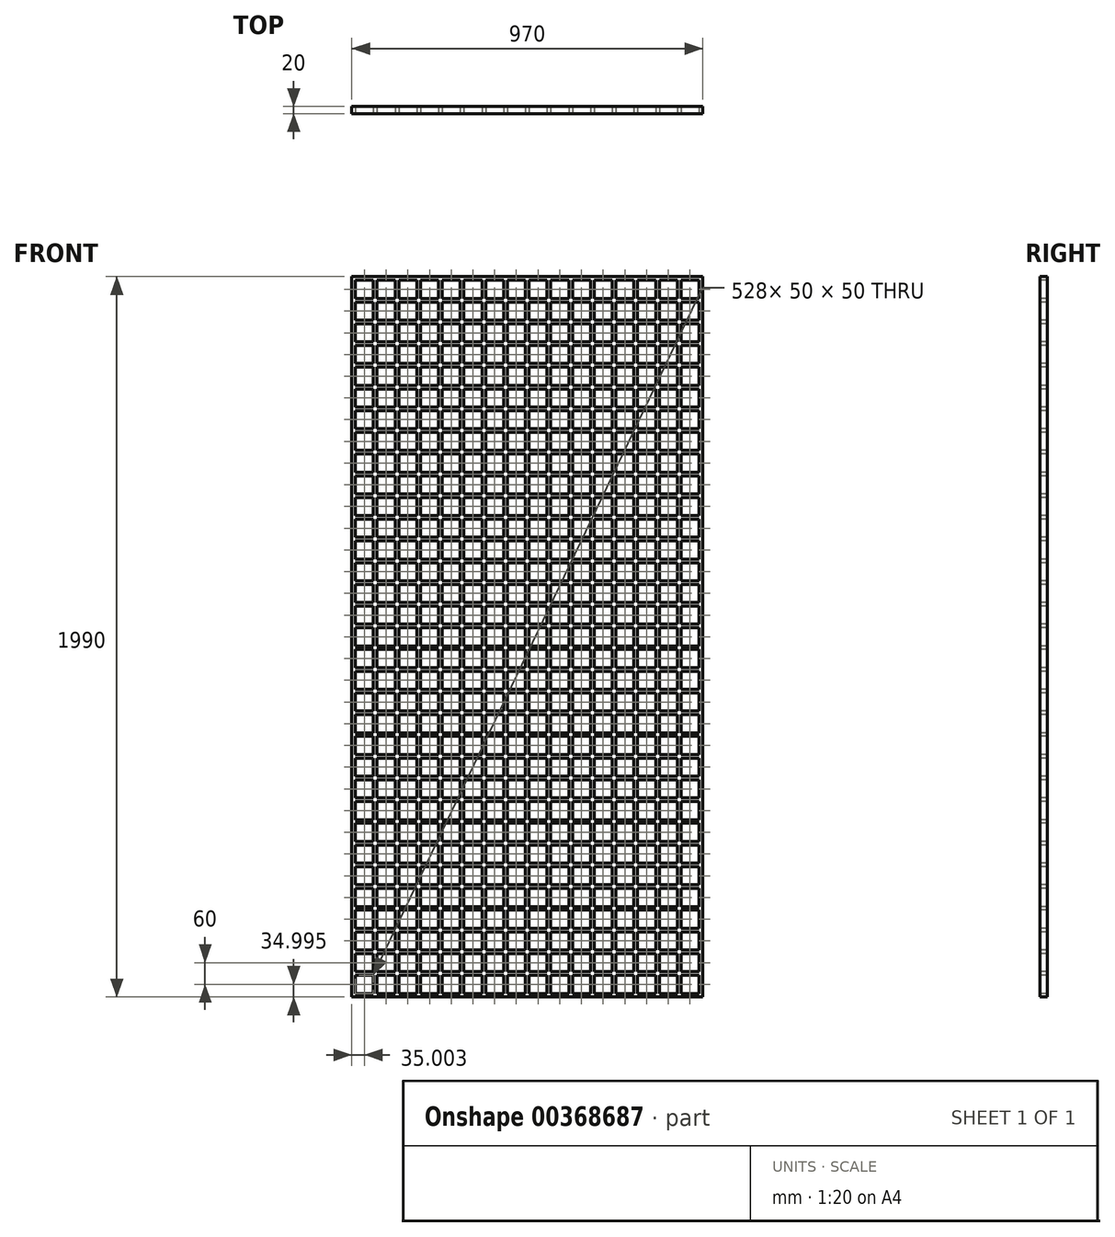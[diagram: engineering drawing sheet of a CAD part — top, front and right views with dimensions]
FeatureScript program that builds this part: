
annotation { "Feature Type Name" : "Feature", "Feature Type Description" : "" }
export const myFeature = defineFeature(function(context is Context, id is Id, definition is map)
    precondition{}
    {
        {
            var Q0;
            Q0=qCreatedBy(makeId("Front.planeOp"),FACE);
            var sketch = newSketch(context, id + "F0", { "sketchPlane" : qUnion([Q0])});
            skLineSegment(sketch, "E0.bottom", {"start": v(-491.66, 1631.1) * mm, "end": v(478.34, 1631.1) * mm});
            skLineSegment(sketch, "E0.top", {"start": v(-491.66, -358.9) * mm, "end": v(478.34, -358.9) * mm});
            skLineSegment(sketch, "E0.left", {"start": v(-491.66, 1631.1) * mm, "end": v(-491.66, -358.9) * mm});
            skLineSegment(sketch, "E0.right", {"start": v(478.34, 1631.1) * mm, "end": v(478.34, -358.9) * mm});
            skSolve(sketch);
        }
        {
            var Q0;
            Q0=makeQuery(id+"F0.imprint","IMPRINT",FACE,{"disambiguationData":[TD([[makeQuery(id+"F0.imprint","IMPRINT",EDGE,{"derivedFrom":sQuery(id+"F0.wireOp",EDGE,"E0.bottom")}),-1.0]])]});
            extrude(context, id + "F1", {"entities" : qUnion([Q0]), "depth" : 20 * mm});
        }
        {
            var Q0;
            Q0=makeQuery(id+"F1.opExtrude","CAP_FACE",FACE,{"disambiguationData":[OSD([sQuery(id+"F0.wireOp",EDGE,"E0.bottom"),sQuery(id+"F0.wireOp",EDGE,"E0.top"),sQuery(id+"F0.wireOp",EDGE,"E0.left"),sQuery(id+"F0.wireOp",EDGE,"E0.right")])],"isStart":false});
            var sketch = newSketch(context, id + "F2", { "sketchPlane" : qUnion([Q0])});
            skLineSegment(sketch, "E1.bottom", {"start": v(-481.66, 1621.1) * mm, "end": v(-431.66, 1621.1) * mm});
            skLineSegment(sketch, "E1.top", {"start": v(-481.66, 1571.1) * mm, "end": v(-431.66, 1571.1) * mm});
            skLineSegment(sketch, "E1.left", {"start": v(-481.66, 1621.1) * mm, "end": v(-481.66, 1571.1) * mm});
            skLineSegment(sketch, "E1.right", {"start": v(-431.66, 1621.1) * mm, "end": v(-431.66, 1571.1) * mm});
            skLineSegment(sketch, "E2.0.1.0", {"start": v(-431.66, 1561.1) * mm, "end": v(-431.66, 1511.1) * mm});
            skLineSegment(sketch, "E2.0.1.1", {"start": v(-481.66, 1511.1) * mm, "end": v(-431.66, 1511.1) * mm});
            skLineSegment(sketch, "E2.0.1.2", {"start": v(-481.66, 1561.1) * mm, "end": v(-481.66, 1511.1) * mm});
            skLineSegment(sketch, "E2.0.1.3", {"start": v(-481.66, 1561.1) * mm, "end": v(-431.66, 1561.1) * mm});
            skLineSegment(sketch, "E2.0.2.0", {"start": v(-431.66, 1501.1) * mm, "end": v(-431.66, 1451.1) * mm});
            skLineSegment(sketch, "E2.0.2.1", {"start": v(-481.66, 1451.1) * mm, "end": v(-431.66, 1451.1) * mm});
            skLineSegment(sketch, "E2.0.2.2", {"start": v(-481.66, 1501.1) * mm, "end": v(-481.66, 1451.1) * mm});
            skLineSegment(sketch, "E2.0.2.3", {"start": v(-481.66, 1501.1) * mm, "end": v(-431.66, 1501.1) * mm});
            skLineSegment(sketch, "E2.0.3.0", {"start": v(-431.66, 1441.1) * mm, "end": v(-431.66, 1391.1) * mm});
            skLineSegment(sketch, "E2.0.3.1", {"start": v(-481.66, 1391.1) * mm, "end": v(-431.66, 1391.1) * mm});
            skLineSegment(sketch, "E2.0.3.2", {"start": v(-481.66, 1441.1) * mm, "end": v(-481.66, 1391.1) * mm});
            skLineSegment(sketch, "E2.0.3.3", {"start": v(-481.66, 1441.1) * mm, "end": v(-431.66, 1441.1) * mm});
            skLineSegment(sketch, "E2.0.4.0", {"start": v(-431.66, 1381.1) * mm, "end": v(-431.66, 1331.1) * mm});
            skLineSegment(sketch, "E2.0.4.1", {"start": v(-481.66, 1331.1) * mm, "end": v(-431.66, 1331.1) * mm});
            skLineSegment(sketch, "E2.0.4.2", {"start": v(-481.66, 1381.1) * mm, "end": v(-481.66, 1331.1) * mm});
            skLineSegment(sketch, "E2.0.4.3", {"start": v(-481.66, 1381.1) * mm, "end": v(-431.66, 1381.1) * mm});
            skLineSegment(sketch, "E2.0.5.0", {"start": v(-431.66, 1321.1) * mm, "end": v(-431.66, 1271.1) * mm});
            skLineSegment(sketch, "E2.0.5.1", {"start": v(-481.66, 1271.1) * mm, "end": v(-431.66, 1271.1) * mm});
            skLineSegment(sketch, "E2.0.5.2", {"start": v(-481.66, 1321.1) * mm, "end": v(-481.66, 1271.1) * mm});
            skLineSegment(sketch, "E2.0.5.3", {"start": v(-481.66, 1321.1) * mm, "end": v(-431.66, 1321.1) * mm});
            skLineSegment(sketch, "E2.0.6.0", {"start": v(-431.66, 1261.1) * mm, "end": v(-431.66, 1211.1) * mm});
            skLineSegment(sketch, "E2.0.6.1", {"start": v(-481.66, 1211.1) * mm, "end": v(-431.66, 1211.1) * mm});
            skLineSegment(sketch, "E2.0.6.2", {"start": v(-481.66, 1261.1) * mm, "end": v(-481.66, 1211.1) * mm});
            skLineSegment(sketch, "E2.0.6.3", {"start": v(-481.66, 1261.1) * mm, "end": v(-431.66, 1261.1) * mm});
            skLineSegment(sketch, "E2.0.7.0", {"start": v(-431.66, 1201.1) * mm, "end": v(-431.66, 1151.1) * mm});
            skLineSegment(sketch, "E2.0.7.1", {"start": v(-481.66, 1151.1) * mm, "end": v(-431.66, 1151.1) * mm});
            skLineSegment(sketch, "E2.0.7.2", {"start": v(-481.66, 1201.1) * mm, "end": v(-481.66, 1151.1) * mm});
            skLineSegment(sketch, "E2.0.7.3", {"start": v(-481.66, 1201.1) * mm, "end": v(-431.66, 1201.1) * mm});
            skLineSegment(sketch, "E2.0.8.0", {"start": v(-431.66, 1141.1) * mm, "end": v(-431.66, 1091.1) * mm});
            skLineSegment(sketch, "E2.0.8.1", {"start": v(-481.66, 1091.1) * mm, "end": v(-431.66, 1091.1) * mm});
            skLineSegment(sketch, "E2.0.8.2", {"start": v(-481.66, 1141.1) * mm, "end": v(-481.66, 1091.1) * mm});
            skLineSegment(sketch, "E2.0.8.3", {"start": v(-481.66, 1141.1) * mm, "end": v(-431.66, 1141.1) * mm});
            skLineSegment(sketch, "E2.0.9.0", {"start": v(-431.66, 1081.1) * mm, "end": v(-431.66, 1031.1) * mm});
            skLineSegment(sketch, "E2.0.9.1", {"start": v(-481.66, 1031.1) * mm, "end": v(-431.66, 1031.1) * mm});
            skLineSegment(sketch, "E2.0.9.2", {"start": v(-481.66, 1081.1) * mm, "end": v(-481.66, 1031.1) * mm});
            skLineSegment(sketch, "E2.0.9.3", {"start": v(-481.66, 1081.1) * mm, "end": v(-431.66, 1081.1) * mm});
            skLineSegment(sketch, "E2.0.10.0", {"start": v(-431.66, 1021.1) * mm, "end": v(-431.66, 971.1) * mm});
            skLineSegment(sketch, "E2.0.10.1", {"start": v(-481.66, 971.1) * mm, "end": v(-431.66, 971.1) * mm});
            skLineSegment(sketch, "E2.0.10.2", {"start": v(-481.66, 1021.1) * mm, "end": v(-481.66, 971.1) * mm});
            skLineSegment(sketch, "E2.0.10.3", {"start": v(-481.66, 1021.1) * mm, "end": v(-431.66, 1021.1) * mm});
            skLineSegment(sketch, "E2.0.11.0", {"start": v(-431.66, 961.1) * mm, "end": v(-431.66, 911.1) * mm});
            skLineSegment(sketch, "E2.0.11.1", {"start": v(-481.66, 911.1) * mm, "end": v(-431.66, 911.1) * mm});
            skLineSegment(sketch, "E2.0.11.2", {"start": v(-481.66, 961.1) * mm, "end": v(-481.66, 911.1) * mm});
            skLineSegment(sketch, "E2.0.11.3", {"start": v(-481.66, 961.1) * mm, "end": v(-431.66, 961.1) * mm});
            skLineSegment(sketch, "E2.0.12.0", {"start": v(-431.66, 901.1) * mm, "end": v(-431.66, 851.1) * mm});
            skLineSegment(sketch, "E2.0.12.1", {"start": v(-481.66, 851.1) * mm, "end": v(-431.66, 851.1) * mm});
            skLineSegment(sketch, "E2.0.12.2", {"start": v(-481.66, 901.1) * mm, "end": v(-481.66, 851.1) * mm});
            skLineSegment(sketch, "E2.0.12.3", {"start": v(-481.66, 901.1) * mm, "end": v(-431.66, 901.1) * mm});
            skLineSegment(sketch, "E2.0.13.0", {"start": v(-431.66, 841.1) * mm, "end": v(-431.66, 791.1) * mm});
            skLineSegment(sketch, "E2.0.13.1", {"start": v(-481.66, 791.1) * mm, "end": v(-431.66, 791.1) * mm});
            skLineSegment(sketch, "E2.0.13.2", {"start": v(-481.66, 841.1) * mm, "end": v(-481.66, 791.1) * mm});
            skLineSegment(sketch, "E2.0.13.3", {"start": v(-481.66, 841.1) * mm, "end": v(-431.66, 841.1) * mm});
            skLineSegment(sketch, "E2.0.14.0", {"start": v(-431.66, 781.1) * mm, "end": v(-431.66, 731.1) * mm});
            skLineSegment(sketch, "E2.0.14.1", {"start": v(-481.66, 731.1) * mm, "end": v(-431.66, 731.1) * mm});
            skLineSegment(sketch, "E2.0.14.2", {"start": v(-481.66, 781.1) * mm, "end": v(-481.66, 731.1) * mm});
            skLineSegment(sketch, "E2.0.14.3", {"start": v(-481.66, 781.1) * mm, "end": v(-431.66, 781.1) * mm});
            skLineSegment(sketch, "E2.0.15.0", {"start": v(-431.66, 721.1) * mm, "end": v(-431.66, 671.1) * mm});
            skLineSegment(sketch, "E2.0.15.1", {"start": v(-481.66, 671.1) * mm, "end": v(-431.66, 671.1) * mm});
            skLineSegment(sketch, "E2.0.15.2", {"start": v(-481.66, 721.1) * mm, "end": v(-481.66, 671.1) * mm});
            skLineSegment(sketch, "E2.0.15.3", {"start": v(-481.66, 721.1) * mm, "end": v(-431.66, 721.1) * mm});
            skLineSegment(sketch, "E2.0.16.0", {"start": v(-431.66, 661.1) * mm, "end": v(-431.66, 611.1) * mm});
            skLineSegment(sketch, "E2.0.16.1", {"start": v(-481.66, 611.1) * mm, "end": v(-431.66, 611.1) * mm});
            skLineSegment(sketch, "E2.0.16.2", {"start": v(-481.66, 661.1) * mm, "end": v(-481.66, 611.1) * mm});
            skLineSegment(sketch, "E2.0.16.3", {"start": v(-481.66, 661.1) * mm, "end": v(-431.66, 661.1) * mm});
            skLineSegment(sketch, "E2.0.17.0", {"start": v(-431.66, 601.1) * mm, "end": v(-431.66, 551.1) * mm});
            skLineSegment(sketch, "E2.0.17.1", {"start": v(-481.66, 551.1) * mm, "end": v(-431.66, 551.1) * mm});
            skLineSegment(sketch, "E2.0.17.2", {"start": v(-481.66, 601.1) * mm, "end": v(-481.66, 551.1) * mm});
            skLineSegment(sketch, "E2.0.17.3", {"start": v(-481.66, 601.1) * mm, "end": v(-431.66, 601.1) * mm});
            skLineSegment(sketch, "E2.0.18.0", {"start": v(-431.66, 541.1) * mm, "end": v(-431.66, 491.1) * mm});
            skLineSegment(sketch, "E2.0.18.1", {"start": v(-481.66, 491.1) * mm, "end": v(-431.66, 491.1) * mm});
            skLineSegment(sketch, "E2.0.18.2", {"start": v(-481.66, 541.1) * mm, "end": v(-481.66, 491.1) * mm});
            skLineSegment(sketch, "E2.0.18.3", {"start": v(-481.66, 541.1) * mm, "end": v(-431.66, 541.1) * mm});
            skLineSegment(sketch, "E2.0.19.0", {"start": v(-431.66, 481.1) * mm, "end": v(-431.66, 431.1) * mm});
            skLineSegment(sketch, "E2.0.19.1", {"start": v(-481.66, 431.1) * mm, "end": v(-431.66, 431.1) * mm});
            skLineSegment(sketch, "E2.0.19.2", {"start": v(-481.66, 481.1) * mm, "end": v(-481.66, 431.1) * mm});
            skLineSegment(sketch, "E2.0.19.3", {"start": v(-481.66, 481.1) * mm, "end": v(-431.66, 481.1) * mm});
            skLineSegment(sketch, "E2.0.20.0", {"start": v(-431.66, 421.1) * mm, "end": v(-431.66, 371.1) * mm});
            skLineSegment(sketch, "E2.0.20.1", {"start": v(-481.66, 371.1) * mm, "end": v(-431.66, 371.1) * mm});
            skLineSegment(sketch, "E2.0.20.2", {"start": v(-481.66, 421.1) * mm, "end": v(-481.66, 371.1) * mm});
            skLineSegment(sketch, "E2.0.20.3", {"start": v(-481.66, 421.1) * mm, "end": v(-431.66, 421.1) * mm});
            skLineSegment(sketch, "E2.0.21.0", {"start": v(-431.66, 361.1) * mm, "end": v(-431.66, 311.1) * mm});
            skLineSegment(sketch, "E2.0.21.1", {"start": v(-481.66, 311.1) * mm, "end": v(-431.66, 311.1) * mm});
            skLineSegment(sketch, "E2.0.21.2", {"start": v(-481.66, 361.1) * mm, "end": v(-481.66, 311.1) * mm});
            skLineSegment(sketch, "E2.0.21.3", {"start": v(-481.66, 361.1) * mm, "end": v(-431.66, 361.1) * mm});
            skLineSegment(sketch, "E2.0.22.0", {"start": v(-431.66, 301.1) * mm, "end": v(-431.66, 251.1) * mm});
            skLineSegment(sketch, "E2.0.22.1", {"start": v(-481.66, 251.1) * mm, "end": v(-431.66, 251.1) * mm});
            skLineSegment(sketch, "E2.0.22.2", {"start": v(-481.66, 301.1) * mm, "end": v(-481.66, 251.1) * mm});
            skLineSegment(sketch, "E2.0.22.3", {"start": v(-481.66, 301.1) * mm, "end": v(-431.66, 301.1) * mm});
            skLineSegment(sketch, "E2.0.23.0", {"start": v(-431.66, 241.1) * mm, "end": v(-431.66, 191.1) * mm});
            skLineSegment(sketch, "E2.0.23.1", {"start": v(-481.66, 191.1) * mm, "end": v(-431.66, 191.1) * mm});
            skLineSegment(sketch, "E2.0.23.2", {"start": v(-481.66, 241.1) * mm, "end": v(-481.66, 191.1) * mm});
            skLineSegment(sketch, "E2.0.23.3", {"start": v(-481.66, 241.1) * mm, "end": v(-431.66, 241.1) * mm});
            skLineSegment(sketch, "E2.0.24.0", {"start": v(-431.66, 181.1) * mm, "end": v(-431.66, 131.1) * mm});
            skLineSegment(sketch, "E2.0.24.1", {"start": v(-481.66, 131.1) * mm, "end": v(-431.66, 131.1) * mm});
            skLineSegment(sketch, "E2.0.24.2", {"start": v(-481.66, 181.1) * mm, "end": v(-481.66, 131.1) * mm});
            skLineSegment(sketch, "E2.0.24.3", {"start": v(-481.66, 181.1) * mm, "end": v(-431.66, 181.1) * mm});
            skLineSegment(sketch, "E2.0.25.0", {"start": v(-431.66, 121.1) * mm, "end": v(-431.66, 71.1) * mm});
            skLineSegment(sketch, "E2.0.25.1", {"start": v(-481.66, 71.1) * mm, "end": v(-431.66, 71.1) * mm});
            skLineSegment(sketch, "E2.0.25.2", {"start": v(-481.66, 121.1) * mm, "end": v(-481.66, 71.1) * mm});
            skLineSegment(sketch, "E2.0.25.3", {"start": v(-481.66, 121.1) * mm, "end": v(-431.66, 121.1) * mm});
            skLineSegment(sketch, "E2.0.26.0", {"start": v(-431.66, 61.1) * mm, "end": v(-431.66, 11.1) * mm});
            skLineSegment(sketch, "E2.0.26.1", {"start": v(-481.66, 11.1) * mm, "end": v(-431.66, 11.1) * mm});
            skLineSegment(sketch, "E2.0.26.2", {"start": v(-481.66, 61.1) * mm, "end": v(-481.66, 11.1) * mm});
            skLineSegment(sketch, "E2.0.26.3", {"start": v(-481.66, 61.1) * mm, "end": v(-431.66, 61.1) * mm});
            skLineSegment(sketch, "E2.0.27.0", {"start": v(-431.66, 1.1) * mm, "end": v(-431.66, -48.9) * mm});
            skLineSegment(sketch, "E2.0.27.1", {"start": v(-481.66, -48.9) * mm, "end": v(-431.66, -48.9) * mm});
            skLineSegment(sketch, "E2.0.27.2", {"start": v(-481.66, 1.1) * mm, "end": v(-481.66, -48.9) * mm});
            skLineSegment(sketch, "E2.0.27.3", {"start": v(-481.66, 1.1) * mm, "end": v(-431.66, 1.1) * mm});
            skLineSegment(sketch, "E2.0.28.0", {"start": v(-431.66, -58.9) * mm, "end": v(-431.66, -108.9) * mm});
            skLineSegment(sketch, "E2.0.28.1", {"start": v(-481.66, -108.9) * mm, "end": v(-431.66, -108.9) * mm});
            skLineSegment(sketch, "E2.0.28.2", {"start": v(-481.66, -58.9) * mm, "end": v(-481.66, -108.9) * mm});
            skLineSegment(sketch, "E2.0.28.3", {"start": v(-481.66, -58.9) * mm, "end": v(-431.66, -58.9) * mm});
            skLineSegment(sketch, "E2.0.29.0", {"start": v(-431.66, -118.9) * mm, "end": v(-431.66, -168.9) * mm});
            skLineSegment(sketch, "E2.0.29.1", {"start": v(-481.66, -168.9) * mm, "end": v(-431.66, -168.9) * mm});
            skLineSegment(sketch, "E2.0.29.2", {"start": v(-481.66, -118.9) * mm, "end": v(-481.66, -168.9) * mm});
            skLineSegment(sketch, "E2.0.29.3", {"start": v(-481.66, -118.9) * mm, "end": v(-431.66, -118.9) * mm});
            skLineSegment(sketch, "E2.0.30.0", {"start": v(-431.66, -178.9) * mm, "end": v(-431.66, -228.9) * mm});
            skLineSegment(sketch, "E2.0.30.1", {"start": v(-481.66, -228.9) * mm, "end": v(-431.66, -228.9) * mm});
            skLineSegment(sketch, "E2.0.30.2", {"start": v(-481.66, -178.9) * mm, "end": v(-481.66, -228.9) * mm});
            skLineSegment(sketch, "E2.0.30.3", {"start": v(-481.66, -178.9) * mm, "end": v(-431.66, -178.9) * mm});
            skLineSegment(sketch, "E2.0.31.0", {"start": v(-431.66, -238.9) * mm, "end": v(-431.66, -288.9) * mm});
            skLineSegment(sketch, "E2.0.31.1", {"start": v(-481.66, -288.9) * mm, "end": v(-431.66, -288.9) * mm});
            skLineSegment(sketch, "E2.0.31.2", {"start": v(-481.66, -238.9) * mm, "end": v(-481.66, -288.9) * mm});
            skLineSegment(sketch, "E2.0.31.3", {"start": v(-481.66, -238.9) * mm, "end": v(-431.66, -238.9) * mm});
            skLineSegment(sketch, "E2.0.32.0", {"start": v(-431.66, -298.9) * mm, "end": v(-431.66, -348.9) * mm});
            skLineSegment(sketch, "E2.0.32.1", {"start": v(-481.66, -348.9) * mm, "end": v(-431.66, -348.9) * mm});
            skLineSegment(sketch, "E2.0.32.2", {"start": v(-481.66, -298.9) * mm, "end": v(-481.66, -348.9) * mm});
            skLineSegment(sketch, "E2.0.32.3", {"start": v(-481.66, -298.9) * mm, "end": v(-431.66, -298.9) * mm});
            skLineSegment(sketch, "E2.1.0.0", {"start": v(-371.66, 1621.1) * mm, "end": v(-371.66, 1571.1) * mm});
            skLineSegment(sketch, "E2.1.0.1", {"start": v(-421.66, 1571.1) * mm, "end": v(-371.66, 1571.1) * mm});
            skLineSegment(sketch, "E2.1.0.2", {"start": v(-421.66, 1621.1) * mm, "end": v(-421.66, 1571.1) * mm});
            skLineSegment(sketch, "E2.1.0.3", {"start": v(-421.66, 1621.1) * mm, "end": v(-371.66, 1621.1) * mm});
            skLineSegment(sketch, "E2.1.1.0", {"start": v(-371.66, 1561.1) * mm, "end": v(-371.66, 1511.1) * mm});
            skLineSegment(sketch, "E2.1.1.1", {"start": v(-421.66, 1511.1) * mm, "end": v(-371.66, 1511.1) * mm});
            skLineSegment(sketch, "E2.1.1.2", {"start": v(-421.66, 1561.1) * mm, "end": v(-421.66, 1511.1) * mm});
            skLineSegment(sketch, "E2.1.1.3", {"start": v(-421.66, 1561.1) * mm, "end": v(-371.66, 1561.1) * mm});
            skLineSegment(sketch, "E2.1.2.0", {"start": v(-371.66, 1501.1) * mm, "end": v(-371.66, 1451.1) * mm});
            skLineSegment(sketch, "E2.1.2.1", {"start": v(-421.66, 1451.1) * mm, "end": v(-371.66, 1451.1) * mm});
            skLineSegment(sketch, "E2.1.2.2", {"start": v(-421.66, 1501.1) * mm, "end": v(-421.66, 1451.1) * mm});
            skLineSegment(sketch, "E2.1.2.3", {"start": v(-421.66, 1501.1) * mm, "end": v(-371.66, 1501.1) * mm});
            skLineSegment(sketch, "E2.1.3.0", {"start": v(-371.66, 1441.1) * mm, "end": v(-371.66, 1391.1) * mm});
            skLineSegment(sketch, "E2.1.3.1", {"start": v(-421.66, 1391.1) * mm, "end": v(-371.66, 1391.1) * mm});
            skLineSegment(sketch, "E2.1.3.2", {"start": v(-421.66, 1441.1) * mm, "end": v(-421.66, 1391.1) * mm});
            skLineSegment(sketch, "E2.1.3.3", {"start": v(-421.66, 1441.1) * mm, "end": v(-371.66, 1441.1) * mm});
            skLineSegment(sketch, "E2.1.4.0", {"start": v(-371.66, 1381.1) * mm, "end": v(-371.66, 1331.1) * mm});
            skLineSegment(sketch, "E2.1.4.1", {"start": v(-421.66, 1331.1) * mm, "end": v(-371.66, 1331.1) * mm});
            skLineSegment(sketch, "E2.1.4.2", {"start": v(-421.66, 1381.1) * mm, "end": v(-421.66, 1331.1) * mm});
            skLineSegment(sketch, "E2.1.4.3", {"start": v(-421.66, 1381.1) * mm, "end": v(-371.66, 1381.1) * mm});
            skLineSegment(sketch, "E2.1.5.0", {"start": v(-371.66, 1321.1) * mm, "end": v(-371.66, 1271.1) * mm});
            skLineSegment(sketch, "E2.1.5.1", {"start": v(-421.66, 1271.1) * mm, "end": v(-371.66, 1271.1) * mm});
            skLineSegment(sketch, "E2.1.5.2", {"start": v(-421.66, 1321.1) * mm, "end": v(-421.66, 1271.1) * mm});
            skLineSegment(sketch, "E2.1.5.3", {"start": v(-421.66, 1321.1) * mm, "end": v(-371.66, 1321.1) * mm});
            skLineSegment(sketch, "E2.1.6.0", {"start": v(-371.66, 1261.1) * mm, "end": v(-371.66, 1211.1) * mm});
            skLineSegment(sketch, "E2.1.6.1", {"start": v(-421.66, 1211.1) * mm, "end": v(-371.66, 1211.1) * mm});
            skLineSegment(sketch, "E2.1.6.2", {"start": v(-421.66, 1261.1) * mm, "end": v(-421.66, 1211.1) * mm});
            skLineSegment(sketch, "E2.1.6.3", {"start": v(-421.66, 1261.1) * mm, "end": v(-371.66, 1261.1) * mm});
            skLineSegment(sketch, "E2.1.7.0", {"start": v(-371.66, 1201.1) * mm, "end": v(-371.66, 1151.1) * mm});
            skLineSegment(sketch, "E2.1.7.1", {"start": v(-421.66, 1151.1) * mm, "end": v(-371.66, 1151.1) * mm});
            skLineSegment(sketch, "E2.1.7.2", {"start": v(-421.66, 1201.1) * mm, "end": v(-421.66, 1151.1) * mm});
            skLineSegment(sketch, "E2.1.7.3", {"start": v(-421.66, 1201.1) * mm, "end": v(-371.66, 1201.1) * mm});
            skLineSegment(sketch, "E2.1.8.0", {"start": v(-371.66, 1141.1) * mm, "end": v(-371.66, 1091.1) * mm});
            skLineSegment(sketch, "E2.1.8.1", {"start": v(-421.66, 1091.1) * mm, "end": v(-371.66, 1091.1) * mm});
            skLineSegment(sketch, "E2.1.8.2", {"start": v(-421.66, 1141.1) * mm, "end": v(-421.66, 1091.1) * mm});
            skLineSegment(sketch, "E2.1.8.3", {"start": v(-421.66, 1141.1) * mm, "end": v(-371.66, 1141.1) * mm});
            skLineSegment(sketch, "E2.1.9.0", {"start": v(-371.66, 1081.1) * mm, "end": v(-371.66, 1031.1) * mm});
            skLineSegment(sketch, "E2.1.9.1", {"start": v(-421.66, 1031.1) * mm, "end": v(-371.66, 1031.1) * mm});
            skLineSegment(sketch, "E2.1.9.2", {"start": v(-421.66, 1081.1) * mm, "end": v(-421.66, 1031.1) * mm});
            skLineSegment(sketch, "E2.1.9.3", {"start": v(-421.66, 1081.1) * mm, "end": v(-371.66, 1081.1) * mm});
            skLineSegment(sketch, "E2.1.10.0", {"start": v(-371.66, 1021.1) * mm, "end": v(-371.66, 971.1) * mm});
            skLineSegment(sketch, "E2.1.10.1", {"start": v(-421.66, 971.1) * mm, "end": v(-371.66, 971.1) * mm});
            skLineSegment(sketch, "E2.1.10.2", {"start": v(-421.66, 1021.1) * mm, "end": v(-421.66, 971.1) * mm});
            skLineSegment(sketch, "E2.1.10.3", {"start": v(-421.66, 1021.1) * mm, "end": v(-371.66, 1021.1) * mm});
            skLineSegment(sketch, "E2.1.11.0", {"start": v(-371.66, 961.1) * mm, "end": v(-371.66, 911.1) * mm});
            skLineSegment(sketch, "E2.1.11.1", {"start": v(-421.66, 911.1) * mm, "end": v(-371.66, 911.1) * mm});
            skLineSegment(sketch, "E2.1.11.2", {"start": v(-421.66, 961.1) * mm, "end": v(-421.66, 911.1) * mm});
            skLineSegment(sketch, "E2.1.11.3", {"start": v(-421.66, 961.1) * mm, "end": v(-371.66, 961.1) * mm});
            skLineSegment(sketch, "E2.1.12.0", {"start": v(-371.66, 901.1) * mm, "end": v(-371.66, 851.1) * mm});
            skLineSegment(sketch, "E2.1.12.1", {"start": v(-421.66, 851.1) * mm, "end": v(-371.66, 851.1) * mm});
            skLineSegment(sketch, "E2.1.12.2", {"start": v(-421.66, 901.1) * mm, "end": v(-421.66, 851.1) * mm});
            skLineSegment(sketch, "E2.1.12.3", {"start": v(-421.66, 901.1) * mm, "end": v(-371.66, 901.1) * mm});
            skLineSegment(sketch, "E2.1.13.0", {"start": v(-371.66, 841.1) * mm, "end": v(-371.66, 791.1) * mm});
            skLineSegment(sketch, "E2.1.13.1", {"start": v(-421.66, 791.1) * mm, "end": v(-371.66, 791.1) * mm});
            skLineSegment(sketch, "E2.1.13.2", {"start": v(-421.66, 841.1) * mm, "end": v(-421.66, 791.1) * mm});
            skLineSegment(sketch, "E2.1.13.3", {"start": v(-421.66, 841.1) * mm, "end": v(-371.66, 841.1) * mm});
            skLineSegment(sketch, "E2.1.14.0", {"start": v(-371.66, 781.1) * mm, "end": v(-371.66, 731.1) * mm});
            skLineSegment(sketch, "E2.1.14.1", {"start": v(-421.66, 731.1) * mm, "end": v(-371.66, 731.1) * mm});
            skLineSegment(sketch, "E2.1.14.2", {"start": v(-421.66, 781.1) * mm, "end": v(-421.66, 731.1) * mm});
            skLineSegment(sketch, "E2.1.14.3", {"start": v(-421.66, 781.1) * mm, "end": v(-371.66, 781.1) * mm});
            skLineSegment(sketch, "E2.1.15.0", {"start": v(-371.66, 721.1) * mm, "end": v(-371.66, 671.1) * mm});
            skLineSegment(sketch, "E2.1.15.1", {"start": v(-421.66, 671.1) * mm, "end": v(-371.66, 671.1) * mm});
            skLineSegment(sketch, "E2.1.15.2", {"start": v(-421.66, 721.1) * mm, "end": v(-421.66, 671.1) * mm});
            skLineSegment(sketch, "E2.1.15.3", {"start": v(-421.66, 721.1) * mm, "end": v(-371.66, 721.1) * mm});
            skLineSegment(sketch, "E2.1.16.0", {"start": v(-371.66, 661.1) * mm, "end": v(-371.66, 611.1) * mm});
            skLineSegment(sketch, "E2.1.16.1", {"start": v(-421.66, 611.1) * mm, "end": v(-371.66, 611.1) * mm});
            skLineSegment(sketch, "E2.1.16.2", {"start": v(-421.66, 661.1) * mm, "end": v(-421.66, 611.1) * mm});
            skLineSegment(sketch, "E2.1.16.3", {"start": v(-421.66, 661.1) * mm, "end": v(-371.66, 661.1) * mm});
            skLineSegment(sketch, "E2.1.17.0", {"start": v(-371.66, 601.1) * mm, "end": v(-371.66, 551.1) * mm});
            skLineSegment(sketch, "E2.1.17.1", {"start": v(-421.66, 551.1) * mm, "end": v(-371.66, 551.1) * mm});
            skLineSegment(sketch, "E2.1.17.2", {"start": v(-421.66, 601.1) * mm, "end": v(-421.66, 551.1) * mm});
            skLineSegment(sketch, "E2.1.17.3", {"start": v(-421.66, 601.1) * mm, "end": v(-371.66, 601.1) * mm});
            skLineSegment(sketch, "E2.1.18.0", {"start": v(-371.66, 541.1) * mm, "end": v(-371.66, 491.1) * mm});
            skLineSegment(sketch, "E2.1.18.1", {"start": v(-421.66, 491.1) * mm, "end": v(-371.66, 491.1) * mm});
            skLineSegment(sketch, "E2.1.18.2", {"start": v(-421.66, 541.1) * mm, "end": v(-421.66, 491.1) * mm});
            skLineSegment(sketch, "E2.1.18.3", {"start": v(-421.66, 541.1) * mm, "end": v(-371.66, 541.1) * mm});
            skLineSegment(sketch, "E2.1.19.0", {"start": v(-371.66, 481.1) * mm, "end": v(-371.66, 431.1) * mm});
            skLineSegment(sketch, "E2.1.19.1", {"start": v(-421.66, 431.1) * mm, "end": v(-371.66, 431.1) * mm});
            skLineSegment(sketch, "E2.1.19.2", {"start": v(-421.66, 481.1) * mm, "end": v(-421.66, 431.1) * mm});
            skLineSegment(sketch, "E2.1.19.3", {"start": v(-421.66, 481.1) * mm, "end": v(-371.66, 481.1) * mm});
            skLineSegment(sketch, "E2.1.20.0", {"start": v(-371.66, 421.1) * mm, "end": v(-371.66, 371.1) * mm});
            skLineSegment(sketch, "E2.1.20.1", {"start": v(-421.66, 371.1) * mm, "end": v(-371.66, 371.1) * mm});
            skLineSegment(sketch, "E2.1.20.2", {"start": v(-421.66, 421.1) * mm, "end": v(-421.66, 371.1) * mm});
            skLineSegment(sketch, "E2.1.20.3", {"start": v(-421.66, 421.1) * mm, "end": v(-371.66, 421.1) * mm});
            skLineSegment(sketch, "E2.1.21.0", {"start": v(-371.66, 361.1) * mm, "end": v(-371.66, 311.1) * mm});
            skLineSegment(sketch, "E2.1.21.1", {"start": v(-421.66, 311.1) * mm, "end": v(-371.66, 311.1) * mm});
            skLineSegment(sketch, "E2.1.21.2", {"start": v(-421.66, 361.1) * mm, "end": v(-421.66, 311.1) * mm});
            skLineSegment(sketch, "E2.1.21.3", {"start": v(-421.66, 361.1) * mm, "end": v(-371.66, 361.1) * mm});
            skLineSegment(sketch, "E2.1.22.0", {"start": v(-371.66, 301.1) * mm, "end": v(-371.66, 251.1) * mm});
            skLineSegment(sketch, "E2.1.22.1", {"start": v(-421.66, 251.1) * mm, "end": v(-371.66, 251.1) * mm});
            skLineSegment(sketch, "E2.1.22.2", {"start": v(-421.66, 301.1) * mm, "end": v(-421.66, 251.1) * mm});
            skLineSegment(sketch, "E2.1.22.3", {"start": v(-421.66, 301.1) * mm, "end": v(-371.66, 301.1) * mm});
            skLineSegment(sketch, "E2.1.23.0", {"start": v(-371.66, 241.1) * mm, "end": v(-371.66, 191.1) * mm});
            skLineSegment(sketch, "E2.1.23.1", {"start": v(-421.66, 191.1) * mm, "end": v(-371.66, 191.1) * mm});
            skLineSegment(sketch, "E2.1.23.2", {"start": v(-421.66, 241.1) * mm, "end": v(-421.66, 191.1) * mm});
            skLineSegment(sketch, "E2.1.23.3", {"start": v(-421.66, 241.1) * mm, "end": v(-371.66, 241.1) * mm});
            skLineSegment(sketch, "E2.1.24.0", {"start": v(-371.66, 181.1) * mm, "end": v(-371.66, 131.1) * mm});
            skLineSegment(sketch, "E2.1.24.1", {"start": v(-421.66, 131.1) * mm, "end": v(-371.66, 131.1) * mm});
            skLineSegment(sketch, "E2.1.24.2", {"start": v(-421.66, 181.1) * mm, "end": v(-421.66, 131.1) * mm});
            skLineSegment(sketch, "E2.1.24.3", {"start": v(-421.66, 181.1) * mm, "end": v(-371.66, 181.1) * mm});
            skLineSegment(sketch, "E2.1.25.0", {"start": v(-371.66, 121.1) * mm, "end": v(-371.66, 71.1) * mm});
            skLineSegment(sketch, "E2.1.25.1", {"start": v(-421.66, 71.1) * mm, "end": v(-371.66, 71.1) * mm});
            skLineSegment(sketch, "E2.1.25.2", {"start": v(-421.66, 121.1) * mm, "end": v(-421.66, 71.1) * mm});
            skLineSegment(sketch, "E2.1.25.3", {"start": v(-421.66, 121.1) * mm, "end": v(-371.66, 121.1) * mm});
            skLineSegment(sketch, "E2.1.26.0", {"start": v(-371.66, 61.1) * mm, "end": v(-371.66, 11.1) * mm});
            skLineSegment(sketch, "E2.1.26.1", {"start": v(-421.66, 11.1) * mm, "end": v(-371.66, 11.1) * mm});
            skLineSegment(sketch, "E2.1.26.2", {"start": v(-421.66, 61.1) * mm, "end": v(-421.66, 11.1) * mm});
            skLineSegment(sketch, "E2.1.26.3", {"start": v(-421.66, 61.1) * mm, "end": v(-371.66, 61.1) * mm});
            skLineSegment(sketch, "E2.1.27.0", {"start": v(-371.66, 1.1) * mm, "end": v(-371.66, -48.9) * mm});
            skLineSegment(sketch, "E2.1.27.1", {"start": v(-421.66, -48.9) * mm, "end": v(-371.66, -48.9) * mm});
            skLineSegment(sketch, "E2.1.27.2", {"start": v(-421.66, 1.1) * mm, "end": v(-421.66, -48.9) * mm});
            skLineSegment(sketch, "E2.1.27.3", {"start": v(-421.66, 1.1) * mm, "end": v(-371.66, 1.1) * mm});
            skLineSegment(sketch, "E2.1.28.0", {"start": v(-371.66, -58.9) * mm, "end": v(-371.66, -108.9) * mm});
            skLineSegment(sketch, "E2.1.28.1", {"start": v(-421.66, -108.9) * mm, "end": v(-371.66, -108.9) * mm});
            skLineSegment(sketch, "E2.1.28.2", {"start": v(-421.66, -58.9) * mm, "end": v(-421.66, -108.9) * mm});
            skLineSegment(sketch, "E2.1.28.3", {"start": v(-421.66, -58.9) * mm, "end": v(-371.66, -58.9) * mm});
            skLineSegment(sketch, "E2.1.29.0", {"start": v(-371.66, -118.9) * mm, "end": v(-371.66, -168.9) * mm});
            skLineSegment(sketch, "E2.1.29.1", {"start": v(-421.66, -168.9) * mm, "end": v(-371.66, -168.9) * mm});
            skLineSegment(sketch, "E2.1.29.2", {"start": v(-421.66, -118.9) * mm, "end": v(-421.66, -168.9) * mm});
            skLineSegment(sketch, "E2.1.29.3", {"start": v(-421.66, -118.9) * mm, "end": v(-371.66, -118.9) * mm});
            skLineSegment(sketch, "E2.1.30.0", {"start": v(-371.66, -178.9) * mm, "end": v(-371.66, -228.9) * mm});
            skLineSegment(sketch, "E2.1.30.1", {"start": v(-421.66, -228.9) * mm, "end": v(-371.66, -228.9) * mm});
            skLineSegment(sketch, "E2.1.30.2", {"start": v(-421.66, -178.9) * mm, "end": v(-421.66, -228.9) * mm});
            skLineSegment(sketch, "E2.1.30.3", {"start": v(-421.66, -178.9) * mm, "end": v(-371.66, -178.9) * mm});
            skLineSegment(sketch, "E2.1.31.0", {"start": v(-371.66, -238.9) * mm, "end": v(-371.66, -288.9) * mm});
            skLineSegment(sketch, "E2.1.31.1", {"start": v(-421.66, -288.9) * mm, "end": v(-371.66, -288.9) * mm});
            skLineSegment(sketch, "E2.1.31.2", {"start": v(-421.66, -238.9) * mm, "end": v(-421.66, -288.9) * mm});
            skLineSegment(sketch, "E2.1.31.3", {"start": v(-421.66, -238.9) * mm, "end": v(-371.66, -238.9) * mm});
            skLineSegment(sketch, "E2.1.32.0", {"start": v(-371.66, -298.9) * mm, "end": v(-371.66, -348.9) * mm});
            skLineSegment(sketch, "E2.1.32.1", {"start": v(-421.66, -348.9) * mm, "end": v(-371.66, -348.9) * mm});
            skLineSegment(sketch, "E2.1.32.2", {"start": v(-421.66, -298.9) * mm, "end": v(-421.66, -348.9) * mm});
            skLineSegment(sketch, "E2.1.32.3", {"start": v(-421.66, -298.9) * mm, "end": v(-371.66, -298.9) * mm});
            skLineSegment(sketch, "E2.2.0.0", {"start": v(-311.66, 1621.1) * mm, "end": v(-311.66, 1571.1) * mm});
            skLineSegment(sketch, "E2.2.0.1", {"start": v(-361.66, 1571.1) * mm, "end": v(-311.66, 1571.1) * mm});
            skLineSegment(sketch, "E2.2.0.2", {"start": v(-361.66, 1621.1) * mm, "end": v(-361.66, 1571.1) * mm});
            skLineSegment(sketch, "E2.2.0.3", {"start": v(-361.66, 1621.1) * mm, "end": v(-311.66, 1621.1) * mm});
            skLineSegment(sketch, "E2.2.1.0", {"start": v(-311.66, 1561.1) * mm, "end": v(-311.66, 1511.1) * mm});
            skLineSegment(sketch, "E2.2.1.1", {"start": v(-361.66, 1511.1) * mm, "end": v(-311.66, 1511.1) * mm});
            skLineSegment(sketch, "E2.2.1.2", {"start": v(-361.66, 1561.1) * mm, "end": v(-361.66, 1511.1) * mm});
            skLineSegment(sketch, "E2.2.1.3", {"start": v(-361.66, 1561.1) * mm, "end": v(-311.66, 1561.1) * mm});
            skLineSegment(sketch, "E2.2.2.0", {"start": v(-311.66, 1501.1) * mm, "end": v(-311.66, 1451.1) * mm});
            skLineSegment(sketch, "E2.2.2.1", {"start": v(-361.66, 1451.1) * mm, "end": v(-311.66, 1451.1) * mm});
            skLineSegment(sketch, "E2.2.2.2", {"start": v(-361.66, 1501.1) * mm, "end": v(-361.66, 1451.1) * mm});
            skLineSegment(sketch, "E2.2.2.3", {"start": v(-361.66, 1501.1) * mm, "end": v(-311.66, 1501.1) * mm});
            skLineSegment(sketch, "E2.2.3.0", {"start": v(-311.66, 1441.1) * mm, "end": v(-311.66, 1391.1) * mm});
            skLineSegment(sketch, "E2.2.3.1", {"start": v(-361.66, 1391.1) * mm, "end": v(-311.66, 1391.1) * mm});
            skLineSegment(sketch, "E2.2.3.2", {"start": v(-361.66, 1441.1) * mm, "end": v(-361.66, 1391.1) * mm});
            skLineSegment(sketch, "E2.2.3.3", {"start": v(-361.66, 1441.1) * mm, "end": v(-311.66, 1441.1) * mm});
            skLineSegment(sketch, "E2.2.4.0", {"start": v(-311.66, 1381.1) * mm, "end": v(-311.66, 1331.1) * mm});
            skLineSegment(sketch, "E2.2.4.1", {"start": v(-361.66, 1331.1) * mm, "end": v(-311.66, 1331.1) * mm});
            skLineSegment(sketch, "E2.2.4.2", {"start": v(-361.66, 1381.1) * mm, "end": v(-361.66, 1331.1) * mm});
            skLineSegment(sketch, "E2.2.4.3", {"start": v(-361.66, 1381.1) * mm, "end": v(-311.66, 1381.1) * mm});
            skLineSegment(sketch, "E2.2.5.0", {"start": v(-311.66, 1321.1) * mm, "end": v(-311.66, 1271.1) * mm});
            skLineSegment(sketch, "E2.2.5.1", {"start": v(-361.66, 1271.1) * mm, "end": v(-311.66, 1271.1) * mm});
            skLineSegment(sketch, "E2.2.5.2", {"start": v(-361.66, 1321.1) * mm, "end": v(-361.66, 1271.1) * mm});
            skLineSegment(sketch, "E2.2.5.3", {"start": v(-361.66, 1321.1) * mm, "end": v(-311.66, 1321.1) * mm});
            skLineSegment(sketch, "E2.2.6.0", {"start": v(-311.66, 1261.1) * mm, "end": v(-311.66, 1211.1) * mm});
            skLineSegment(sketch, "E2.2.6.1", {"start": v(-361.66, 1211.1) * mm, "end": v(-311.66, 1211.1) * mm});
            skLineSegment(sketch, "E2.2.6.2", {"start": v(-361.66, 1261.1) * mm, "end": v(-361.66, 1211.1) * mm});
            skLineSegment(sketch, "E2.2.6.3", {"start": v(-361.66, 1261.1) * mm, "end": v(-311.66, 1261.1) * mm});
            skLineSegment(sketch, "E2.2.7.0", {"start": v(-311.66, 1201.1) * mm, "end": v(-311.66, 1151.1) * mm});
            skLineSegment(sketch, "E2.2.7.1", {"start": v(-361.66, 1151.1) * mm, "end": v(-311.66, 1151.1) * mm});
            skLineSegment(sketch, "E2.2.7.2", {"start": v(-361.66, 1201.1) * mm, "end": v(-361.66, 1151.1) * mm});
            skLineSegment(sketch, "E2.2.7.3", {"start": v(-361.66, 1201.1) * mm, "end": v(-311.66, 1201.1) * mm});
            skLineSegment(sketch, "E2.2.8.0", {"start": v(-311.66, 1141.1) * mm, "end": v(-311.66, 1091.1) * mm});
            skLineSegment(sketch, "E2.2.8.1", {"start": v(-361.66, 1091.1) * mm, "end": v(-311.66, 1091.1) * mm});
            skLineSegment(sketch, "E2.2.8.2", {"start": v(-361.66, 1141.1) * mm, "end": v(-361.66, 1091.1) * mm});
            skLineSegment(sketch, "E2.2.8.3", {"start": v(-361.66, 1141.1) * mm, "end": v(-311.66, 1141.1) * mm});
            skLineSegment(sketch, "E2.2.9.0", {"start": v(-311.66, 1081.1) * mm, "end": v(-311.66, 1031.1) * mm});
            skLineSegment(sketch, "E2.2.9.1", {"start": v(-361.66, 1031.1) * mm, "end": v(-311.66, 1031.1) * mm});
            skLineSegment(sketch, "E2.2.9.2", {"start": v(-361.66, 1081.1) * mm, "end": v(-361.66, 1031.1) * mm});
            skLineSegment(sketch, "E2.2.9.3", {"start": v(-361.66, 1081.1) * mm, "end": v(-311.66, 1081.1) * mm});
            skLineSegment(sketch, "E2.2.10.0", {"start": v(-311.66, 1021.1) * mm, "end": v(-311.66, 971.1) * mm});
            skLineSegment(sketch, "E2.2.10.1", {"start": v(-361.66, 971.1) * mm, "end": v(-311.66, 971.1) * mm});
            skLineSegment(sketch, "E2.2.10.2", {"start": v(-361.66, 1021.1) * mm, "end": v(-361.66, 971.1) * mm});
            skLineSegment(sketch, "E2.2.10.3", {"start": v(-361.66, 1021.1) * mm, "end": v(-311.66, 1021.1) * mm});
            skLineSegment(sketch, "E2.2.11.0", {"start": v(-311.66, 961.1) * mm, "end": v(-311.66, 911.1) * mm});
            skLineSegment(sketch, "E2.2.11.1", {"start": v(-361.66, 911.1) * mm, "end": v(-311.66, 911.1) * mm});
            skLineSegment(sketch, "E2.2.11.2", {"start": v(-361.66, 961.1) * mm, "end": v(-361.66, 911.1) * mm});
            skLineSegment(sketch, "E2.2.11.3", {"start": v(-361.66, 961.1) * mm, "end": v(-311.66, 961.1) * mm});
            skLineSegment(sketch, "E2.2.12.0", {"start": v(-311.66, 901.1) * mm, "end": v(-311.66, 851.1) * mm});
            skLineSegment(sketch, "E2.2.12.1", {"start": v(-361.66, 851.1) * mm, "end": v(-311.66, 851.1) * mm});
            skLineSegment(sketch, "E2.2.12.2", {"start": v(-361.66, 901.1) * mm, "end": v(-361.66, 851.1) * mm});
            skLineSegment(sketch, "E2.2.12.3", {"start": v(-361.66, 901.1) * mm, "end": v(-311.66, 901.1) * mm});
            skLineSegment(sketch, "E2.2.13.0", {"start": v(-311.66, 841.1) * mm, "end": v(-311.66, 791.1) * mm});
            skLineSegment(sketch, "E2.2.13.1", {"start": v(-361.66, 791.1) * mm, "end": v(-311.66, 791.1) * mm});
            skLineSegment(sketch, "E2.2.13.2", {"start": v(-361.66, 841.1) * mm, "end": v(-361.66, 791.1) * mm});
            skLineSegment(sketch, "E2.2.13.3", {"start": v(-361.66, 841.1) * mm, "end": v(-311.66, 841.1) * mm});
            skLineSegment(sketch, "E2.2.14.0", {"start": v(-311.66, 781.1) * mm, "end": v(-311.66, 731.1) * mm});
            skLineSegment(sketch, "E2.2.14.1", {"start": v(-361.66, 731.1) * mm, "end": v(-311.66, 731.1) * mm});
            skLineSegment(sketch, "E2.2.14.2", {"start": v(-361.66, 781.1) * mm, "end": v(-361.66, 731.1) * mm});
            skLineSegment(sketch, "E2.2.14.3", {"start": v(-361.66, 781.1) * mm, "end": v(-311.66, 781.1) * mm});
            skLineSegment(sketch, "E2.2.15.0", {"start": v(-311.66, 721.1) * mm, "end": v(-311.66, 671.1) * mm});
            skLineSegment(sketch, "E2.2.15.1", {"start": v(-361.66, 671.1) * mm, "end": v(-311.66, 671.1) * mm});
            skLineSegment(sketch, "E2.2.15.2", {"start": v(-361.66, 721.1) * mm, "end": v(-361.66, 671.1) * mm});
            skLineSegment(sketch, "E2.2.15.3", {"start": v(-361.66, 721.1) * mm, "end": v(-311.66, 721.1) * mm});
            skLineSegment(sketch, "E2.2.16.0", {"start": v(-311.66, 661.1) * mm, "end": v(-311.66, 611.1) * mm});
            skLineSegment(sketch, "E2.2.16.1", {"start": v(-361.66, 611.1) * mm, "end": v(-311.66, 611.1) * mm});
            skLineSegment(sketch, "E2.2.16.2", {"start": v(-361.66, 661.1) * mm, "end": v(-361.66, 611.1) * mm});
            skLineSegment(sketch, "E2.2.16.3", {"start": v(-361.66, 661.1) * mm, "end": v(-311.66, 661.1) * mm});
            skLineSegment(sketch, "E2.2.17.0", {"start": v(-311.66, 601.1) * mm, "end": v(-311.66, 551.1) * mm});
            skLineSegment(sketch, "E2.2.17.1", {"start": v(-361.66, 551.1) * mm, "end": v(-311.66, 551.1) * mm});
            skLineSegment(sketch, "E2.2.17.2", {"start": v(-361.66, 601.1) * mm, "end": v(-361.66, 551.1) * mm});
            skLineSegment(sketch, "E2.2.17.3", {"start": v(-361.66, 601.1) * mm, "end": v(-311.66, 601.1) * mm});
            skLineSegment(sketch, "E2.2.18.0", {"start": v(-311.66, 541.1) * mm, "end": v(-311.66, 491.1) * mm});
            skLineSegment(sketch, "E2.2.18.1", {"start": v(-361.66, 491.1) * mm, "end": v(-311.66, 491.1) * mm});
            skLineSegment(sketch, "E2.2.18.2", {"start": v(-361.66, 541.1) * mm, "end": v(-361.66, 491.1) * mm});
            skLineSegment(sketch, "E2.2.18.3", {"start": v(-361.66, 541.1) * mm, "end": v(-311.66, 541.1) * mm});
            skLineSegment(sketch, "E2.2.19.0", {"start": v(-311.66, 481.1) * mm, "end": v(-311.66, 431.1) * mm});
            skLineSegment(sketch, "E2.2.19.1", {"start": v(-361.66, 431.1) * mm, "end": v(-311.66, 431.1) * mm});
            skLineSegment(sketch, "E2.2.19.2", {"start": v(-361.66, 481.1) * mm, "end": v(-361.66, 431.1) * mm});
            skLineSegment(sketch, "E2.2.19.3", {"start": v(-361.66, 481.1) * mm, "end": v(-311.66, 481.1) * mm});
            skLineSegment(sketch, "E2.2.20.0", {"start": v(-311.66, 421.1) * mm, "end": v(-311.66, 371.1) * mm});
            skLineSegment(sketch, "E2.2.20.1", {"start": v(-361.66, 371.1) * mm, "end": v(-311.66, 371.1) * mm});
            skLineSegment(sketch, "E2.2.20.2", {"start": v(-361.66, 421.1) * mm, "end": v(-361.66, 371.1) * mm});
            skLineSegment(sketch, "E2.2.20.3", {"start": v(-361.66, 421.1) * mm, "end": v(-311.66, 421.1) * mm});
            skLineSegment(sketch, "E2.2.21.0", {"start": v(-311.66, 361.1) * mm, "end": v(-311.66, 311.1) * mm});
            skLineSegment(sketch, "E2.2.21.1", {"start": v(-361.66, 311.1) * mm, "end": v(-311.66, 311.1) * mm});
            skLineSegment(sketch, "E2.2.21.2", {"start": v(-361.66, 361.1) * mm, "end": v(-361.66, 311.1) * mm});
            skLineSegment(sketch, "E2.2.21.3", {"start": v(-361.66, 361.1) * mm, "end": v(-311.66, 361.1) * mm});
            skLineSegment(sketch, "E2.2.22.0", {"start": v(-311.66, 301.1) * mm, "end": v(-311.66, 251.1) * mm});
            skLineSegment(sketch, "E2.2.22.1", {"start": v(-361.66, 251.1) * mm, "end": v(-311.66, 251.1) * mm});
            skLineSegment(sketch, "E2.2.22.2", {"start": v(-361.66, 301.1) * mm, "end": v(-361.66, 251.1) * mm});
            skLineSegment(sketch, "E2.2.22.3", {"start": v(-361.66, 301.1) * mm, "end": v(-311.66, 301.1) * mm});
            skLineSegment(sketch, "E2.2.23.0", {"start": v(-311.66, 241.1) * mm, "end": v(-311.66, 191.1) * mm});
            skLineSegment(sketch, "E2.2.23.1", {"start": v(-361.66, 191.1) * mm, "end": v(-311.66, 191.1) * mm});
            skLineSegment(sketch, "E2.2.23.2", {"start": v(-361.66, 241.1) * mm, "end": v(-361.66, 191.1) * mm});
            skLineSegment(sketch, "E2.2.23.3", {"start": v(-361.66, 241.1) * mm, "end": v(-311.66, 241.1) * mm});
            skLineSegment(sketch, "E2.2.24.0", {"start": v(-311.66, 181.1) * mm, "end": v(-311.66, 131.1) * mm});
            skLineSegment(sketch, "E2.2.24.1", {"start": v(-361.66, 131.1) * mm, "end": v(-311.66, 131.1) * mm});
            skLineSegment(sketch, "E2.2.24.2", {"start": v(-361.66, 181.1) * mm, "end": v(-361.66, 131.1) * mm});
            skLineSegment(sketch, "E2.2.24.3", {"start": v(-361.66, 181.1) * mm, "end": v(-311.66, 181.1) * mm});
            skLineSegment(sketch, "E2.2.25.0", {"start": v(-311.66, 121.1) * mm, "end": v(-311.66, 71.1) * mm});
            skLineSegment(sketch, "E2.2.25.1", {"start": v(-361.66, 71.1) * mm, "end": v(-311.66, 71.1) * mm});
            skLineSegment(sketch, "E2.2.25.2", {"start": v(-361.66, 121.1) * mm, "end": v(-361.66, 71.1) * mm});
            skLineSegment(sketch, "E2.2.25.3", {"start": v(-361.66, 121.1) * mm, "end": v(-311.66, 121.1) * mm});
            skLineSegment(sketch, "E2.2.26.0", {"start": v(-311.66, 61.1) * mm, "end": v(-311.66, 11.1) * mm});
            skLineSegment(sketch, "E2.2.26.1", {"start": v(-361.66, 11.1) * mm, "end": v(-311.66, 11.1) * mm});
            skLineSegment(sketch, "E2.2.26.2", {"start": v(-361.66, 61.1) * mm, "end": v(-361.66, 11.1) * mm});
            skLineSegment(sketch, "E2.2.26.3", {"start": v(-361.66, 61.1) * mm, "end": v(-311.66, 61.1) * mm});
            skLineSegment(sketch, "E2.2.27.0", {"start": v(-311.66, 1.1) * mm, "end": v(-311.66, -48.9) * mm});
            skLineSegment(sketch, "E2.2.27.1", {"start": v(-361.66, -48.9) * mm, "end": v(-311.66, -48.9) * mm});
            skLineSegment(sketch, "E2.2.27.2", {"start": v(-361.66, 1.1) * mm, "end": v(-361.66, -48.9) * mm});
            skLineSegment(sketch, "E2.2.27.3", {"start": v(-361.66, 1.1) * mm, "end": v(-311.66, 1.1) * mm});
            skLineSegment(sketch, "E2.2.28.0", {"start": v(-311.66, -58.9) * mm, "end": v(-311.66, -108.9) * mm});
            skLineSegment(sketch, "E2.2.28.1", {"start": v(-361.66, -108.9) * mm, "end": v(-311.66, -108.9) * mm});
            skLineSegment(sketch, "E2.2.28.2", {"start": v(-361.66, -58.9) * mm, "end": v(-361.66, -108.9) * mm});
            skLineSegment(sketch, "E2.2.28.3", {"start": v(-361.66, -58.9) * mm, "end": v(-311.66, -58.9) * mm});
            skLineSegment(sketch, "E2.2.29.0", {"start": v(-311.66, -118.9) * mm, "end": v(-311.66, -168.9) * mm});
            skLineSegment(sketch, "E2.2.29.1", {"start": v(-361.66, -168.9) * mm, "end": v(-311.66, -168.9) * mm});
            skLineSegment(sketch, "E2.2.29.2", {"start": v(-361.66, -118.9) * mm, "end": v(-361.66, -168.9) * mm});
            skLineSegment(sketch, "E2.2.29.3", {"start": v(-361.66, -118.9) * mm, "end": v(-311.66, -118.9) * mm});
            skLineSegment(sketch, "E2.2.30.0", {"start": v(-311.66, -178.9) * mm, "end": v(-311.66, -228.9) * mm});
            skLineSegment(sketch, "E2.2.30.1", {"start": v(-361.66, -228.9) * mm, "end": v(-311.66, -228.9) * mm});
            skLineSegment(sketch, "E2.2.30.2", {"start": v(-361.66, -178.9) * mm, "end": v(-361.66, -228.9) * mm});
            skLineSegment(sketch, "E2.2.30.3", {"start": v(-361.66, -178.9) * mm, "end": v(-311.66, -178.9) * mm});
            skLineSegment(sketch, "E2.2.31.0", {"start": v(-311.66, -238.9) * mm, "end": v(-311.66, -288.9) * mm});
            skLineSegment(sketch, "E2.2.31.1", {"start": v(-361.66, -288.9) * mm, "end": v(-311.66, -288.9) * mm});
            skLineSegment(sketch, "E2.2.31.2", {"start": v(-361.66, -238.9) * mm, "end": v(-361.66, -288.9) * mm});
            skLineSegment(sketch, "E2.2.31.3", {"start": v(-361.66, -238.9) * mm, "end": v(-311.66, -238.9) * mm});
            skLineSegment(sketch, "E2.2.32.0", {"start": v(-311.66, -298.9) * mm, "end": v(-311.66, -348.9) * mm});
            skLineSegment(sketch, "E2.2.32.1", {"start": v(-361.66, -348.9) * mm, "end": v(-311.66, -348.9) * mm});
            skLineSegment(sketch, "E2.2.32.2", {"start": v(-361.66, -298.9) * mm, "end": v(-361.66, -348.9) * mm});
            skLineSegment(sketch, "E2.2.32.3", {"start": v(-361.66, -298.9) * mm, "end": v(-311.66, -298.9) * mm});
            skLineSegment(sketch, "E2.3.0.0", {"start": v(-251.66, 1621.1) * mm, "end": v(-251.66, 1571.1) * mm});
            skLineSegment(sketch, "E2.3.0.1", {"start": v(-301.66, 1571.1) * mm, "end": v(-251.66, 1571.1) * mm});
            skLineSegment(sketch, "E2.3.0.2", {"start": v(-301.66, 1621.1) * mm, "end": v(-301.66, 1571.1) * mm});
            skLineSegment(sketch, "E2.3.0.3", {"start": v(-301.66, 1621.1) * mm, "end": v(-251.66, 1621.1) * mm});
            skLineSegment(sketch, "E2.3.1.0", {"start": v(-251.66, 1561.1) * mm, "end": v(-251.66, 1511.1) * mm});
            skLineSegment(sketch, "E2.3.1.1", {"start": v(-301.66, 1511.1) * mm, "end": v(-251.66, 1511.1) * mm});
            skLineSegment(sketch, "E2.3.1.2", {"start": v(-301.66, 1561.1) * mm, "end": v(-301.66, 1511.1) * mm});
            skLineSegment(sketch, "E2.3.1.3", {"start": v(-301.66, 1561.1) * mm, "end": v(-251.66, 1561.1) * mm});
            skLineSegment(sketch, "E2.3.2.0", {"start": v(-251.66, 1501.1) * mm, "end": v(-251.66, 1451.1) * mm});
            skLineSegment(sketch, "E2.3.2.1", {"start": v(-301.66, 1451.1) * mm, "end": v(-251.66, 1451.1) * mm});
            skLineSegment(sketch, "E2.3.2.2", {"start": v(-301.66, 1501.1) * mm, "end": v(-301.66, 1451.1) * mm});
            skLineSegment(sketch, "E2.3.2.3", {"start": v(-301.66, 1501.1) * mm, "end": v(-251.66, 1501.1) * mm});
            skLineSegment(sketch, "E2.3.3.0", {"start": v(-251.66, 1441.1) * mm, "end": v(-251.66, 1391.1) * mm});
            skLineSegment(sketch, "E2.3.3.1", {"start": v(-301.66, 1391.1) * mm, "end": v(-251.66, 1391.1) * mm});
            skLineSegment(sketch, "E2.3.3.2", {"start": v(-301.66, 1441.1) * mm, "end": v(-301.66, 1391.1) * mm});
            skLineSegment(sketch, "E2.3.3.3", {"start": v(-301.66, 1441.1) * mm, "end": v(-251.66, 1441.1) * mm});
            skLineSegment(sketch, "E2.3.4.0", {"start": v(-251.66, 1381.1) * mm, "end": v(-251.66, 1331.1) * mm});
            skLineSegment(sketch, "E2.3.4.1", {"start": v(-301.66, 1331.1) * mm, "end": v(-251.66, 1331.1) * mm});
            skLineSegment(sketch, "E2.3.4.2", {"start": v(-301.66, 1381.1) * mm, "end": v(-301.66, 1331.1) * mm});
            skLineSegment(sketch, "E2.3.4.3", {"start": v(-301.66, 1381.1) * mm, "end": v(-251.66, 1381.1) * mm});
            skLineSegment(sketch, "E2.3.5.0", {"start": v(-251.66, 1321.1) * mm, "end": v(-251.66, 1271.1) * mm});
            skLineSegment(sketch, "E2.3.5.1", {"start": v(-301.66, 1271.1) * mm, "end": v(-251.66, 1271.1) * mm});
            skLineSegment(sketch, "E2.3.5.2", {"start": v(-301.66, 1321.1) * mm, "end": v(-301.66, 1271.1) * mm});
            skLineSegment(sketch, "E2.3.5.3", {"start": v(-301.66, 1321.1) * mm, "end": v(-251.66, 1321.1) * mm});
            skLineSegment(sketch, "E2.3.6.0", {"start": v(-251.66, 1261.1) * mm, "end": v(-251.66, 1211.1) * mm});
            skLineSegment(sketch, "E2.3.6.1", {"start": v(-301.66, 1211.1) * mm, "end": v(-251.66, 1211.1) * mm});
            skLineSegment(sketch, "E2.3.6.2", {"start": v(-301.66, 1261.1) * mm, "end": v(-301.66, 1211.1) * mm});
            skLineSegment(sketch, "E2.3.6.3", {"start": v(-301.66, 1261.1) * mm, "end": v(-251.66, 1261.1) * mm});
            skLineSegment(sketch, "E2.3.7.0", {"start": v(-251.66, 1201.1) * mm, "end": v(-251.66, 1151.1) * mm});
            skLineSegment(sketch, "E2.3.7.1", {"start": v(-301.66, 1151.1) * mm, "end": v(-251.66, 1151.1) * mm});
            skLineSegment(sketch, "E2.3.7.2", {"start": v(-301.66, 1201.1) * mm, "end": v(-301.66, 1151.1) * mm});
            skLineSegment(sketch, "E2.3.7.3", {"start": v(-301.66, 1201.1) * mm, "end": v(-251.66, 1201.1) * mm});
            skLineSegment(sketch, "E2.3.8.0", {"start": v(-251.66, 1141.1) * mm, "end": v(-251.66, 1091.1) * mm});
            skLineSegment(sketch, "E2.3.8.1", {"start": v(-301.66, 1091.1) * mm, "end": v(-251.66, 1091.1) * mm});
            skLineSegment(sketch, "E2.3.8.2", {"start": v(-301.66, 1141.1) * mm, "end": v(-301.66, 1091.1) * mm});
            skLineSegment(sketch, "E2.3.8.3", {"start": v(-301.66, 1141.1) * mm, "end": v(-251.66, 1141.1) * mm});
            skLineSegment(sketch, "E2.3.9.0", {"start": v(-251.66, 1081.1) * mm, "end": v(-251.66, 1031.1) * mm});
            skLineSegment(sketch, "E2.3.9.1", {"start": v(-301.66, 1031.1) * mm, "end": v(-251.66, 1031.1) * mm});
            skLineSegment(sketch, "E2.3.9.2", {"start": v(-301.66, 1081.1) * mm, "end": v(-301.66, 1031.1) * mm});
            skLineSegment(sketch, "E2.3.9.3", {"start": v(-301.66, 1081.1) * mm, "end": v(-251.66, 1081.1) * mm});
            skLineSegment(sketch, "E2.3.10.0", {"start": v(-251.66, 1021.1) * mm, "end": v(-251.66, 971.1) * mm});
            skLineSegment(sketch, "E2.3.10.1", {"start": v(-301.66, 971.1) * mm, "end": v(-251.66, 971.1) * mm});
            skLineSegment(sketch, "E2.3.10.2", {"start": v(-301.66, 1021.1) * mm, "end": v(-301.66, 971.1) * mm});
            skLineSegment(sketch, "E2.3.10.3", {"start": v(-301.66, 1021.1) * mm, "end": v(-251.66, 1021.1) * mm});
            skLineSegment(sketch, "E2.3.11.0", {"start": v(-251.66, 961.1) * mm, "end": v(-251.66, 911.1) * mm});
            skLineSegment(sketch, "E2.3.11.1", {"start": v(-301.66, 911.1) * mm, "end": v(-251.66, 911.1) * mm});
            skLineSegment(sketch, "E2.3.11.2", {"start": v(-301.66, 961.1) * mm, "end": v(-301.66, 911.1) * mm});
            skLineSegment(sketch, "E2.3.11.3", {"start": v(-301.66, 961.1) * mm, "end": v(-251.66, 961.1) * mm});
            skLineSegment(sketch, "E2.3.12.0", {"start": v(-251.66, 901.1) * mm, "end": v(-251.66, 851.1) * mm});
            skLineSegment(sketch, "E2.3.12.1", {"start": v(-301.66, 851.1) * mm, "end": v(-251.66, 851.1) * mm});
            skLineSegment(sketch, "E2.3.12.2", {"start": v(-301.66, 901.1) * mm, "end": v(-301.66, 851.1) * mm});
            skLineSegment(sketch, "E2.3.12.3", {"start": v(-301.66, 901.1) * mm, "end": v(-251.66, 901.1) * mm});
            skLineSegment(sketch, "E2.3.13.0", {"start": v(-251.66, 841.1) * mm, "end": v(-251.66, 791.1) * mm});
            skLineSegment(sketch, "E2.3.13.1", {"start": v(-301.66, 791.1) * mm, "end": v(-251.66, 791.1) * mm});
            skLineSegment(sketch, "E2.3.13.2", {"start": v(-301.66, 841.1) * mm, "end": v(-301.66, 791.1) * mm});
            skLineSegment(sketch, "E2.3.13.3", {"start": v(-301.66, 841.1) * mm, "end": v(-251.66, 841.1) * mm});
            skLineSegment(sketch, "E2.3.14.0", {"start": v(-251.66, 781.1) * mm, "end": v(-251.66, 731.1) * mm});
            skLineSegment(sketch, "E2.3.14.1", {"start": v(-301.66, 731.1) * mm, "end": v(-251.66, 731.1) * mm});
            skLineSegment(sketch, "E2.3.14.2", {"start": v(-301.66, 781.1) * mm, "end": v(-301.66, 731.1) * mm});
            skLineSegment(sketch, "E2.3.14.3", {"start": v(-301.66, 781.1) * mm, "end": v(-251.66, 781.1) * mm});
            skLineSegment(sketch, "E2.3.15.0", {"start": v(-251.66, 721.1) * mm, "end": v(-251.66, 671.1) * mm});
            skLineSegment(sketch, "E2.3.15.1", {"start": v(-301.66, 671.1) * mm, "end": v(-251.66, 671.1) * mm});
            skLineSegment(sketch, "E2.3.15.2", {"start": v(-301.66, 721.1) * mm, "end": v(-301.66, 671.1) * mm});
            skLineSegment(sketch, "E2.3.15.3", {"start": v(-301.66, 721.1) * mm, "end": v(-251.66, 721.1) * mm});
            skLineSegment(sketch, "E2.3.16.0", {"start": v(-251.66, 661.1) * mm, "end": v(-251.66, 611.1) * mm});
            skLineSegment(sketch, "E2.3.16.1", {"start": v(-301.66, 611.1) * mm, "end": v(-251.66, 611.1) * mm});
            skLineSegment(sketch, "E2.3.16.2", {"start": v(-301.66, 661.1) * mm, "end": v(-301.66, 611.1) * mm});
            skLineSegment(sketch, "E2.3.16.3", {"start": v(-301.66, 661.1) * mm, "end": v(-251.66, 661.1) * mm});
            skLineSegment(sketch, "E2.3.17.0", {"start": v(-251.66, 601.1) * mm, "end": v(-251.66, 551.1) * mm});
            skLineSegment(sketch, "E2.3.17.1", {"start": v(-301.66, 551.1) * mm, "end": v(-251.66, 551.1) * mm});
            skLineSegment(sketch, "E2.3.17.2", {"start": v(-301.66, 601.1) * mm, "end": v(-301.66, 551.1) * mm});
            skLineSegment(sketch, "E2.3.17.3", {"start": v(-301.66, 601.1) * mm, "end": v(-251.66, 601.1) * mm});
            skLineSegment(sketch, "E2.3.18.0", {"start": v(-251.66, 541.1) * mm, "end": v(-251.66, 491.1) * mm});
            skLineSegment(sketch, "E2.3.18.1", {"start": v(-301.66, 491.1) * mm, "end": v(-251.66, 491.1) * mm});
            skLineSegment(sketch, "E2.3.18.2", {"start": v(-301.66, 541.1) * mm, "end": v(-301.66, 491.1) * mm});
            skLineSegment(sketch, "E2.3.18.3", {"start": v(-301.66, 541.1) * mm, "end": v(-251.66, 541.1) * mm});
            skLineSegment(sketch, "E2.3.19.0", {"start": v(-251.66, 481.1) * mm, "end": v(-251.66, 431.1) * mm});
            skLineSegment(sketch, "E2.3.19.1", {"start": v(-301.66, 431.1) * mm, "end": v(-251.66, 431.1) * mm});
            skLineSegment(sketch, "E2.3.19.2", {"start": v(-301.66, 481.1) * mm, "end": v(-301.66, 431.1) * mm});
            skLineSegment(sketch, "E2.3.19.3", {"start": v(-301.66, 481.1) * mm, "end": v(-251.66, 481.1) * mm});
            skLineSegment(sketch, "E2.3.20.0", {"start": v(-251.66, 421.1) * mm, "end": v(-251.66, 371.1) * mm});
            skLineSegment(sketch, "E2.3.20.1", {"start": v(-301.66, 371.1) * mm, "end": v(-251.66, 371.1) * mm});
            skLineSegment(sketch, "E2.3.20.2", {"start": v(-301.66, 421.1) * mm, "end": v(-301.66, 371.1) * mm});
            skLineSegment(sketch, "E2.3.20.3", {"start": v(-301.66, 421.1) * mm, "end": v(-251.66, 421.1) * mm});
            skLineSegment(sketch, "E2.3.21.0", {"start": v(-251.66, 361.1) * mm, "end": v(-251.66, 311.1) * mm});
            skLineSegment(sketch, "E2.3.21.1", {"start": v(-301.66, 311.1) * mm, "end": v(-251.66, 311.1) * mm});
            skLineSegment(sketch, "E2.3.21.2", {"start": v(-301.66, 361.1) * mm, "end": v(-301.66, 311.1) * mm});
            skLineSegment(sketch, "E2.3.21.3", {"start": v(-301.66, 361.1) * mm, "end": v(-251.66, 361.1) * mm});
            skLineSegment(sketch, "E2.3.22.0", {"start": v(-251.66, 301.1) * mm, "end": v(-251.66, 251.1) * mm});
            skLineSegment(sketch, "E2.3.22.1", {"start": v(-301.66, 251.1) * mm, "end": v(-251.66, 251.1) * mm});
            skLineSegment(sketch, "E2.3.22.2", {"start": v(-301.66, 301.1) * mm, "end": v(-301.66, 251.1) * mm});
            skLineSegment(sketch, "E2.3.22.3", {"start": v(-301.66, 301.1) * mm, "end": v(-251.66, 301.1) * mm});
            skLineSegment(sketch, "E2.3.23.0", {"start": v(-251.66, 241.1) * mm, "end": v(-251.66, 191.1) * mm});
            skLineSegment(sketch, "E2.3.23.1", {"start": v(-301.66, 191.1) * mm, "end": v(-251.66, 191.1) * mm});
            skLineSegment(sketch, "E2.3.23.2", {"start": v(-301.66, 241.1) * mm, "end": v(-301.66, 191.1) * mm});
            skLineSegment(sketch, "E2.3.23.3", {"start": v(-301.66, 241.1) * mm, "end": v(-251.66, 241.1) * mm});
            skLineSegment(sketch, "E2.3.24.0", {"start": v(-251.66, 181.1) * mm, "end": v(-251.66, 131.1) * mm});
            skLineSegment(sketch, "E2.3.24.1", {"start": v(-301.66, 131.1) * mm, "end": v(-251.66, 131.1) * mm});
            skLineSegment(sketch, "E2.3.24.2", {"start": v(-301.66, 181.1) * mm, "end": v(-301.66, 131.1) * mm});
            skLineSegment(sketch, "E2.3.24.3", {"start": v(-301.66, 181.1) * mm, "end": v(-251.66, 181.1) * mm});
            skLineSegment(sketch, "E2.3.25.0", {"start": v(-251.66, 121.1) * mm, "end": v(-251.66, 71.1) * mm});
            skLineSegment(sketch, "E2.3.25.1", {"start": v(-301.66, 71.1) * mm, "end": v(-251.66, 71.1) * mm});
            skLineSegment(sketch, "E2.3.25.2", {"start": v(-301.66, 121.1) * mm, "end": v(-301.66, 71.1) * mm});
            skLineSegment(sketch, "E2.3.25.3", {"start": v(-301.66, 121.1) * mm, "end": v(-251.66, 121.1) * mm});
            skLineSegment(sketch, "E2.3.26.0", {"start": v(-251.66, 61.1) * mm, "end": v(-251.66, 11.1) * mm});
            skLineSegment(sketch, "E2.3.26.1", {"start": v(-301.66, 11.1) * mm, "end": v(-251.66, 11.1) * mm});
            skLineSegment(sketch, "E2.3.26.2", {"start": v(-301.66, 61.1) * mm, "end": v(-301.66, 11.1) * mm});
            skLineSegment(sketch, "E2.3.26.3", {"start": v(-301.66, 61.1) * mm, "end": v(-251.66, 61.1) * mm});
            skLineSegment(sketch, "E2.3.27.0", {"start": v(-251.66, 1.1) * mm, "end": v(-251.66, -48.9) * mm});
            skLineSegment(sketch, "E2.3.27.1", {"start": v(-301.66, -48.9) * mm, "end": v(-251.66, -48.9) * mm});
            skLineSegment(sketch, "E2.3.27.2", {"start": v(-301.66, 1.1) * mm, "end": v(-301.66, -48.9) * mm});
            skLineSegment(sketch, "E2.3.27.3", {"start": v(-301.66, 1.1) * mm, "end": v(-251.66, 1.1) * mm});
            skLineSegment(sketch, "E2.3.28.0", {"start": v(-251.66, -58.9) * mm, "end": v(-251.66, -108.9) * mm});
            skLineSegment(sketch, "E2.3.28.1", {"start": v(-301.66, -108.9) * mm, "end": v(-251.66, -108.9) * mm});
            skLineSegment(sketch, "E2.3.28.2", {"start": v(-301.66, -58.9) * mm, "end": v(-301.66, -108.9) * mm});
            skLineSegment(sketch, "E2.3.28.3", {"start": v(-301.66, -58.9) * mm, "end": v(-251.66, -58.9) * mm});
            skLineSegment(sketch, "E2.3.29.0", {"start": v(-251.66, -118.9) * mm, "end": v(-251.66, -168.9) * mm});
            skLineSegment(sketch, "E2.3.29.1", {"start": v(-301.66, -168.9) * mm, "end": v(-251.66, -168.9) * mm});
            skLineSegment(sketch, "E2.3.29.2", {"start": v(-301.66, -118.9) * mm, "end": v(-301.66, -168.9) * mm});
            skLineSegment(sketch, "E2.3.29.3", {"start": v(-301.66, -118.9) * mm, "end": v(-251.66, -118.9) * mm});
            skLineSegment(sketch, "E2.3.30.0", {"start": v(-251.66, -178.9) * mm, "end": v(-251.66, -228.9) * mm});
            skLineSegment(sketch, "E2.3.30.1", {"start": v(-301.66, -228.9) * mm, "end": v(-251.66, -228.9) * mm});
            skLineSegment(sketch, "E2.3.30.2", {"start": v(-301.66, -178.9) * mm, "end": v(-301.66, -228.9) * mm});
            skLineSegment(sketch, "E2.3.30.3", {"start": v(-301.66, -178.9) * mm, "end": v(-251.66, -178.9) * mm});
            skLineSegment(sketch, "E2.3.31.0", {"start": v(-251.66, -238.9) * mm, "end": v(-251.66, -288.9) * mm});
            skLineSegment(sketch, "E2.3.31.1", {"start": v(-301.66, -288.9) * mm, "end": v(-251.66, -288.9) * mm});
            skLineSegment(sketch, "E2.3.31.2", {"start": v(-301.66, -238.9) * mm, "end": v(-301.66, -288.9) * mm});
            skLineSegment(sketch, "E2.3.31.3", {"start": v(-301.66, -238.9) * mm, "end": v(-251.66, -238.9) * mm});
            skLineSegment(sketch, "E2.3.32.0", {"start": v(-251.66, -298.9) * mm, "end": v(-251.66, -348.9) * mm});
            skLineSegment(sketch, "E2.3.32.1", {"start": v(-301.66, -348.9) * mm, "end": v(-251.66, -348.9) * mm});
            skLineSegment(sketch, "E2.3.32.2", {"start": v(-301.66, -298.9) * mm, "end": v(-301.66, -348.9) * mm});
            skLineSegment(sketch, "E2.3.32.3", {"start": v(-301.66, -298.9) * mm, "end": v(-251.66, -298.9) * mm});
            skLineSegment(sketch, "E2.4.0.0", {"start": v(-191.66, 1621.1) * mm, "end": v(-191.66, 1571.1) * mm});
            skLineSegment(sketch, "E2.4.0.1", {"start": v(-241.66, 1571.1) * mm, "end": v(-191.66, 1571.1) * mm});
            skLineSegment(sketch, "E2.4.0.2", {"start": v(-241.66, 1621.1) * mm, "end": v(-241.66, 1571.1) * mm});
            skLineSegment(sketch, "E2.4.0.3", {"start": v(-241.66, 1621.1) * mm, "end": v(-191.66, 1621.1) * mm});
            skLineSegment(sketch, "E2.4.1.0", {"start": v(-191.66, 1561.1) * mm, "end": v(-191.66, 1511.1) * mm});
            skLineSegment(sketch, "E2.4.1.1", {"start": v(-241.66, 1511.1) * mm, "end": v(-191.66, 1511.1) * mm});
            skLineSegment(sketch, "E2.4.1.2", {"start": v(-241.66, 1561.1) * mm, "end": v(-241.66, 1511.1) * mm});
            skLineSegment(sketch, "E2.4.1.3", {"start": v(-241.66, 1561.1) * mm, "end": v(-191.66, 1561.1) * mm});
            skLineSegment(sketch, "E2.4.2.0", {"start": v(-191.66, 1501.1) * mm, "end": v(-191.66, 1451.1) * mm});
            skLineSegment(sketch, "E2.4.2.1", {"start": v(-241.66, 1451.1) * mm, "end": v(-191.66, 1451.1) * mm});
            skLineSegment(sketch, "E2.4.2.2", {"start": v(-241.66, 1501.1) * mm, "end": v(-241.66, 1451.1) * mm});
            skLineSegment(sketch, "E2.4.2.3", {"start": v(-241.66, 1501.1) * mm, "end": v(-191.66, 1501.1) * mm});
            skLineSegment(sketch, "E2.4.3.0", {"start": v(-191.66, 1441.1) * mm, "end": v(-191.66, 1391.1) * mm});
            skLineSegment(sketch, "E2.4.3.1", {"start": v(-241.66, 1391.1) * mm, "end": v(-191.66, 1391.1) * mm});
            skLineSegment(sketch, "E2.4.3.2", {"start": v(-241.66, 1441.1) * mm, "end": v(-241.66, 1391.1) * mm});
            skLineSegment(sketch, "E2.4.3.3", {"start": v(-241.66, 1441.1) * mm, "end": v(-191.66, 1441.1) * mm});
            skLineSegment(sketch, "E2.4.4.0", {"start": v(-191.66, 1381.1) * mm, "end": v(-191.66, 1331.1) * mm});
            skLineSegment(sketch, "E2.4.4.1", {"start": v(-241.66, 1331.1) * mm, "end": v(-191.66, 1331.1) * mm});
            skLineSegment(sketch, "E2.4.4.2", {"start": v(-241.66, 1381.1) * mm, "end": v(-241.66, 1331.1) * mm});
            skLineSegment(sketch, "E2.4.4.3", {"start": v(-241.66, 1381.1) * mm, "end": v(-191.66, 1381.1) * mm});
            skLineSegment(sketch, "E2.4.5.0", {"start": v(-191.66, 1321.1) * mm, "end": v(-191.66, 1271.1) * mm});
            skLineSegment(sketch, "E2.4.5.1", {"start": v(-241.66, 1271.1) * mm, "end": v(-191.66, 1271.1) * mm});
            skLineSegment(sketch, "E2.4.5.2", {"start": v(-241.66, 1321.1) * mm, "end": v(-241.66, 1271.1) * mm});
            skLineSegment(sketch, "E2.4.5.3", {"start": v(-241.66, 1321.1) * mm, "end": v(-191.66, 1321.1) * mm});
            skLineSegment(sketch, "E2.4.6.0", {"start": v(-191.66, 1261.1) * mm, "end": v(-191.66, 1211.1) * mm});
            skLineSegment(sketch, "E2.4.6.1", {"start": v(-241.66, 1211.1) * mm, "end": v(-191.66, 1211.1) * mm});
            skLineSegment(sketch, "E2.4.6.2", {"start": v(-241.66, 1261.1) * mm, "end": v(-241.66, 1211.1) * mm});
            skLineSegment(sketch, "E2.4.6.3", {"start": v(-241.66, 1261.1) * mm, "end": v(-191.66, 1261.1) * mm});
            skLineSegment(sketch, "E2.4.7.0", {"start": v(-191.66, 1201.1) * mm, "end": v(-191.66, 1151.1) * mm});
            skLineSegment(sketch, "E2.4.7.1", {"start": v(-241.66, 1151.1) * mm, "end": v(-191.66, 1151.1) * mm});
            skLineSegment(sketch, "E2.4.7.2", {"start": v(-241.66, 1201.1) * mm, "end": v(-241.66, 1151.1) * mm});
            skLineSegment(sketch, "E2.4.7.3", {"start": v(-241.66, 1201.1) * mm, "end": v(-191.66, 1201.1) * mm});
            skLineSegment(sketch, "E2.4.8.0", {"start": v(-191.66, 1141.1) * mm, "end": v(-191.66, 1091.1) * mm});
            skLineSegment(sketch, "E2.4.8.1", {"start": v(-241.66, 1091.1) * mm, "end": v(-191.66, 1091.1) * mm});
            skLineSegment(sketch, "E2.4.8.2", {"start": v(-241.66, 1141.1) * mm, "end": v(-241.66, 1091.1) * mm});
            skLineSegment(sketch, "E2.4.8.3", {"start": v(-241.66, 1141.1) * mm, "end": v(-191.66, 1141.1) * mm});
            skLineSegment(sketch, "E2.4.9.0", {"start": v(-191.66, 1081.1) * mm, "end": v(-191.66, 1031.1) * mm});
            skLineSegment(sketch, "E2.4.9.1", {"start": v(-241.66, 1031.1) * mm, "end": v(-191.66, 1031.1) * mm});
            skLineSegment(sketch, "E2.4.9.2", {"start": v(-241.66, 1081.1) * mm, "end": v(-241.66, 1031.1) * mm});
            skLineSegment(sketch, "E2.4.9.3", {"start": v(-241.66, 1081.1) * mm, "end": v(-191.66, 1081.1) * mm});
            skLineSegment(sketch, "E2.4.10.0", {"start": v(-191.66, 1021.1) * mm, "end": v(-191.66, 971.1) * mm});
            skLineSegment(sketch, "E2.4.10.1", {"start": v(-241.66, 971.1) * mm, "end": v(-191.66, 971.1) * mm});
            skLineSegment(sketch, "E2.4.10.2", {"start": v(-241.66, 1021.1) * mm, "end": v(-241.66, 971.1) * mm});
            skLineSegment(sketch, "E2.4.10.3", {"start": v(-241.66, 1021.1) * mm, "end": v(-191.66, 1021.1) * mm});
            skLineSegment(sketch, "E2.4.11.0", {"start": v(-191.66, 961.1) * mm, "end": v(-191.66, 911.1) * mm});
            skLineSegment(sketch, "E2.4.11.1", {"start": v(-241.66, 911.1) * mm, "end": v(-191.66, 911.1) * mm});
            skLineSegment(sketch, "E2.4.11.2", {"start": v(-241.66, 961.1) * mm, "end": v(-241.66, 911.1) * mm});
            skLineSegment(sketch, "E2.4.11.3", {"start": v(-241.66, 961.1) * mm, "end": v(-191.66, 961.1) * mm});
            skLineSegment(sketch, "E2.4.12.0", {"start": v(-191.66, 901.1) * mm, "end": v(-191.66, 851.1) * mm});
            skLineSegment(sketch, "E2.4.12.1", {"start": v(-241.66, 851.1) * mm, "end": v(-191.66, 851.1) * mm});
            skLineSegment(sketch, "E2.4.12.2", {"start": v(-241.66, 901.1) * mm, "end": v(-241.66, 851.1) * mm});
            skLineSegment(sketch, "E2.4.12.3", {"start": v(-241.66, 901.1) * mm, "end": v(-191.66, 901.1) * mm});
            skLineSegment(sketch, "E2.4.13.0", {"start": v(-191.66, 841.1) * mm, "end": v(-191.66, 791.1) * mm});
            skLineSegment(sketch, "E2.4.13.1", {"start": v(-241.66, 791.1) * mm, "end": v(-191.66, 791.1) * mm});
            skLineSegment(sketch, "E2.4.13.2", {"start": v(-241.66, 841.1) * mm, "end": v(-241.66, 791.1) * mm});
            skLineSegment(sketch, "E2.4.13.3", {"start": v(-241.66, 841.1) * mm, "end": v(-191.66, 841.1) * mm});
            skLineSegment(sketch, "E2.4.14.0", {"start": v(-191.66, 781.1) * mm, "end": v(-191.66, 731.1) * mm});
            skLineSegment(sketch, "E2.4.14.1", {"start": v(-241.66, 731.1) * mm, "end": v(-191.66, 731.1) * mm});
            skLineSegment(sketch, "E2.4.14.2", {"start": v(-241.66, 781.1) * mm, "end": v(-241.66, 731.1) * mm});
            skLineSegment(sketch, "E2.4.14.3", {"start": v(-241.66, 781.1) * mm, "end": v(-191.66, 781.1) * mm});
            skLineSegment(sketch, "E2.4.15.0", {"start": v(-191.66, 721.1) * mm, "end": v(-191.66, 671.1) * mm});
            skLineSegment(sketch, "E2.4.15.1", {"start": v(-241.66, 671.1) * mm, "end": v(-191.66, 671.1) * mm});
            skLineSegment(sketch, "E2.4.15.2", {"start": v(-241.66, 721.1) * mm, "end": v(-241.66, 671.1) * mm});
            skLineSegment(sketch, "E2.4.15.3", {"start": v(-241.66, 721.1) * mm, "end": v(-191.66, 721.1) * mm});
            skLineSegment(sketch, "E2.4.16.0", {"start": v(-191.66, 661.1) * mm, "end": v(-191.66, 611.1) * mm});
            skLineSegment(sketch, "E2.4.16.1", {"start": v(-241.66, 611.1) * mm, "end": v(-191.66, 611.1) * mm});
            skLineSegment(sketch, "E2.4.16.2", {"start": v(-241.66, 661.1) * mm, "end": v(-241.66, 611.1) * mm});
            skLineSegment(sketch, "E2.4.16.3", {"start": v(-241.66, 661.1) * mm, "end": v(-191.66, 661.1) * mm});
            skLineSegment(sketch, "E2.4.17.0", {"start": v(-191.66, 601.1) * mm, "end": v(-191.66, 551.1) * mm});
            skLineSegment(sketch, "E2.4.17.1", {"start": v(-241.66, 551.1) * mm, "end": v(-191.66, 551.1) * mm});
            skLineSegment(sketch, "E2.4.17.2", {"start": v(-241.66, 601.1) * mm, "end": v(-241.66, 551.1) * mm});
            skLineSegment(sketch, "E2.4.17.3", {"start": v(-241.66, 601.1) * mm, "end": v(-191.66, 601.1) * mm});
            skLineSegment(sketch, "E2.4.18.0", {"start": v(-191.66, 541.1) * mm, "end": v(-191.66, 491.1) * mm});
            skLineSegment(sketch, "E2.4.18.1", {"start": v(-241.66, 491.1) * mm, "end": v(-191.66, 491.1) * mm});
            skLineSegment(sketch, "E2.4.18.2", {"start": v(-241.66, 541.1) * mm, "end": v(-241.66, 491.1) * mm});
            skLineSegment(sketch, "E2.4.18.3", {"start": v(-241.66, 541.1) * mm, "end": v(-191.66, 541.1) * mm});
            skLineSegment(sketch, "E2.4.19.0", {"start": v(-191.66, 481.1) * mm, "end": v(-191.66, 431.1) * mm});
            skLineSegment(sketch, "E2.4.19.1", {"start": v(-241.66, 431.1) * mm, "end": v(-191.66, 431.1) * mm});
            skLineSegment(sketch, "E2.4.19.2", {"start": v(-241.66, 481.1) * mm, "end": v(-241.66, 431.1) * mm});
            skLineSegment(sketch, "E2.4.19.3", {"start": v(-241.66, 481.1) * mm, "end": v(-191.66, 481.1) * mm});
            skLineSegment(sketch, "E2.4.20.0", {"start": v(-191.66, 421.1) * mm, "end": v(-191.66, 371.1) * mm});
            skLineSegment(sketch, "E2.4.20.1", {"start": v(-241.66, 371.1) * mm, "end": v(-191.66, 371.1) * mm});
            skLineSegment(sketch, "E2.4.20.2", {"start": v(-241.66, 421.1) * mm, "end": v(-241.66, 371.1) * mm});
            skLineSegment(sketch, "E2.4.20.3", {"start": v(-241.66, 421.1) * mm, "end": v(-191.66, 421.1) * mm});
            skLineSegment(sketch, "E2.4.21.0", {"start": v(-191.66, 361.1) * mm, "end": v(-191.66, 311.1) * mm});
            skLineSegment(sketch, "E2.4.21.1", {"start": v(-241.66, 311.1) * mm, "end": v(-191.66, 311.1) * mm});
            skLineSegment(sketch, "E2.4.21.2", {"start": v(-241.66, 361.1) * mm, "end": v(-241.66, 311.1) * mm});
            skLineSegment(sketch, "E2.4.21.3", {"start": v(-241.66, 361.1) * mm, "end": v(-191.66, 361.1) * mm});
            skLineSegment(sketch, "E2.4.22.0", {"start": v(-191.66, 301.1) * mm, "end": v(-191.66, 251.1) * mm});
            skLineSegment(sketch, "E2.4.22.1", {"start": v(-241.66, 251.1) * mm, "end": v(-191.66, 251.1) * mm});
            skLineSegment(sketch, "E2.4.22.2", {"start": v(-241.66, 301.1) * mm, "end": v(-241.66, 251.1) * mm});
            skLineSegment(sketch, "E2.4.22.3", {"start": v(-241.66, 301.1) * mm, "end": v(-191.66, 301.1) * mm});
            skLineSegment(sketch, "E2.4.23.0", {"start": v(-191.66, 241.1) * mm, "end": v(-191.66, 191.1) * mm});
            skLineSegment(sketch, "E2.4.23.1", {"start": v(-241.66, 191.1) * mm, "end": v(-191.66, 191.1) * mm});
            skLineSegment(sketch, "E2.4.23.2", {"start": v(-241.66, 241.1) * mm, "end": v(-241.66, 191.1) * mm});
            skLineSegment(sketch, "E2.4.23.3", {"start": v(-241.66, 241.1) * mm, "end": v(-191.66, 241.1) * mm});
            skLineSegment(sketch, "E2.4.24.0", {"start": v(-191.66, 181.1) * mm, "end": v(-191.66, 131.1) * mm});
            skLineSegment(sketch, "E2.4.24.1", {"start": v(-241.66, 131.1) * mm, "end": v(-191.66, 131.1) * mm});
            skLineSegment(sketch, "E2.4.24.2", {"start": v(-241.66, 181.1) * mm, "end": v(-241.66, 131.1) * mm});
            skLineSegment(sketch, "E2.4.24.3", {"start": v(-241.66, 181.1) * mm, "end": v(-191.66, 181.1) * mm});
            skLineSegment(sketch, "E2.4.25.0", {"start": v(-191.66, 121.1) * mm, "end": v(-191.66, 71.1) * mm});
            skLineSegment(sketch, "E2.4.25.1", {"start": v(-241.66, 71.1) * mm, "end": v(-191.66, 71.1) * mm});
            skLineSegment(sketch, "E2.4.25.2", {"start": v(-241.66, 121.1) * mm, "end": v(-241.66, 71.1) * mm});
            skLineSegment(sketch, "E2.4.25.3", {"start": v(-241.66, 121.1) * mm, "end": v(-191.66, 121.1) * mm});
            skLineSegment(sketch, "E2.4.26.0", {"start": v(-191.66, 61.1) * mm, "end": v(-191.66, 11.1) * mm});
            skLineSegment(sketch, "E2.4.26.1", {"start": v(-241.66, 11.1) * mm, "end": v(-191.66, 11.1) * mm});
            skLineSegment(sketch, "E2.4.26.2", {"start": v(-241.66, 61.1) * mm, "end": v(-241.66, 11.1) * mm});
            skLineSegment(sketch, "E2.4.26.3", {"start": v(-241.66, 61.1) * mm, "end": v(-191.66, 61.1) * mm});
            skLineSegment(sketch, "E2.4.27.0", {"start": v(-191.66, 1.1) * mm, "end": v(-191.66, -48.9) * mm});
            skLineSegment(sketch, "E2.4.27.1", {"start": v(-241.66, -48.9) * mm, "end": v(-191.66, -48.9) * mm});
            skLineSegment(sketch, "E2.4.27.2", {"start": v(-241.66, 1.1) * mm, "end": v(-241.66, -48.9) * mm});
            skLineSegment(sketch, "E2.4.27.3", {"start": v(-241.66, 1.1) * mm, "end": v(-191.66, 1.1) * mm});
            skLineSegment(sketch, "E2.4.28.0", {"start": v(-191.66, -58.9) * mm, "end": v(-191.66, -108.9) * mm});
            skLineSegment(sketch, "E2.4.28.1", {"start": v(-241.66, -108.9) * mm, "end": v(-191.66, -108.9) * mm});
            skLineSegment(sketch, "E2.4.28.2", {"start": v(-241.66, -58.9) * mm, "end": v(-241.66, -108.9) * mm});
            skLineSegment(sketch, "E2.4.28.3", {"start": v(-241.66, -58.9) * mm, "end": v(-191.66, -58.9) * mm});
            skLineSegment(sketch, "E2.4.29.0", {"start": v(-191.66, -118.9) * mm, "end": v(-191.66, -168.9) * mm});
            skLineSegment(sketch, "E2.4.29.1", {"start": v(-241.66, -168.9) * mm, "end": v(-191.66, -168.9) * mm});
            skLineSegment(sketch, "E2.4.29.2", {"start": v(-241.66, -118.9) * mm, "end": v(-241.66, -168.9) * mm});
            skLineSegment(sketch, "E2.4.29.3", {"start": v(-241.66, -118.9) * mm, "end": v(-191.66, -118.9) * mm});
            skLineSegment(sketch, "E2.4.30.0", {"start": v(-191.66, -178.9) * mm, "end": v(-191.66, -228.9) * mm});
            skLineSegment(sketch, "E2.4.30.1", {"start": v(-241.66, -228.9) * mm, "end": v(-191.66, -228.9) * mm});
            skLineSegment(sketch, "E2.4.30.2", {"start": v(-241.66, -178.9) * mm, "end": v(-241.66, -228.9) * mm});
            skLineSegment(sketch, "E2.4.30.3", {"start": v(-241.66, -178.9) * mm, "end": v(-191.66, -178.9) * mm});
            skLineSegment(sketch, "E2.4.31.0", {"start": v(-191.66, -238.9) * mm, "end": v(-191.66, -288.9) * mm});
            skLineSegment(sketch, "E2.4.31.1", {"start": v(-241.66, -288.9) * mm, "end": v(-191.66, -288.9) * mm});
            skLineSegment(sketch, "E2.4.31.2", {"start": v(-241.66, -238.9) * mm, "end": v(-241.66, -288.9) * mm});
            skLineSegment(sketch, "E2.4.31.3", {"start": v(-241.66, -238.9) * mm, "end": v(-191.66, -238.9) * mm});
            skLineSegment(sketch, "E2.4.32.0", {"start": v(-191.66, -298.9) * mm, "end": v(-191.66, -348.9) * mm});
            skLineSegment(sketch, "E2.4.32.1", {"start": v(-241.66, -348.9) * mm, "end": v(-191.66, -348.9) * mm});
            skLineSegment(sketch, "E2.4.32.2", {"start": v(-241.66, -298.9) * mm, "end": v(-241.66, -348.9) * mm});
            skLineSegment(sketch, "E2.4.32.3", {"start": v(-241.66, -298.9) * mm, "end": v(-191.66, -298.9) * mm});
            skLineSegment(sketch, "E2.5.0.0", {"start": v(-131.66, 1621.1) * mm, "end": v(-131.66, 1571.1) * mm});
            skLineSegment(sketch, "E2.5.0.1", {"start": v(-181.66, 1571.1) * mm, "end": v(-131.66, 1571.1) * mm});
            skLineSegment(sketch, "E2.5.0.2", {"start": v(-181.66, 1621.1) * mm, "end": v(-181.66, 1571.1) * mm});
            skLineSegment(sketch, "E2.5.0.3", {"start": v(-181.66, 1621.1) * mm, "end": v(-131.66, 1621.1) * mm});
            skLineSegment(sketch, "E2.5.1.0", {"start": v(-131.66, 1561.1) * mm, "end": v(-131.66, 1511.1) * mm});
            skLineSegment(sketch, "E2.5.1.1", {"start": v(-181.66, 1511.1) * mm, "end": v(-131.66, 1511.1) * mm});
            skLineSegment(sketch, "E2.5.1.2", {"start": v(-181.66, 1561.1) * mm, "end": v(-181.66, 1511.1) * mm});
            skLineSegment(sketch, "E2.5.1.3", {"start": v(-181.66, 1561.1) * mm, "end": v(-131.66, 1561.1) * mm});
            skLineSegment(sketch, "E2.5.2.0", {"start": v(-131.66, 1501.1) * mm, "end": v(-131.66, 1451.1) * mm});
            skLineSegment(sketch, "E2.5.2.1", {"start": v(-181.66, 1451.1) * mm, "end": v(-131.66, 1451.1) * mm});
            skLineSegment(sketch, "E2.5.2.2", {"start": v(-181.66, 1501.1) * mm, "end": v(-181.66, 1451.1) * mm});
            skLineSegment(sketch, "E2.5.2.3", {"start": v(-181.66, 1501.1) * mm, "end": v(-131.66, 1501.1) * mm});
            skLineSegment(sketch, "E2.5.3.0", {"start": v(-131.66, 1441.1) * mm, "end": v(-131.66, 1391.1) * mm});
            skLineSegment(sketch, "E2.5.3.1", {"start": v(-181.66, 1391.1) * mm, "end": v(-131.66, 1391.1) * mm});
            skLineSegment(sketch, "E2.5.3.2", {"start": v(-181.66, 1441.1) * mm, "end": v(-181.66, 1391.1) * mm});
            skLineSegment(sketch, "E2.5.3.3", {"start": v(-181.66, 1441.1) * mm, "end": v(-131.66, 1441.1) * mm});
            skLineSegment(sketch, "E2.5.4.0", {"start": v(-131.66, 1381.1) * mm, "end": v(-131.66, 1331.1) * mm});
            skLineSegment(sketch, "E2.5.4.1", {"start": v(-181.66, 1331.1) * mm, "end": v(-131.66, 1331.1) * mm});
            skLineSegment(sketch, "E2.5.4.2", {"start": v(-181.66, 1381.1) * mm, "end": v(-181.66, 1331.1) * mm});
            skLineSegment(sketch, "E2.5.4.3", {"start": v(-181.66, 1381.1) * mm, "end": v(-131.66, 1381.1) * mm});
            skLineSegment(sketch, "E2.5.5.0", {"start": v(-131.66, 1321.1) * mm, "end": v(-131.66, 1271.1) * mm});
            skLineSegment(sketch, "E2.5.5.1", {"start": v(-181.66, 1271.1) * mm, "end": v(-131.66, 1271.1) * mm});
            skLineSegment(sketch, "E2.5.5.2", {"start": v(-181.66, 1321.1) * mm, "end": v(-181.66, 1271.1) * mm});
            skLineSegment(sketch, "E2.5.5.3", {"start": v(-181.66, 1321.1) * mm, "end": v(-131.66, 1321.1) * mm});
            skLineSegment(sketch, "E2.5.6.0", {"start": v(-131.66, 1261.1) * mm, "end": v(-131.66, 1211.1) * mm});
            skLineSegment(sketch, "E2.5.6.1", {"start": v(-181.66, 1211.1) * mm, "end": v(-131.66, 1211.1) * mm});
            skLineSegment(sketch, "E2.5.6.2", {"start": v(-181.66, 1261.1) * mm, "end": v(-181.66, 1211.1) * mm});
            skLineSegment(sketch, "E2.5.6.3", {"start": v(-181.66, 1261.1) * mm, "end": v(-131.66, 1261.1) * mm});
            skLineSegment(sketch, "E2.5.7.0", {"start": v(-131.66, 1201.1) * mm, "end": v(-131.66, 1151.1) * mm});
            skLineSegment(sketch, "E2.5.7.1", {"start": v(-181.66, 1151.1) * mm, "end": v(-131.66, 1151.1) * mm});
            skLineSegment(sketch, "E2.5.7.2", {"start": v(-181.66, 1201.1) * mm, "end": v(-181.66, 1151.1) * mm});
            skLineSegment(sketch, "E2.5.7.3", {"start": v(-181.66, 1201.1) * mm, "end": v(-131.66, 1201.1) * mm});
            skLineSegment(sketch, "E2.5.8.0", {"start": v(-131.66, 1141.1) * mm, "end": v(-131.66, 1091.1) * mm});
            skLineSegment(sketch, "E2.5.8.1", {"start": v(-181.66, 1091.1) * mm, "end": v(-131.66, 1091.1) * mm});
            skLineSegment(sketch, "E2.5.8.2", {"start": v(-181.66, 1141.1) * mm, "end": v(-181.66, 1091.1) * mm});
            skLineSegment(sketch, "E2.5.8.3", {"start": v(-181.66, 1141.1) * mm, "end": v(-131.66, 1141.1) * mm});
            skLineSegment(sketch, "E2.5.9.0", {"start": v(-131.66, 1081.1) * mm, "end": v(-131.66, 1031.1) * mm});
            skLineSegment(sketch, "E2.5.9.1", {"start": v(-181.66, 1031.1) * mm, "end": v(-131.66, 1031.1) * mm});
            skLineSegment(sketch, "E2.5.9.2", {"start": v(-181.66, 1081.1) * mm, "end": v(-181.66, 1031.1) * mm});
            skLineSegment(sketch, "E2.5.9.3", {"start": v(-181.66, 1081.1) * mm, "end": v(-131.66, 1081.1) * mm});
            skLineSegment(sketch, "E2.5.10.0", {"start": v(-131.66, 1021.1) * mm, "end": v(-131.66, 971.1) * mm});
            skLineSegment(sketch, "E2.5.10.1", {"start": v(-181.66, 971.1) * mm, "end": v(-131.66, 971.1) * mm});
            skLineSegment(sketch, "E2.5.10.2", {"start": v(-181.66, 1021.1) * mm, "end": v(-181.66, 971.1) * mm});
            skLineSegment(sketch, "E2.5.10.3", {"start": v(-181.66, 1021.1) * mm, "end": v(-131.66, 1021.1) * mm});
            skLineSegment(sketch, "E2.5.11.0", {"start": v(-131.66, 961.1) * mm, "end": v(-131.66, 911.1) * mm});
            skLineSegment(sketch, "E2.5.11.1", {"start": v(-181.66, 911.1) * mm, "end": v(-131.66, 911.1) * mm});
            skLineSegment(sketch, "E2.5.11.2", {"start": v(-181.66, 961.1) * mm, "end": v(-181.66, 911.1) * mm});
            skLineSegment(sketch, "E2.5.11.3", {"start": v(-181.66, 961.1) * mm, "end": v(-131.66, 961.1) * mm});
            skLineSegment(sketch, "E2.5.12.0", {"start": v(-131.66, 901.1) * mm, "end": v(-131.66, 851.1) * mm});
            skLineSegment(sketch, "E2.5.12.1", {"start": v(-181.66, 851.1) * mm, "end": v(-131.66, 851.1) * mm});
            skLineSegment(sketch, "E2.5.12.2", {"start": v(-181.66, 901.1) * mm, "end": v(-181.66, 851.1) * mm});
            skLineSegment(sketch, "E2.5.12.3", {"start": v(-181.66, 901.1) * mm, "end": v(-131.66, 901.1) * mm});
            skLineSegment(sketch, "E2.5.13.0", {"start": v(-131.66, 841.1) * mm, "end": v(-131.66, 791.1) * mm});
            skLineSegment(sketch, "E2.5.13.1", {"start": v(-181.66, 791.1) * mm, "end": v(-131.66, 791.1) * mm});
            skLineSegment(sketch, "E2.5.13.2", {"start": v(-181.66, 841.1) * mm, "end": v(-181.66, 791.1) * mm});
            skLineSegment(sketch, "E2.5.13.3", {"start": v(-181.66, 841.1) * mm, "end": v(-131.66, 841.1) * mm});
            skLineSegment(sketch, "E2.5.14.0", {"start": v(-131.66, 781.1) * mm, "end": v(-131.66, 731.1) * mm});
            skLineSegment(sketch, "E2.5.14.1", {"start": v(-181.66, 731.1) * mm, "end": v(-131.66, 731.1) * mm});
            skLineSegment(sketch, "E2.5.14.2", {"start": v(-181.66, 781.1) * mm, "end": v(-181.66, 731.1) * mm});
            skLineSegment(sketch, "E2.5.14.3", {"start": v(-181.66, 781.1) * mm, "end": v(-131.66, 781.1) * mm});
            skLineSegment(sketch, "E2.5.15.0", {"start": v(-131.66, 721.1) * mm, "end": v(-131.66, 671.1) * mm});
            skLineSegment(sketch, "E2.5.15.1", {"start": v(-181.66, 671.1) * mm, "end": v(-131.66, 671.1) * mm});
            skLineSegment(sketch, "E2.5.15.2", {"start": v(-181.66, 721.1) * mm, "end": v(-181.66, 671.1) * mm});
            skLineSegment(sketch, "E2.5.15.3", {"start": v(-181.66, 721.1) * mm, "end": v(-131.66, 721.1) * mm});
            skLineSegment(sketch, "E2.5.16.0", {"start": v(-131.66, 661.1) * mm, "end": v(-131.66, 611.1) * mm});
            skLineSegment(sketch, "E2.5.16.1", {"start": v(-181.66, 611.1) * mm, "end": v(-131.66, 611.1) * mm});
            skLineSegment(sketch, "E2.5.16.2", {"start": v(-181.66, 661.1) * mm, "end": v(-181.66, 611.1) * mm});
            skLineSegment(sketch, "E2.5.16.3", {"start": v(-181.66, 661.1) * mm, "end": v(-131.66, 661.1) * mm});
            skLineSegment(sketch, "E2.5.17.0", {"start": v(-131.66, 601.1) * mm, "end": v(-131.66, 551.1) * mm});
            skLineSegment(sketch, "E2.5.17.1", {"start": v(-181.66, 551.1) * mm, "end": v(-131.66, 551.1) * mm});
            skLineSegment(sketch, "E2.5.17.2", {"start": v(-181.66, 601.1) * mm, "end": v(-181.66, 551.1) * mm});
            skLineSegment(sketch, "E2.5.17.3", {"start": v(-181.66, 601.1) * mm, "end": v(-131.66, 601.1) * mm});
            skLineSegment(sketch, "E2.5.18.0", {"start": v(-131.66, 541.1) * mm, "end": v(-131.66, 491.1) * mm});
            skLineSegment(sketch, "E2.5.18.1", {"start": v(-181.66, 491.1) * mm, "end": v(-131.66, 491.1) * mm});
            skLineSegment(sketch, "E2.5.18.2", {"start": v(-181.66, 541.1) * mm, "end": v(-181.66, 491.1) * mm});
            skLineSegment(sketch, "E2.5.18.3", {"start": v(-181.66, 541.1) * mm, "end": v(-131.66, 541.1) * mm});
            skLineSegment(sketch, "E2.5.19.0", {"start": v(-131.66, 481.1) * mm, "end": v(-131.66, 431.1) * mm});
            skLineSegment(sketch, "E2.5.19.1", {"start": v(-181.66, 431.1) * mm, "end": v(-131.66, 431.1) * mm});
            skLineSegment(sketch, "E2.5.19.2", {"start": v(-181.66, 481.1) * mm, "end": v(-181.66, 431.1) * mm});
            skLineSegment(sketch, "E2.5.19.3", {"start": v(-181.66, 481.1) * mm, "end": v(-131.66, 481.1) * mm});
            skLineSegment(sketch, "E2.5.20.0", {"start": v(-131.66, 421.1) * mm, "end": v(-131.66, 371.1) * mm});
            skLineSegment(sketch, "E2.5.20.1", {"start": v(-181.66, 371.1) * mm, "end": v(-131.66, 371.1) * mm});
            skLineSegment(sketch, "E2.5.20.2", {"start": v(-181.66, 421.1) * mm, "end": v(-181.66, 371.1) * mm});
            skLineSegment(sketch, "E2.5.20.3", {"start": v(-181.66, 421.1) * mm, "end": v(-131.66, 421.1) * mm});
            skLineSegment(sketch, "E2.5.21.0", {"start": v(-131.66, 361.1) * mm, "end": v(-131.66, 311.1) * mm});
            skLineSegment(sketch, "E2.5.21.1", {"start": v(-181.66, 311.1) * mm, "end": v(-131.66, 311.1) * mm});
            skLineSegment(sketch, "E2.5.21.2", {"start": v(-181.66, 361.1) * mm, "end": v(-181.66, 311.1) * mm});
            skLineSegment(sketch, "E2.5.21.3", {"start": v(-181.66, 361.1) * mm, "end": v(-131.66, 361.1) * mm});
            skLineSegment(sketch, "E2.5.22.0", {"start": v(-131.66, 301.1) * mm, "end": v(-131.66, 251.1) * mm});
            skLineSegment(sketch, "E2.5.22.1", {"start": v(-181.66, 251.1) * mm, "end": v(-131.66, 251.1) * mm});
            skLineSegment(sketch, "E2.5.22.2", {"start": v(-181.66, 301.1) * mm, "end": v(-181.66, 251.1) * mm});
            skLineSegment(sketch, "E2.5.22.3", {"start": v(-181.66, 301.1) * mm, "end": v(-131.66, 301.1) * mm});
            skLineSegment(sketch, "E2.5.23.0", {"start": v(-131.66, 241.1) * mm, "end": v(-131.66, 191.1) * mm});
            skLineSegment(sketch, "E2.5.23.1", {"start": v(-181.66, 191.1) * mm, "end": v(-131.66, 191.1) * mm});
            skLineSegment(sketch, "E2.5.23.2", {"start": v(-181.66, 241.1) * mm, "end": v(-181.66, 191.1) * mm});
            skLineSegment(sketch, "E2.5.23.3", {"start": v(-181.66, 241.1) * mm, "end": v(-131.66, 241.1) * mm});
            skLineSegment(sketch, "E2.5.24.0", {"start": v(-131.66, 181.1) * mm, "end": v(-131.66, 131.1) * mm});
            skLineSegment(sketch, "E2.5.24.1", {"start": v(-181.66, 131.1) * mm, "end": v(-131.66, 131.1) * mm});
            skLineSegment(sketch, "E2.5.24.2", {"start": v(-181.66, 181.1) * mm, "end": v(-181.66, 131.1) * mm});
            skLineSegment(sketch, "E2.5.24.3", {"start": v(-181.66, 181.1) * mm, "end": v(-131.66, 181.1) * mm});
            skLineSegment(sketch, "E2.5.25.0", {"start": v(-131.66, 121.1) * mm, "end": v(-131.66, 71.1) * mm});
            skLineSegment(sketch, "E2.5.25.1", {"start": v(-181.66, 71.1) * mm, "end": v(-131.66, 71.1) * mm});
            skLineSegment(sketch, "E2.5.25.2", {"start": v(-181.66, 121.1) * mm, "end": v(-181.66, 71.1) * mm});
            skLineSegment(sketch, "E2.5.25.3", {"start": v(-181.66, 121.1) * mm, "end": v(-131.66, 121.1) * mm});
            skLineSegment(sketch, "E2.5.26.0", {"start": v(-131.66, 61.1) * mm, "end": v(-131.66, 11.1) * mm});
            skLineSegment(sketch, "E2.5.26.1", {"start": v(-181.66, 11.1) * mm, "end": v(-131.66, 11.1) * mm});
            skLineSegment(sketch, "E2.5.26.2", {"start": v(-181.66, 61.1) * mm, "end": v(-181.66, 11.1) * mm});
            skLineSegment(sketch, "E2.5.26.3", {"start": v(-181.66, 61.1) * mm, "end": v(-131.66, 61.1) * mm});
            skLineSegment(sketch, "E2.5.27.0", {"start": v(-131.66, 1.1) * mm, "end": v(-131.66, -48.9) * mm});
            skLineSegment(sketch, "E2.5.27.1", {"start": v(-181.66, -48.9) * mm, "end": v(-131.66, -48.9) * mm});
            skLineSegment(sketch, "E2.5.27.2", {"start": v(-181.66, 1.1) * mm, "end": v(-181.66, -48.9) * mm});
            skLineSegment(sketch, "E2.5.27.3", {"start": v(-181.66, 1.1) * mm, "end": v(-131.66, 1.1) * mm});
            skLineSegment(sketch, "E2.5.28.0", {"start": v(-131.66, -58.9) * mm, "end": v(-131.66, -108.9) * mm});
            skLineSegment(sketch, "E2.5.28.1", {"start": v(-181.66, -108.9) * mm, "end": v(-131.66, -108.9) * mm});
            skLineSegment(sketch, "E2.5.28.2", {"start": v(-181.66, -58.9) * mm, "end": v(-181.66, -108.9) * mm});
            skLineSegment(sketch, "E2.5.28.3", {"start": v(-181.66, -58.9) * mm, "end": v(-131.66, -58.9) * mm});
            skLineSegment(sketch, "E2.5.29.0", {"start": v(-131.66, -118.9) * mm, "end": v(-131.66, -168.9) * mm});
            skLineSegment(sketch, "E2.5.29.1", {"start": v(-181.66, -168.9) * mm, "end": v(-131.66, -168.9) * mm});
            skLineSegment(sketch, "E2.5.29.2", {"start": v(-181.66, -118.9) * mm, "end": v(-181.66, -168.9) * mm});
            skLineSegment(sketch, "E2.5.29.3", {"start": v(-181.66, -118.9) * mm, "end": v(-131.66, -118.9) * mm});
            skLineSegment(sketch, "E2.5.30.0", {"start": v(-131.66, -178.9) * mm, "end": v(-131.66, -228.9) * mm});
            skLineSegment(sketch, "E2.5.30.1", {"start": v(-181.66, -228.9) * mm, "end": v(-131.66, -228.9) * mm});
            skLineSegment(sketch, "E2.5.30.2", {"start": v(-181.66, -178.9) * mm, "end": v(-181.66, -228.9) * mm});
            skLineSegment(sketch, "E2.5.30.3", {"start": v(-181.66, -178.9) * mm, "end": v(-131.66, -178.9) * mm});
            skLineSegment(sketch, "E2.5.31.0", {"start": v(-131.66, -238.9) * mm, "end": v(-131.66, -288.9) * mm});
            skLineSegment(sketch, "E2.5.31.1", {"start": v(-181.66, -288.9) * mm, "end": v(-131.66, -288.9) * mm});
            skLineSegment(sketch, "E2.5.31.2", {"start": v(-181.66, -238.9) * mm, "end": v(-181.66, -288.9) * mm});
            skLineSegment(sketch, "E2.5.31.3", {"start": v(-181.66, -238.9) * mm, "end": v(-131.66, -238.9) * mm});
            skLineSegment(sketch, "E2.5.32.0", {"start": v(-131.66, -298.9) * mm, "end": v(-131.66, -348.9) * mm});
            skLineSegment(sketch, "E2.5.32.1", {"start": v(-181.66, -348.9) * mm, "end": v(-131.66, -348.9) * mm});
            skLineSegment(sketch, "E2.5.32.2", {"start": v(-181.66, -298.9) * mm, "end": v(-181.66, -348.9) * mm});
            skLineSegment(sketch, "E2.5.32.3", {"start": v(-181.66, -298.9) * mm, "end": v(-131.66, -298.9) * mm});
            skLineSegment(sketch, "E2.6.0.0", {"start": v(-71.66, 1621.1) * mm, "end": v(-71.66, 1571.1) * mm});
            skLineSegment(sketch, "E2.6.0.1", {"start": v(-121.66, 1571.1) * mm, "end": v(-71.66, 1571.1) * mm});
            skLineSegment(sketch, "E2.6.0.2", {"start": v(-121.66, 1621.1) * mm, "end": v(-121.66, 1571.1) * mm});
            skLineSegment(sketch, "E2.6.0.3", {"start": v(-121.66, 1621.1) * mm, "end": v(-71.66, 1621.1) * mm});
            skLineSegment(sketch, "E2.6.1.0", {"start": v(-71.66, 1561.1) * mm, "end": v(-71.66, 1511.1) * mm});
            skLineSegment(sketch, "E2.6.1.1", {"start": v(-121.66, 1511.1) * mm, "end": v(-71.66, 1511.1) * mm});
            skLineSegment(sketch, "E2.6.1.2", {"start": v(-121.66, 1561.1) * mm, "end": v(-121.66, 1511.1) * mm});
            skLineSegment(sketch, "E2.6.1.3", {"start": v(-121.66, 1561.1) * mm, "end": v(-71.66, 1561.1) * mm});
            skLineSegment(sketch, "E2.6.2.0", {"start": v(-71.66, 1501.1) * mm, "end": v(-71.66, 1451.1) * mm});
            skLineSegment(sketch, "E2.6.2.1", {"start": v(-121.66, 1451.1) * mm, "end": v(-71.66, 1451.1) * mm});
            skLineSegment(sketch, "E2.6.2.2", {"start": v(-121.66, 1501.1) * mm, "end": v(-121.66, 1451.1) * mm});
            skLineSegment(sketch, "E2.6.2.3", {"start": v(-121.66, 1501.1) * mm, "end": v(-71.66, 1501.1) * mm});
            skLineSegment(sketch, "E2.6.3.0", {"start": v(-71.66, 1441.1) * mm, "end": v(-71.66, 1391.1) * mm});
            skLineSegment(sketch, "E2.6.3.1", {"start": v(-121.66, 1391.1) * mm, "end": v(-71.66, 1391.1) * mm});
            skLineSegment(sketch, "E2.6.3.2", {"start": v(-121.66, 1441.1) * mm, "end": v(-121.66, 1391.1) * mm});
            skLineSegment(sketch, "E2.6.3.3", {"start": v(-121.66, 1441.1) * mm, "end": v(-71.66, 1441.1) * mm});
            skLineSegment(sketch, "E2.6.4.0", {"start": v(-71.66, 1381.1) * mm, "end": v(-71.66, 1331.1) * mm});
            skLineSegment(sketch, "E2.6.4.1", {"start": v(-121.66, 1331.1) * mm, "end": v(-71.66, 1331.1) * mm});
            skLineSegment(sketch, "E2.6.4.2", {"start": v(-121.66, 1381.1) * mm, "end": v(-121.66, 1331.1) * mm});
            skLineSegment(sketch, "E2.6.4.3", {"start": v(-121.66, 1381.1) * mm, "end": v(-71.66, 1381.1) * mm});
            skLineSegment(sketch, "E2.6.5.0", {"start": v(-71.66, 1321.1) * mm, "end": v(-71.66, 1271.1) * mm});
            skLineSegment(sketch, "E2.6.5.1", {"start": v(-121.66, 1271.1) * mm, "end": v(-71.66, 1271.1) * mm});
            skLineSegment(sketch, "E2.6.5.2", {"start": v(-121.66, 1321.1) * mm, "end": v(-121.66, 1271.1) * mm});
            skLineSegment(sketch, "E2.6.5.3", {"start": v(-121.66, 1321.1) * mm, "end": v(-71.66, 1321.1) * mm});
            skLineSegment(sketch, "E2.6.6.0", {"start": v(-71.66, 1261.1) * mm, "end": v(-71.66, 1211.1) * mm});
            skLineSegment(sketch, "E2.6.6.1", {"start": v(-121.66, 1211.1) * mm, "end": v(-71.66, 1211.1) * mm});
            skLineSegment(sketch, "E2.6.6.2", {"start": v(-121.66, 1261.1) * mm, "end": v(-121.66, 1211.1) * mm});
            skLineSegment(sketch, "E2.6.6.3", {"start": v(-121.66, 1261.1) * mm, "end": v(-71.66, 1261.1) * mm});
            skLineSegment(sketch, "E2.6.7.0", {"start": v(-71.66, 1201.1) * mm, "end": v(-71.66, 1151.1) * mm});
            skLineSegment(sketch, "E2.6.7.1", {"start": v(-121.66, 1151.1) * mm, "end": v(-71.66, 1151.1) * mm});
            skLineSegment(sketch, "E2.6.7.2", {"start": v(-121.66, 1201.1) * mm, "end": v(-121.66, 1151.1) * mm});
            skLineSegment(sketch, "E2.6.7.3", {"start": v(-121.66, 1201.1) * mm, "end": v(-71.66, 1201.1) * mm});
            skLineSegment(sketch, "E2.6.8.0", {"start": v(-71.66, 1141.1) * mm, "end": v(-71.66, 1091.1) * mm});
            skLineSegment(sketch, "E2.6.8.1", {"start": v(-121.66, 1091.1) * mm, "end": v(-71.66, 1091.1) * mm});
            skLineSegment(sketch, "E2.6.8.2", {"start": v(-121.66, 1141.1) * mm, "end": v(-121.66, 1091.1) * mm});
            skLineSegment(sketch, "E2.6.8.3", {"start": v(-121.66, 1141.1) * mm, "end": v(-71.66, 1141.1) * mm});
            skLineSegment(sketch, "E2.6.9.0", {"start": v(-71.66, 1081.1) * mm, "end": v(-71.66, 1031.1) * mm});
            skLineSegment(sketch, "E2.6.9.1", {"start": v(-121.66, 1031.1) * mm, "end": v(-71.66, 1031.1) * mm});
            skLineSegment(sketch, "E2.6.9.2", {"start": v(-121.66, 1081.1) * mm, "end": v(-121.66, 1031.1) * mm});
            skLineSegment(sketch, "E2.6.9.3", {"start": v(-121.66, 1081.1) * mm, "end": v(-71.66, 1081.1) * mm});
            skLineSegment(sketch, "E2.6.10.0", {"start": v(-71.66, 1021.1) * mm, "end": v(-71.66, 971.1) * mm});
            skLineSegment(sketch, "E2.6.10.1", {"start": v(-121.66, 971.1) * mm, "end": v(-71.66, 971.1) * mm});
            skLineSegment(sketch, "E2.6.10.2", {"start": v(-121.66, 1021.1) * mm, "end": v(-121.66, 971.1) * mm});
            skLineSegment(sketch, "E2.6.10.3", {"start": v(-121.66, 1021.1) * mm, "end": v(-71.66, 1021.1) * mm});
            skLineSegment(sketch, "E2.6.11.0", {"start": v(-71.66, 961.1) * mm, "end": v(-71.66, 911.1) * mm});
            skLineSegment(sketch, "E2.6.11.1", {"start": v(-121.66, 911.1) * mm, "end": v(-71.66, 911.1) * mm});
            skLineSegment(sketch, "E2.6.11.2", {"start": v(-121.66, 961.1) * mm, "end": v(-121.66, 911.1) * mm});
            skLineSegment(sketch, "E2.6.11.3", {"start": v(-121.66, 961.1) * mm, "end": v(-71.66, 961.1) * mm});
            skLineSegment(sketch, "E2.6.12.0", {"start": v(-71.66, 901.1) * mm, "end": v(-71.66, 851.1) * mm});
            skLineSegment(sketch, "E2.6.12.1", {"start": v(-121.66, 851.1) * mm, "end": v(-71.66, 851.1) * mm});
            skLineSegment(sketch, "E2.6.12.2", {"start": v(-121.66, 901.1) * mm, "end": v(-121.66, 851.1) * mm});
            skLineSegment(sketch, "E2.6.12.3", {"start": v(-121.66, 901.1) * mm, "end": v(-71.66, 901.1) * mm});
            skLineSegment(sketch, "E2.6.13.0", {"start": v(-71.66, 841.1) * mm, "end": v(-71.66, 791.1) * mm});
            skLineSegment(sketch, "E2.6.13.1", {"start": v(-121.66, 791.1) * mm, "end": v(-71.66, 791.1) * mm});
            skLineSegment(sketch, "E2.6.13.2", {"start": v(-121.66, 841.1) * mm, "end": v(-121.66, 791.1) * mm});
            skLineSegment(sketch, "E2.6.13.3", {"start": v(-121.66, 841.1) * mm, "end": v(-71.66, 841.1) * mm});
            skLineSegment(sketch, "E2.6.14.0", {"start": v(-71.66, 781.1) * mm, "end": v(-71.66, 731.1) * mm});
            skLineSegment(sketch, "E2.6.14.1", {"start": v(-121.66, 731.1) * mm, "end": v(-71.66, 731.1) * mm});
            skLineSegment(sketch, "E2.6.14.2", {"start": v(-121.66, 781.1) * mm, "end": v(-121.66, 731.1) * mm});
            skLineSegment(sketch, "E2.6.14.3", {"start": v(-121.66, 781.1) * mm, "end": v(-71.66, 781.1) * mm});
            skLineSegment(sketch, "E2.6.15.0", {"start": v(-71.66, 721.1) * mm, "end": v(-71.66, 671.1) * mm});
            skLineSegment(sketch, "E2.6.15.1", {"start": v(-121.66, 671.1) * mm, "end": v(-71.66, 671.1) * mm});
            skLineSegment(sketch, "E2.6.15.2", {"start": v(-121.66, 721.1) * mm, "end": v(-121.66, 671.1) * mm});
            skLineSegment(sketch, "E2.6.15.3", {"start": v(-121.66, 721.1) * mm, "end": v(-71.66, 721.1) * mm});
            skLineSegment(sketch, "E2.6.16.0", {"start": v(-71.66, 661.1) * mm, "end": v(-71.66, 611.1) * mm});
            skLineSegment(sketch, "E2.6.16.1", {"start": v(-121.66, 611.1) * mm, "end": v(-71.66, 611.1) * mm});
            skLineSegment(sketch, "E2.6.16.2", {"start": v(-121.66, 661.1) * mm, "end": v(-121.66, 611.1) * mm});
            skLineSegment(sketch, "E2.6.16.3", {"start": v(-121.66, 661.1) * mm, "end": v(-71.66, 661.1) * mm});
            skLineSegment(sketch, "E2.6.17.0", {"start": v(-71.66, 601.1) * mm, "end": v(-71.66, 551.1) * mm});
            skLineSegment(sketch, "E2.6.17.1", {"start": v(-121.66, 551.1) * mm, "end": v(-71.66, 551.1) * mm});
            skLineSegment(sketch, "E2.6.17.2", {"start": v(-121.66, 601.1) * mm, "end": v(-121.66, 551.1) * mm});
            skLineSegment(sketch, "E2.6.17.3", {"start": v(-121.66, 601.1) * mm, "end": v(-71.66, 601.1) * mm});
            skLineSegment(sketch, "E2.6.18.0", {"start": v(-71.66, 541.1) * mm, "end": v(-71.66, 491.1) * mm});
            skLineSegment(sketch, "E2.6.18.1", {"start": v(-121.66, 491.1) * mm, "end": v(-71.66, 491.1) * mm});
            skLineSegment(sketch, "E2.6.18.2", {"start": v(-121.66, 541.1) * mm, "end": v(-121.66, 491.1) * mm});
            skLineSegment(sketch, "E2.6.18.3", {"start": v(-121.66, 541.1) * mm, "end": v(-71.66, 541.1) * mm});
            skLineSegment(sketch, "E2.6.19.0", {"start": v(-71.66, 481.1) * mm, "end": v(-71.66, 431.1) * mm});
            skLineSegment(sketch, "E2.6.19.1", {"start": v(-121.66, 431.1) * mm, "end": v(-71.66, 431.1) * mm});
            skLineSegment(sketch, "E2.6.19.2", {"start": v(-121.66, 481.1) * mm, "end": v(-121.66, 431.1) * mm});
            skLineSegment(sketch, "E2.6.19.3", {"start": v(-121.66, 481.1) * mm, "end": v(-71.66, 481.1) * mm});
            skLineSegment(sketch, "E2.6.20.0", {"start": v(-71.66, 421.1) * mm, "end": v(-71.66, 371.1) * mm});
            skLineSegment(sketch, "E2.6.20.1", {"start": v(-121.66, 371.1) * mm, "end": v(-71.66, 371.1) * mm});
            skLineSegment(sketch, "E2.6.20.2", {"start": v(-121.66, 421.1) * mm, "end": v(-121.66, 371.1) * mm});
            skLineSegment(sketch, "E2.6.20.3", {"start": v(-121.66, 421.1) * mm, "end": v(-71.66, 421.1) * mm});
            skLineSegment(sketch, "E2.6.21.0", {"start": v(-71.66, 361.1) * mm, "end": v(-71.66, 311.1) * mm});
            skLineSegment(sketch, "E2.6.21.1", {"start": v(-121.66, 311.1) * mm, "end": v(-71.66, 311.1) * mm});
            skLineSegment(sketch, "E2.6.21.2", {"start": v(-121.66, 361.1) * mm, "end": v(-121.66, 311.1) * mm});
            skLineSegment(sketch, "E2.6.21.3", {"start": v(-121.66, 361.1) * mm, "end": v(-71.66, 361.1) * mm});
            skLineSegment(sketch, "E2.6.22.0", {"start": v(-71.66, 301.1) * mm, "end": v(-71.66, 251.1) * mm});
            skLineSegment(sketch, "E2.6.22.1", {"start": v(-121.66, 251.1) * mm, "end": v(-71.66, 251.1) * mm});
            skLineSegment(sketch, "E2.6.22.2", {"start": v(-121.66, 301.1) * mm, "end": v(-121.66, 251.1) * mm});
            skLineSegment(sketch, "E2.6.22.3", {"start": v(-121.66, 301.1) * mm, "end": v(-71.66, 301.1) * mm});
            skLineSegment(sketch, "E2.6.23.0", {"start": v(-71.66, 241.1) * mm, "end": v(-71.66, 191.1) * mm});
            skLineSegment(sketch, "E2.6.23.1", {"start": v(-121.66, 191.1) * mm, "end": v(-71.66, 191.1) * mm});
            skLineSegment(sketch, "E2.6.23.2", {"start": v(-121.66, 241.1) * mm, "end": v(-121.66, 191.1) * mm});
            skLineSegment(sketch, "E2.6.23.3", {"start": v(-121.66, 241.1) * mm, "end": v(-71.66, 241.1) * mm});
            skLineSegment(sketch, "E2.6.24.0", {"start": v(-71.66, 181.1) * mm, "end": v(-71.66, 131.1) * mm});
            skLineSegment(sketch, "E2.6.24.1", {"start": v(-121.66, 131.1) * mm, "end": v(-71.66, 131.1) * mm});
            skLineSegment(sketch, "E2.6.24.2", {"start": v(-121.66, 181.1) * mm, "end": v(-121.66, 131.1) * mm});
            skLineSegment(sketch, "E2.6.24.3", {"start": v(-121.66, 181.1) * mm, "end": v(-71.66, 181.1) * mm});
            skLineSegment(sketch, "E2.6.25.0", {"start": v(-71.66, 121.1) * mm, "end": v(-71.66, 71.1) * mm});
            skLineSegment(sketch, "E2.6.25.1", {"start": v(-121.66, 71.1) * mm, "end": v(-71.66, 71.1) * mm});
            skLineSegment(sketch, "E2.6.25.2", {"start": v(-121.66, 121.1) * mm, "end": v(-121.66, 71.1) * mm});
            skLineSegment(sketch, "E2.6.25.3", {"start": v(-121.66, 121.1) * mm, "end": v(-71.66, 121.1) * mm});
            skLineSegment(sketch, "E2.6.26.0", {"start": v(-71.66, 61.1) * mm, "end": v(-71.66, 11.1) * mm});
            skLineSegment(sketch, "E2.6.26.1", {"start": v(-121.66, 11.1) * mm, "end": v(-71.66, 11.1) * mm});
            skLineSegment(sketch, "E2.6.26.2", {"start": v(-121.66, 61.1) * mm, "end": v(-121.66, 11.1) * mm});
            skLineSegment(sketch, "E2.6.26.3", {"start": v(-121.66, 61.1) * mm, "end": v(-71.66, 61.1) * mm});
            skLineSegment(sketch, "E2.6.27.0", {"start": v(-71.66, 1.1) * mm, "end": v(-71.66, -48.9) * mm});
            skLineSegment(sketch, "E2.6.27.1", {"start": v(-121.66, -48.9) * mm, "end": v(-71.66, -48.9) * mm});
            skLineSegment(sketch, "E2.6.27.2", {"start": v(-121.66, 1.1) * mm, "end": v(-121.66, -48.9) * mm});
            skLineSegment(sketch, "E2.6.27.3", {"start": v(-121.66, 1.1) * mm, "end": v(-71.66, 1.1) * mm});
            skLineSegment(sketch, "E2.6.28.0", {"start": v(-71.66, -58.9) * mm, "end": v(-71.66, -108.9) * mm});
            skLineSegment(sketch, "E2.6.28.1", {"start": v(-121.66, -108.9) * mm, "end": v(-71.66, -108.9) * mm});
            skLineSegment(sketch, "E2.6.28.2", {"start": v(-121.66, -58.9) * mm, "end": v(-121.66, -108.9) * mm});
            skLineSegment(sketch, "E2.6.28.3", {"start": v(-121.66, -58.9) * mm, "end": v(-71.66, -58.9) * mm});
            skLineSegment(sketch, "E2.6.29.0", {"start": v(-71.66, -118.9) * mm, "end": v(-71.66, -168.9) * mm});
            skLineSegment(sketch, "E2.6.29.1", {"start": v(-121.66, -168.9) * mm, "end": v(-71.66, -168.9) * mm});
            skLineSegment(sketch, "E2.6.29.2", {"start": v(-121.66, -118.9) * mm, "end": v(-121.66, -168.9) * mm});
            skLineSegment(sketch, "E2.6.29.3", {"start": v(-121.66, -118.9) * mm, "end": v(-71.66, -118.9) * mm});
            skLineSegment(sketch, "E2.6.30.0", {"start": v(-71.66, -178.9) * mm, "end": v(-71.66, -228.9) * mm});
            skLineSegment(sketch, "E2.6.30.1", {"start": v(-121.66, -228.9) * mm, "end": v(-71.66, -228.9) * mm});
            skLineSegment(sketch, "E2.6.30.2", {"start": v(-121.66, -178.9) * mm, "end": v(-121.66, -228.9) * mm});
            skLineSegment(sketch, "E2.6.30.3", {"start": v(-121.66, -178.9) * mm, "end": v(-71.66, -178.9) * mm});
            skLineSegment(sketch, "E2.6.31.0", {"start": v(-71.66, -238.9) * mm, "end": v(-71.66, -288.9) * mm});
            skLineSegment(sketch, "E2.6.31.1", {"start": v(-121.66, -288.9) * mm, "end": v(-71.66, -288.9) * mm});
            skLineSegment(sketch, "E2.6.31.2", {"start": v(-121.66, -238.9) * mm, "end": v(-121.66, -288.9) * mm});
            skLineSegment(sketch, "E2.6.31.3", {"start": v(-121.66, -238.9) * mm, "end": v(-71.66, -238.9) * mm});
            skLineSegment(sketch, "E2.6.32.0", {"start": v(-71.66, -298.9) * mm, "end": v(-71.66, -348.9) * mm});
            skLineSegment(sketch, "E2.6.32.1", {"start": v(-121.66, -348.9) * mm, "end": v(-71.66, -348.9) * mm});
            skLineSegment(sketch, "E2.6.32.2", {"start": v(-121.66, -298.9) * mm, "end": v(-121.66, -348.9) * mm});
            skLineSegment(sketch, "E2.6.32.3", {"start": v(-121.66, -298.9) * mm, "end": v(-71.66, -298.9) * mm});
            skLineSegment(sketch, "E2.7.0.0", {"start": v(-11.66, 1621.1) * mm, "end": v(-11.66, 1571.1) * mm});
            skLineSegment(sketch, "E2.7.0.1", {"start": v(-61.66, 1571.1) * mm, "end": v(-11.66, 1571.1) * mm});
            skLineSegment(sketch, "E2.7.0.2", {"start": v(-61.66, 1621.1) * mm, "end": v(-61.66, 1571.1) * mm});
            skLineSegment(sketch, "E2.7.0.3", {"start": v(-61.66, 1621.1) * mm, "end": v(-11.66, 1621.1) * mm});
            skLineSegment(sketch, "E2.7.1.0", {"start": v(-11.66, 1561.1) * mm, "end": v(-11.66, 1511.1) * mm});
            skLineSegment(sketch, "E2.7.1.1", {"start": v(-61.66, 1511.1) * mm, "end": v(-11.66, 1511.1) * mm});
            skLineSegment(sketch, "E2.7.1.2", {"start": v(-61.66, 1561.1) * mm, "end": v(-61.66, 1511.1) * mm});
            skLineSegment(sketch, "E2.7.1.3", {"start": v(-61.66, 1561.1) * mm, "end": v(-11.66, 1561.1) * mm});
            skLineSegment(sketch, "E2.7.2.0", {"start": v(-11.66, 1501.1) * mm, "end": v(-11.66, 1451.1) * mm});
            skLineSegment(sketch, "E2.7.2.1", {"start": v(-61.66, 1451.1) * mm, "end": v(-11.66, 1451.1) * mm});
            skLineSegment(sketch, "E2.7.2.2", {"start": v(-61.66, 1501.1) * mm, "end": v(-61.66, 1451.1) * mm});
            skLineSegment(sketch, "E2.7.2.3", {"start": v(-61.66, 1501.1) * mm, "end": v(-11.66, 1501.1) * mm});
            skLineSegment(sketch, "E2.7.3.0", {"start": v(-11.66, 1441.1) * mm, "end": v(-11.66, 1391.1) * mm});
            skLineSegment(sketch, "E2.7.3.1", {"start": v(-61.66, 1391.1) * mm, "end": v(-11.66, 1391.1) * mm});
            skLineSegment(sketch, "E2.7.3.2", {"start": v(-61.66, 1441.1) * mm, "end": v(-61.66, 1391.1) * mm});
            skLineSegment(sketch, "E2.7.3.3", {"start": v(-61.66, 1441.1) * mm, "end": v(-11.66, 1441.1) * mm});
            skLineSegment(sketch, "E2.7.4.0", {"start": v(-11.66, 1381.1) * mm, "end": v(-11.66, 1331.1) * mm});
            skLineSegment(sketch, "E2.7.4.1", {"start": v(-61.66, 1331.1) * mm, "end": v(-11.66, 1331.1) * mm});
            skLineSegment(sketch, "E2.7.4.2", {"start": v(-61.66, 1381.1) * mm, "end": v(-61.66, 1331.1) * mm});
            skLineSegment(sketch, "E2.7.4.3", {"start": v(-61.66, 1381.1) * mm, "end": v(-11.66, 1381.1) * mm});
            skLineSegment(sketch, "E2.7.5.0", {"start": v(-11.66, 1321.1) * mm, "end": v(-11.66, 1271.1) * mm});
            skLineSegment(sketch, "E2.7.5.1", {"start": v(-61.66, 1271.1) * mm, "end": v(-11.66, 1271.1) * mm});
            skLineSegment(sketch, "E2.7.5.2", {"start": v(-61.66, 1321.1) * mm, "end": v(-61.66, 1271.1) * mm});
            skLineSegment(sketch, "E2.7.5.3", {"start": v(-61.66, 1321.1) * mm, "end": v(-11.66, 1321.1) * mm});
            skLineSegment(sketch, "E2.7.6.0", {"start": v(-11.66, 1261.1) * mm, "end": v(-11.66, 1211.1) * mm});
            skLineSegment(sketch, "E2.7.6.1", {"start": v(-61.66, 1211.1) * mm, "end": v(-11.66, 1211.1) * mm});
            skLineSegment(sketch, "E2.7.6.2", {"start": v(-61.66, 1261.1) * mm, "end": v(-61.66, 1211.1) * mm});
            skLineSegment(sketch, "E2.7.6.3", {"start": v(-61.66, 1261.1) * mm, "end": v(-11.66, 1261.1) * mm});
            skLineSegment(sketch, "E2.7.7.0", {"start": v(-11.66, 1201.1) * mm, "end": v(-11.66, 1151.1) * mm});
            skLineSegment(sketch, "E2.7.7.1", {"start": v(-61.66, 1151.1) * mm, "end": v(-11.66, 1151.1) * mm});
            skLineSegment(sketch, "E2.7.7.2", {"start": v(-61.66, 1201.1) * mm, "end": v(-61.66, 1151.1) * mm});
            skLineSegment(sketch, "E2.7.7.3", {"start": v(-61.66, 1201.1) * mm, "end": v(-11.66, 1201.1) * mm});
            skLineSegment(sketch, "E2.7.8.0", {"start": v(-11.66, 1141.1) * mm, "end": v(-11.66, 1091.1) * mm});
            skLineSegment(sketch, "E2.7.8.1", {"start": v(-61.66, 1091.1) * mm, "end": v(-11.66, 1091.1) * mm});
            skLineSegment(sketch, "E2.7.8.2", {"start": v(-61.66, 1141.1) * mm, "end": v(-61.66, 1091.1) * mm});
            skLineSegment(sketch, "E2.7.8.3", {"start": v(-61.66, 1141.1) * mm, "end": v(-11.66, 1141.1) * mm});
            skLineSegment(sketch, "E2.7.9.0", {"start": v(-11.66, 1081.1) * mm, "end": v(-11.66, 1031.1) * mm});
            skLineSegment(sketch, "E2.7.9.1", {"start": v(-61.66, 1031.1) * mm, "end": v(-11.66, 1031.1) * mm});
            skLineSegment(sketch, "E2.7.9.2", {"start": v(-61.66, 1081.1) * mm, "end": v(-61.66, 1031.1) * mm});
            skLineSegment(sketch, "E2.7.9.3", {"start": v(-61.66, 1081.1) * mm, "end": v(-11.66, 1081.1) * mm});
            skLineSegment(sketch, "E2.7.10.0", {"start": v(-11.66, 1021.1) * mm, "end": v(-11.66, 971.1) * mm});
            skLineSegment(sketch, "E2.7.10.1", {"start": v(-61.66, 971.1) * mm, "end": v(-11.66, 971.1) * mm});
            skLineSegment(sketch, "E2.7.10.2", {"start": v(-61.66, 1021.1) * mm, "end": v(-61.66, 971.1) * mm});
            skLineSegment(sketch, "E2.7.10.3", {"start": v(-61.66, 1021.1) * mm, "end": v(-11.66, 1021.1) * mm});
            skLineSegment(sketch, "E2.7.11.0", {"start": v(-11.66, 961.1) * mm, "end": v(-11.66, 911.1) * mm});
            skLineSegment(sketch, "E2.7.11.1", {"start": v(-61.66, 911.1) * mm, "end": v(-11.66, 911.1) * mm});
            skLineSegment(sketch, "E2.7.11.2", {"start": v(-61.66, 961.1) * mm, "end": v(-61.66, 911.1) * mm});
            skLineSegment(sketch, "E2.7.11.3", {"start": v(-61.66, 961.1) * mm, "end": v(-11.66, 961.1) * mm});
            skLineSegment(sketch, "E2.7.12.0", {"start": v(-11.66, 901.1) * mm, "end": v(-11.66, 851.1) * mm});
            skLineSegment(sketch, "E2.7.12.1", {"start": v(-61.66, 851.1) * mm, "end": v(-11.66, 851.1) * mm});
            skLineSegment(sketch, "E2.7.12.2", {"start": v(-61.66, 901.1) * mm, "end": v(-61.66, 851.1) * mm});
            skLineSegment(sketch, "E2.7.12.3", {"start": v(-61.66, 901.1) * mm, "end": v(-11.66, 901.1) * mm});
            skLineSegment(sketch, "E2.7.13.0", {"start": v(-11.66, 841.1) * mm, "end": v(-11.66, 791.1) * mm});
            skLineSegment(sketch, "E2.7.13.1", {"start": v(-61.66, 791.1) * mm, "end": v(-11.66, 791.1) * mm});
            skLineSegment(sketch, "E2.7.13.2", {"start": v(-61.66, 841.1) * mm, "end": v(-61.66, 791.1) * mm});
            skLineSegment(sketch, "E2.7.13.3", {"start": v(-61.66, 841.1) * mm, "end": v(-11.66, 841.1) * mm});
            skLineSegment(sketch, "E2.7.14.0", {"start": v(-11.66, 781.1) * mm, "end": v(-11.66, 731.1) * mm});
            skLineSegment(sketch, "E2.7.14.1", {"start": v(-61.66, 731.1) * mm, "end": v(-11.66, 731.1) * mm});
            skLineSegment(sketch, "E2.7.14.2", {"start": v(-61.66, 781.1) * mm, "end": v(-61.66, 731.1) * mm});
            skLineSegment(sketch, "E2.7.14.3", {"start": v(-61.66, 781.1) * mm, "end": v(-11.66, 781.1) * mm});
            skLineSegment(sketch, "E2.7.15.0", {"start": v(-11.66, 721.1) * mm, "end": v(-11.66, 671.1) * mm});
            skLineSegment(sketch, "E2.7.15.1", {"start": v(-61.66, 671.1) * mm, "end": v(-11.66, 671.1) * mm});
            skLineSegment(sketch, "E2.7.15.2", {"start": v(-61.66, 721.1) * mm, "end": v(-61.66, 671.1) * mm});
            skLineSegment(sketch, "E2.7.15.3", {"start": v(-61.66, 721.1) * mm, "end": v(-11.66, 721.1) * mm});
            skLineSegment(sketch, "E2.7.16.0", {"start": v(-11.66, 661.1) * mm, "end": v(-11.66, 611.1) * mm});
            skLineSegment(sketch, "E2.7.16.1", {"start": v(-61.66, 611.1) * mm, "end": v(-11.66, 611.1) * mm});
            skLineSegment(sketch, "E2.7.16.2", {"start": v(-61.66, 661.1) * mm, "end": v(-61.66, 611.1) * mm});
            skLineSegment(sketch, "E2.7.16.3", {"start": v(-61.66, 661.1) * mm, "end": v(-11.66, 661.1) * mm});
            skLineSegment(sketch, "E2.7.17.0", {"start": v(-11.66, 601.1) * mm, "end": v(-11.66, 551.1) * mm});
            skLineSegment(sketch, "E2.7.17.1", {"start": v(-61.66, 551.1) * mm, "end": v(-11.66, 551.1) * mm});
            skLineSegment(sketch, "E2.7.17.2", {"start": v(-61.66, 601.1) * mm, "end": v(-61.66, 551.1) * mm});
            skLineSegment(sketch, "E2.7.17.3", {"start": v(-61.66, 601.1) * mm, "end": v(-11.66, 601.1) * mm});
            skLineSegment(sketch, "E2.7.18.0", {"start": v(-11.66, 541.1) * mm, "end": v(-11.66, 491.1) * mm});
            skLineSegment(sketch, "E2.7.18.1", {"start": v(-61.66, 491.1) * mm, "end": v(-11.66, 491.1) * mm});
            skLineSegment(sketch, "E2.7.18.2", {"start": v(-61.66, 541.1) * mm, "end": v(-61.66, 491.1) * mm});
            skLineSegment(sketch, "E2.7.18.3", {"start": v(-61.66, 541.1) * mm, "end": v(-11.66, 541.1) * mm});
            skLineSegment(sketch, "E2.7.19.0", {"start": v(-11.66, 481.1) * mm, "end": v(-11.66, 431.1) * mm});
            skLineSegment(sketch, "E2.7.19.1", {"start": v(-61.66, 431.1) * mm, "end": v(-11.66, 431.1) * mm});
            skLineSegment(sketch, "E2.7.19.2", {"start": v(-61.66, 481.1) * mm, "end": v(-61.66, 431.1) * mm});
            skLineSegment(sketch, "E2.7.19.3", {"start": v(-61.66, 481.1) * mm, "end": v(-11.66, 481.1) * mm});
            skLineSegment(sketch, "E2.7.20.0", {"start": v(-11.66, 421.1) * mm, "end": v(-11.66, 371.1) * mm});
            skLineSegment(sketch, "E2.7.20.1", {"start": v(-61.66, 371.1) * mm, "end": v(-11.66, 371.1) * mm});
            skLineSegment(sketch, "E2.7.20.2", {"start": v(-61.66, 421.1) * mm, "end": v(-61.66, 371.1) * mm});
            skLineSegment(sketch, "E2.7.20.3", {"start": v(-61.66, 421.1) * mm, "end": v(-11.66, 421.1) * mm});
            skLineSegment(sketch, "E2.7.21.0", {"start": v(-11.66, 361.1) * mm, "end": v(-11.66, 311.1) * mm});
            skLineSegment(sketch, "E2.7.21.1", {"start": v(-61.66, 311.1) * mm, "end": v(-11.66, 311.1) * mm});
            skLineSegment(sketch, "E2.7.21.2", {"start": v(-61.66, 361.1) * mm, "end": v(-61.66, 311.1) * mm});
            skLineSegment(sketch, "E2.7.21.3", {"start": v(-61.66, 361.1) * mm, "end": v(-11.66, 361.1) * mm});
            skLineSegment(sketch, "E2.7.22.0", {"start": v(-11.66, 301.1) * mm, "end": v(-11.66, 251.1) * mm});
            skLineSegment(sketch, "E2.7.22.1", {"start": v(-61.66, 251.1) * mm, "end": v(-11.66, 251.1) * mm});
            skLineSegment(sketch, "E2.7.22.2", {"start": v(-61.66, 301.1) * mm, "end": v(-61.66, 251.1) * mm});
            skLineSegment(sketch, "E2.7.22.3", {"start": v(-61.66, 301.1) * mm, "end": v(-11.66, 301.1) * mm});
            skLineSegment(sketch, "E2.7.23.0", {"start": v(-11.66, 241.1) * mm, "end": v(-11.66, 191.1) * mm});
            skLineSegment(sketch, "E2.7.23.1", {"start": v(-61.66, 191.1) * mm, "end": v(-11.66, 191.1) * mm});
            skLineSegment(sketch, "E2.7.23.2", {"start": v(-61.66, 241.1) * mm, "end": v(-61.66, 191.1) * mm});
            skLineSegment(sketch, "E2.7.23.3", {"start": v(-61.66, 241.1) * mm, "end": v(-11.66, 241.1) * mm});
            skLineSegment(sketch, "E2.7.24.0", {"start": v(-11.66, 181.1) * mm, "end": v(-11.66, 131.1) * mm});
            skLineSegment(sketch, "E2.7.24.1", {"start": v(-61.66, 131.1) * mm, "end": v(-11.66, 131.1) * mm});
            skLineSegment(sketch, "E2.7.24.2", {"start": v(-61.66, 181.1) * mm, "end": v(-61.66, 131.1) * mm});
            skLineSegment(sketch, "E2.7.24.3", {"start": v(-61.66, 181.1) * mm, "end": v(-11.66, 181.1) * mm});
            skLineSegment(sketch, "E2.7.25.0", {"start": v(-11.66, 121.1) * mm, "end": v(-11.66, 71.1) * mm});
            skLineSegment(sketch, "E2.7.25.1", {"start": v(-61.66, 71.1) * mm, "end": v(-11.66, 71.1) * mm});
            skLineSegment(sketch, "E2.7.25.2", {"start": v(-61.66, 121.1) * mm, "end": v(-61.66, 71.1) * mm});
            skLineSegment(sketch, "E2.7.25.3", {"start": v(-61.66, 121.1) * mm, "end": v(-11.66, 121.1) * mm});
            skLineSegment(sketch, "E2.7.26.0", {"start": v(-11.66, 61.1) * mm, "end": v(-11.66, 11.1) * mm});
            skLineSegment(sketch, "E2.7.26.1", {"start": v(-61.66, 11.1) * mm, "end": v(-11.66, 11.1) * mm});
            skLineSegment(sketch, "E2.7.26.2", {"start": v(-61.66, 61.1) * mm, "end": v(-61.66, 11.1) * mm});
            skLineSegment(sketch, "E2.7.26.3", {"start": v(-61.66, 61.1) * mm, "end": v(-11.66, 61.1) * mm});
            skLineSegment(sketch, "E2.7.27.0", {"start": v(-11.66, 1.1) * mm, "end": v(-11.66, -48.9) * mm});
            skLineSegment(sketch, "E2.7.27.1", {"start": v(-61.66, -48.9) * mm, "end": v(-11.66, -48.9) * mm});
            skLineSegment(sketch, "E2.7.27.2", {"start": v(-61.66, 1.1) * mm, "end": v(-61.66, -48.9) * mm});
            skLineSegment(sketch, "E2.7.27.3", {"start": v(-61.66, 1.1) * mm, "end": v(-11.66, 1.1) * mm});
            skLineSegment(sketch, "E2.7.28.0", {"start": v(-11.66, -58.9) * mm, "end": v(-11.66, -108.9) * mm});
            skLineSegment(sketch, "E2.7.28.1", {"start": v(-61.66, -108.9) * mm, "end": v(-11.66, -108.9) * mm});
            skLineSegment(sketch, "E2.7.28.2", {"start": v(-61.66, -58.9) * mm, "end": v(-61.66, -108.9) * mm});
            skLineSegment(sketch, "E2.7.28.3", {"start": v(-61.66, -58.9) * mm, "end": v(-11.66, -58.9) * mm});
            skLineSegment(sketch, "E2.7.29.0", {"start": v(-11.66, -118.9) * mm, "end": v(-11.66, -168.9) * mm});
            skLineSegment(sketch, "E2.7.29.1", {"start": v(-61.66, -168.9) * mm, "end": v(-11.66, -168.9) * mm});
            skLineSegment(sketch, "E2.7.29.2", {"start": v(-61.66, -118.9) * mm, "end": v(-61.66, -168.9) * mm});
            skLineSegment(sketch, "E2.7.29.3", {"start": v(-61.66, -118.9) * mm, "end": v(-11.66, -118.9) * mm});
            skLineSegment(sketch, "E2.7.30.0", {"start": v(-11.66, -178.9) * mm, "end": v(-11.66, -228.9) * mm});
            skLineSegment(sketch, "E2.7.30.1", {"start": v(-61.66, -228.9) * mm, "end": v(-11.66, -228.9) * mm});
            skLineSegment(sketch, "E2.7.30.2", {"start": v(-61.66, -178.9) * mm, "end": v(-61.66, -228.9) * mm});
            skLineSegment(sketch, "E2.7.30.3", {"start": v(-61.66, -178.9) * mm, "end": v(-11.66, -178.9) * mm});
            skLineSegment(sketch, "E2.7.31.0", {"start": v(-11.66, -238.9) * mm, "end": v(-11.66, -288.9) * mm});
            skLineSegment(sketch, "E2.7.31.1", {"start": v(-61.66, -288.9) * mm, "end": v(-11.66, -288.9) * mm});
            skLineSegment(sketch, "E2.7.31.2", {"start": v(-61.66, -238.9) * mm, "end": v(-61.66, -288.9) * mm});
            skLineSegment(sketch, "E2.7.31.3", {"start": v(-61.66, -238.9) * mm, "end": v(-11.66, -238.9) * mm});
            skLineSegment(sketch, "E2.7.32.0", {"start": v(-11.66, -298.9) * mm, "end": v(-11.66, -348.9) * mm});
            skLineSegment(sketch, "E2.7.32.1", {"start": v(-61.66, -348.9) * mm, "end": v(-11.66, -348.9) * mm});
            skLineSegment(sketch, "E2.7.32.2", {"start": v(-61.66, -298.9) * mm, "end": v(-61.66, -348.9) * mm});
            skLineSegment(sketch, "E2.7.32.3", {"start": v(-61.66, -298.9) * mm, "end": v(-11.66, -298.9) * mm});
            skLineSegment(sketch, "E2.8.0.0", {"start": v(48.34, 1621.1) * mm, "end": v(48.34, 1571.1) * mm});
            skLineSegment(sketch, "E2.8.0.1", {"start": v(-1.66, 1571.1) * mm, "end": v(48.34, 1571.1) * mm});
            skLineSegment(sketch, "E2.8.0.2", {"start": v(-1.66, 1621.1) * mm, "end": v(-1.66, 1571.1) * mm});
            skLineSegment(sketch, "E2.8.0.3", {"start": v(-1.66, 1621.1) * mm, "end": v(48.34, 1621.1) * mm});
            skLineSegment(sketch, "E2.8.1.0", {"start": v(48.34, 1561.1) * mm, "end": v(48.34, 1511.1) * mm});
            skLineSegment(sketch, "E2.8.1.1", {"start": v(-1.66, 1511.1) * mm, "end": v(48.34, 1511.1) * mm});
            skLineSegment(sketch, "E2.8.1.2", {"start": v(-1.66, 1561.1) * mm, "end": v(-1.66, 1511.1) * mm});
            skLineSegment(sketch, "E2.8.1.3", {"start": v(-1.66, 1561.1) * mm, "end": v(48.34, 1561.1) * mm});
            skLineSegment(sketch, "E2.8.2.0", {"start": v(48.34, 1501.1) * mm, "end": v(48.34, 1451.1) * mm});
            skLineSegment(sketch, "E2.8.2.1", {"start": v(-1.66, 1451.1) * mm, "end": v(48.34, 1451.1) * mm});
            skLineSegment(sketch, "E2.8.2.2", {"start": v(-1.66, 1501.1) * mm, "end": v(-1.66, 1451.1) * mm});
            skLineSegment(sketch, "E2.8.2.3", {"start": v(-1.66, 1501.1) * mm, "end": v(48.34, 1501.1) * mm});
            skLineSegment(sketch, "E2.8.3.0", {"start": v(48.34, 1441.1) * mm, "end": v(48.34, 1391.1) * mm});
            skLineSegment(sketch, "E2.8.3.1", {"start": v(-1.66, 1391.1) * mm, "end": v(48.34, 1391.1) * mm});
            skLineSegment(sketch, "E2.8.3.2", {"start": v(-1.66, 1441.1) * mm, "end": v(-1.66, 1391.1) * mm});
            skLineSegment(sketch, "E2.8.3.3", {"start": v(-1.66, 1441.1) * mm, "end": v(48.34, 1441.1) * mm});
            skLineSegment(sketch, "E2.8.4.0", {"start": v(48.34, 1381.1) * mm, "end": v(48.34, 1331.1) * mm});
            skLineSegment(sketch, "E2.8.4.1", {"start": v(-1.66, 1331.1) * mm, "end": v(48.34, 1331.1) * mm});
            skLineSegment(sketch, "E2.8.4.2", {"start": v(-1.66, 1381.1) * mm, "end": v(-1.66, 1331.1) * mm});
            skLineSegment(sketch, "E2.8.4.3", {"start": v(-1.66, 1381.1) * mm, "end": v(48.34, 1381.1) * mm});
            skLineSegment(sketch, "E2.8.5.0", {"start": v(48.34, 1321.1) * mm, "end": v(48.34, 1271.1) * mm});
            skLineSegment(sketch, "E2.8.5.1", {"start": v(-1.66, 1271.1) * mm, "end": v(48.34, 1271.1) * mm});
            skLineSegment(sketch, "E2.8.5.2", {"start": v(-1.66, 1321.1) * mm, "end": v(-1.66, 1271.1) * mm});
            skLineSegment(sketch, "E2.8.5.3", {"start": v(-1.66, 1321.1) * mm, "end": v(48.34, 1321.1) * mm});
            skLineSegment(sketch, "E2.8.6.0", {"start": v(48.34, 1261.1) * mm, "end": v(48.34, 1211.1) * mm});
            skLineSegment(sketch, "E2.8.6.1", {"start": v(-1.66, 1211.1) * mm, "end": v(48.34, 1211.1) * mm});
            skLineSegment(sketch, "E2.8.6.2", {"start": v(-1.66, 1261.1) * mm, "end": v(-1.66, 1211.1) * mm});
            skLineSegment(sketch, "E2.8.6.3", {"start": v(-1.66, 1261.1) * mm, "end": v(48.34, 1261.1) * mm});
            skLineSegment(sketch, "E2.8.7.0", {"start": v(48.34, 1201.1) * mm, "end": v(48.34, 1151.1) * mm});
            skLineSegment(sketch, "E2.8.7.1", {"start": v(-1.66, 1151.1) * mm, "end": v(48.34, 1151.1) * mm});
            skLineSegment(sketch, "E2.8.7.2", {"start": v(-1.66, 1201.1) * mm, "end": v(-1.66, 1151.1) * mm});
            skLineSegment(sketch, "E2.8.7.3", {"start": v(-1.66, 1201.1) * mm, "end": v(48.34, 1201.1) * mm});
            skLineSegment(sketch, "E2.8.8.0", {"start": v(48.34, 1141.1) * mm, "end": v(48.34, 1091.1) * mm});
            skLineSegment(sketch, "E2.8.8.1", {"start": v(-1.66, 1091.1) * mm, "end": v(48.34, 1091.1) * mm});
            skLineSegment(sketch, "E2.8.8.2", {"start": v(-1.66, 1141.1) * mm, "end": v(-1.66, 1091.1) * mm});
            skLineSegment(sketch, "E2.8.8.3", {"start": v(-1.66, 1141.1) * mm, "end": v(48.34, 1141.1) * mm});
            skLineSegment(sketch, "E2.8.9.0", {"start": v(48.34, 1081.1) * mm, "end": v(48.34, 1031.1) * mm});
            skLineSegment(sketch, "E2.8.9.1", {"start": v(-1.66, 1031.1) * mm, "end": v(48.34, 1031.1) * mm});
            skLineSegment(sketch, "E2.8.9.2", {"start": v(-1.66, 1081.1) * mm, "end": v(-1.66, 1031.1) * mm});
            skLineSegment(sketch, "E2.8.9.3", {"start": v(-1.66, 1081.1) * mm, "end": v(48.34, 1081.1) * mm});
            skLineSegment(sketch, "E2.8.10.0", {"start": v(48.34, 1021.1) * mm, "end": v(48.34, 971.1) * mm});
            skLineSegment(sketch, "E2.8.10.1", {"start": v(-1.66, 971.1) * mm, "end": v(48.34, 971.1) * mm});
            skLineSegment(sketch, "E2.8.10.2", {"start": v(-1.66, 1021.1) * mm, "end": v(-1.66, 971.1) * mm});
            skLineSegment(sketch, "E2.8.10.3", {"start": v(-1.66, 1021.1) * mm, "end": v(48.34, 1021.1) * mm});
            skLineSegment(sketch, "E2.8.11.0", {"start": v(48.34, 961.1) * mm, "end": v(48.34, 911.1) * mm});
            skLineSegment(sketch, "E2.8.11.1", {"start": v(-1.66, 911.1) * mm, "end": v(48.34, 911.1) * mm});
            skLineSegment(sketch, "E2.8.11.2", {"start": v(-1.66, 961.1) * mm, "end": v(-1.66, 911.1) * mm});
            skLineSegment(sketch, "E2.8.11.3", {"start": v(-1.66, 961.1) * mm, "end": v(48.34, 961.1) * mm});
            skLineSegment(sketch, "E2.8.12.0", {"start": v(48.34, 901.1) * mm, "end": v(48.34, 851.1) * mm});
            skLineSegment(sketch, "E2.8.12.1", {"start": v(-1.66, 851.1) * mm, "end": v(48.34, 851.1) * mm});
            skLineSegment(sketch, "E2.8.12.2", {"start": v(-1.66, 901.1) * mm, "end": v(-1.66, 851.1) * mm});
            skLineSegment(sketch, "E2.8.12.3", {"start": v(-1.66, 901.1) * mm, "end": v(48.34, 901.1) * mm});
            skLineSegment(sketch, "E2.8.13.0", {"start": v(48.34, 841.1) * mm, "end": v(48.34, 791.1) * mm});
            skLineSegment(sketch, "E2.8.13.1", {"start": v(-1.66, 791.1) * mm, "end": v(48.34, 791.1) * mm});
            skLineSegment(sketch, "E2.8.13.2", {"start": v(-1.66, 841.1) * mm, "end": v(-1.66, 791.1) * mm});
            skLineSegment(sketch, "E2.8.13.3", {"start": v(-1.66, 841.1) * mm, "end": v(48.34, 841.1) * mm});
            skLineSegment(sketch, "E2.8.14.0", {"start": v(48.34, 781.1) * mm, "end": v(48.34, 731.1) * mm});
            skLineSegment(sketch, "E2.8.14.1", {"start": v(-1.66, 731.1) * mm, "end": v(48.34, 731.1) * mm});
            skLineSegment(sketch, "E2.8.14.2", {"start": v(-1.66, 781.1) * mm, "end": v(-1.66, 731.1) * mm});
            skLineSegment(sketch, "E2.8.14.3", {"start": v(-1.66, 781.1) * mm, "end": v(48.34, 781.1) * mm});
            skLineSegment(sketch, "E2.8.15.0", {"start": v(48.34, 721.1) * mm, "end": v(48.34, 671.1) * mm});
            skLineSegment(sketch, "E2.8.15.1", {"start": v(-1.66, 671.1) * mm, "end": v(48.34, 671.1) * mm});
            skLineSegment(sketch, "E2.8.15.2", {"start": v(-1.66, 721.1) * mm, "end": v(-1.66, 671.1) * mm});
            skLineSegment(sketch, "E2.8.15.3", {"start": v(-1.66, 721.1) * mm, "end": v(48.34, 721.1) * mm});
            skLineSegment(sketch, "E2.8.16.0", {"start": v(48.34, 661.1) * mm, "end": v(48.34, 611.1) * mm});
            skLineSegment(sketch, "E2.8.16.1", {"start": v(-1.66, 611.1) * mm, "end": v(48.34, 611.1) * mm});
            skLineSegment(sketch, "E2.8.16.2", {"start": v(-1.66, 661.1) * mm, "end": v(-1.66, 611.1) * mm});
            skLineSegment(sketch, "E2.8.16.3", {"start": v(-1.66, 661.1) * mm, "end": v(48.34, 661.1) * mm});
            skLineSegment(sketch, "E2.8.17.0", {"start": v(48.34, 601.1) * mm, "end": v(48.34, 551.1) * mm});
            skLineSegment(sketch, "E2.8.17.1", {"start": v(-1.66, 551.1) * mm, "end": v(48.34, 551.1) * mm});
            skLineSegment(sketch, "E2.8.17.2", {"start": v(-1.66, 601.1) * mm, "end": v(-1.66, 551.1) * mm});
            skLineSegment(sketch, "E2.8.17.3", {"start": v(-1.66, 601.1) * mm, "end": v(48.34, 601.1) * mm});
            skLineSegment(sketch, "E2.8.18.0", {"start": v(48.34, 541.1) * mm, "end": v(48.34, 491.1) * mm});
            skLineSegment(sketch, "E2.8.18.1", {"start": v(-1.66, 491.1) * mm, "end": v(48.34, 491.1) * mm});
            skLineSegment(sketch, "E2.8.18.2", {"start": v(-1.66, 541.1) * mm, "end": v(-1.66, 491.1) * mm});
            skLineSegment(sketch, "E2.8.18.3", {"start": v(-1.66, 541.1) * mm, "end": v(48.34, 541.1) * mm});
            skLineSegment(sketch, "E2.8.19.0", {"start": v(48.34, 481.1) * mm, "end": v(48.34, 431.1) * mm});
            skLineSegment(sketch, "E2.8.19.1", {"start": v(-1.66, 431.1) * mm, "end": v(48.34, 431.1) * mm});
            skLineSegment(sketch, "E2.8.19.2", {"start": v(-1.66, 481.1) * mm, "end": v(-1.66, 431.1) * mm});
            skLineSegment(sketch, "E2.8.19.3", {"start": v(-1.66, 481.1) * mm, "end": v(48.34, 481.1) * mm});
            skLineSegment(sketch, "E2.8.20.0", {"start": v(48.34, 421.1) * mm, "end": v(48.34, 371.1) * mm});
            skLineSegment(sketch, "E2.8.20.1", {"start": v(-1.66, 371.1) * mm, "end": v(48.34, 371.1) * mm});
            skLineSegment(sketch, "E2.8.20.2", {"start": v(-1.66, 421.1) * mm, "end": v(-1.66, 371.1) * mm});
            skLineSegment(sketch, "E2.8.20.3", {"start": v(-1.66, 421.1) * mm, "end": v(48.34, 421.1) * mm});
            skLineSegment(sketch, "E2.8.21.0", {"start": v(48.34, 361.1) * mm, "end": v(48.34, 311.1) * mm});
            skLineSegment(sketch, "E2.8.21.1", {"start": v(-1.66, 311.1) * mm, "end": v(48.34, 311.1) * mm});
            skLineSegment(sketch, "E2.8.21.2", {"start": v(-1.66, 361.1) * mm, "end": v(-1.66, 311.1) * mm});
            skLineSegment(sketch, "E2.8.21.3", {"start": v(-1.66, 361.1) * mm, "end": v(48.34, 361.1) * mm});
            skLineSegment(sketch, "E2.8.22.0", {"start": v(48.34, 301.1) * mm, "end": v(48.34, 251.1) * mm});
            skLineSegment(sketch, "E2.8.22.1", {"start": v(-1.66, 251.1) * mm, "end": v(48.34, 251.1) * mm});
            skLineSegment(sketch, "E2.8.22.2", {"start": v(-1.66, 301.1) * mm, "end": v(-1.66, 251.1) * mm});
            skLineSegment(sketch, "E2.8.22.3", {"start": v(-1.66, 301.1) * mm, "end": v(48.34, 301.1) * mm});
            skLineSegment(sketch, "E2.8.23.0", {"start": v(48.34, 241.1) * mm, "end": v(48.34, 191.1) * mm});
            skLineSegment(sketch, "E2.8.23.1", {"start": v(-1.66, 191.1) * mm, "end": v(48.34, 191.1) * mm});
            skLineSegment(sketch, "E2.8.23.2", {"start": v(-1.66, 241.1) * mm, "end": v(-1.66, 191.1) * mm});
            skLineSegment(sketch, "E2.8.23.3", {"start": v(-1.66, 241.1) * mm, "end": v(48.34, 241.1) * mm});
            skLineSegment(sketch, "E2.8.24.0", {"start": v(48.34, 181.1) * mm, "end": v(48.34, 131.1) * mm});
            skLineSegment(sketch, "E2.8.24.1", {"start": v(-1.66, 131.1) * mm, "end": v(48.34, 131.1) * mm});
            skLineSegment(sketch, "E2.8.24.2", {"start": v(-1.66, 181.1) * mm, "end": v(-1.66, 131.1) * mm});
            skLineSegment(sketch, "E2.8.24.3", {"start": v(-1.66, 181.1) * mm, "end": v(48.34, 181.1) * mm});
            skLineSegment(sketch, "E2.8.25.0", {"start": v(48.34, 121.1) * mm, "end": v(48.34, 71.1) * mm});
            skLineSegment(sketch, "E2.8.25.1", {"start": v(-1.66, 71.1) * mm, "end": v(48.34, 71.1) * mm});
            skLineSegment(sketch, "E2.8.25.2", {"start": v(-1.66, 121.1) * mm, "end": v(-1.66, 71.1) * mm});
            skLineSegment(sketch, "E2.8.25.3", {"start": v(-1.66, 121.1) * mm, "end": v(48.34, 121.1) * mm});
            skLineSegment(sketch, "E2.8.26.0", {"start": v(48.34, 61.1) * mm, "end": v(48.34, 11.1) * mm});
            skLineSegment(sketch, "E2.8.26.1", {"start": v(-1.66, 11.1) * mm, "end": v(48.34, 11.1) * mm});
            skLineSegment(sketch, "E2.8.26.2", {"start": v(-1.66, 61.1) * mm, "end": v(-1.66, 11.1) * mm});
            skLineSegment(sketch, "E2.8.26.3", {"start": v(-1.66, 61.1) * mm, "end": v(48.34, 61.1) * mm});
            skLineSegment(sketch, "E2.8.27.0", {"start": v(48.34, 1.1) * mm, "end": v(48.34, -48.9) * mm});
            skLineSegment(sketch, "E2.8.27.1", {"start": v(-1.66, -48.9) * mm, "end": v(48.34, -48.9) * mm});
            skLineSegment(sketch, "E2.8.27.2", {"start": v(-1.66, 1.1) * mm, "end": v(-1.66, -48.9) * mm});
            skLineSegment(sketch, "E2.8.27.3", {"start": v(-1.66, 1.1) * mm, "end": v(48.34, 1.1) * mm});
            skLineSegment(sketch, "E2.8.28.0", {"start": v(48.34, -58.9) * mm, "end": v(48.34, -108.9) * mm});
            skLineSegment(sketch, "E2.8.28.1", {"start": v(-1.66, -108.9) * mm, "end": v(48.34, -108.9) * mm});
            skLineSegment(sketch, "E2.8.28.2", {"start": v(-1.66, -58.9) * mm, "end": v(-1.66, -108.9) * mm});
            skLineSegment(sketch, "E2.8.28.3", {"start": v(-1.66, -58.9) * mm, "end": v(48.34, -58.9) * mm});
            skLineSegment(sketch, "E2.8.29.0", {"start": v(48.34, -118.9) * mm, "end": v(48.34, -168.9) * mm});
            skLineSegment(sketch, "E2.8.29.1", {"start": v(-1.66, -168.9) * mm, "end": v(48.34, -168.9) * mm});
            skLineSegment(sketch, "E2.8.29.2", {"start": v(-1.66, -118.9) * mm, "end": v(-1.66, -168.9) * mm});
            skLineSegment(sketch, "E2.8.29.3", {"start": v(-1.66, -118.9) * mm, "end": v(48.34, -118.9) * mm});
            skLineSegment(sketch, "E2.8.30.0", {"start": v(48.34, -178.9) * mm, "end": v(48.34, -228.9) * mm});
            skLineSegment(sketch, "E2.8.30.1", {"start": v(-1.66, -228.9) * mm, "end": v(48.34, -228.9) * mm});
            skLineSegment(sketch, "E2.8.30.2", {"start": v(-1.66, -178.9) * mm, "end": v(-1.66, -228.9) * mm});
            skLineSegment(sketch, "E2.8.30.3", {"start": v(-1.66, -178.9) * mm, "end": v(48.34, -178.9) * mm});
            skLineSegment(sketch, "E2.8.31.0", {"start": v(48.34, -238.9) * mm, "end": v(48.34, -288.9) * mm});
            skLineSegment(sketch, "E2.8.31.1", {"start": v(-1.66, -288.9) * mm, "end": v(48.34, -288.9) * mm});
            skLineSegment(sketch, "E2.8.31.2", {"start": v(-1.66, -238.9) * mm, "end": v(-1.66, -288.9) * mm});
            skLineSegment(sketch, "E2.8.31.3", {"start": v(-1.66, -238.9) * mm, "end": v(48.34, -238.9) * mm});
            skLineSegment(sketch, "E2.8.32.0", {"start": v(48.34, -298.9) * mm, "end": v(48.34, -348.9) * mm});
            skLineSegment(sketch, "E2.8.32.1", {"start": v(-1.66, -348.9) * mm, "end": v(48.34, -348.9) * mm});
            skLineSegment(sketch, "E2.8.32.2", {"start": v(-1.66, -298.9) * mm, "end": v(-1.66, -348.9) * mm});
            skLineSegment(sketch, "E2.8.32.3", {"start": v(-1.66, -298.9) * mm, "end": v(48.34, -298.9) * mm});
            skLineSegment(sketch, "E2.9.0.0", {"start": v(108.34, 1621.1) * mm, "end": v(108.34, 1571.1) * mm});
            skLineSegment(sketch, "E2.9.0.1", {"start": v(58.34, 1571.1) * mm, "end": v(108.34, 1571.1) * mm});
            skLineSegment(sketch, "E2.9.0.2", {"start": v(58.34, 1621.1) * mm, "end": v(58.34, 1571.1) * mm});
            skLineSegment(sketch, "E2.9.0.3", {"start": v(58.34, 1621.1) * mm, "end": v(108.34, 1621.1) * mm});
            skLineSegment(sketch, "E2.9.1.0", {"start": v(108.34, 1561.1) * mm, "end": v(108.34, 1511.1) * mm});
            skLineSegment(sketch, "E2.9.1.1", {"start": v(58.34, 1511.1) * mm, "end": v(108.34, 1511.1) * mm});
            skLineSegment(sketch, "E2.9.1.2", {"start": v(58.34, 1561.1) * mm, "end": v(58.34, 1511.1) * mm});
            skLineSegment(sketch, "E2.9.1.3", {"start": v(58.34, 1561.1) * mm, "end": v(108.34, 1561.1) * mm});
            skLineSegment(sketch, "E2.9.2.0", {"start": v(108.34, 1501.1) * mm, "end": v(108.34, 1451.1) * mm});
            skLineSegment(sketch, "E2.9.2.1", {"start": v(58.34, 1451.1) * mm, "end": v(108.34, 1451.1) * mm});
            skLineSegment(sketch, "E2.9.2.2", {"start": v(58.34, 1501.1) * mm, "end": v(58.34, 1451.1) * mm});
            skLineSegment(sketch, "E2.9.2.3", {"start": v(58.34, 1501.1) * mm, "end": v(108.34, 1501.1) * mm});
            skLineSegment(sketch, "E2.9.3.0", {"start": v(108.34, 1441.1) * mm, "end": v(108.34, 1391.1) * mm});
            skLineSegment(sketch, "E2.9.3.1", {"start": v(58.34, 1391.1) * mm, "end": v(108.34, 1391.1) * mm});
            skLineSegment(sketch, "E2.9.3.2", {"start": v(58.34, 1441.1) * mm, "end": v(58.34, 1391.1) * mm});
            skLineSegment(sketch, "E2.9.3.3", {"start": v(58.34, 1441.1) * mm, "end": v(108.34, 1441.1) * mm});
            skLineSegment(sketch, "E2.9.4.0", {"start": v(108.34, 1381.1) * mm, "end": v(108.34, 1331.1) * mm});
            skLineSegment(sketch, "E2.9.4.1", {"start": v(58.34, 1331.1) * mm, "end": v(108.34, 1331.1) * mm});
            skLineSegment(sketch, "E2.9.4.2", {"start": v(58.34, 1381.1) * mm, "end": v(58.34, 1331.1) * mm});
            skLineSegment(sketch, "E2.9.4.3", {"start": v(58.34, 1381.1) * mm, "end": v(108.34, 1381.1) * mm});
            skLineSegment(sketch, "E2.9.5.0", {"start": v(108.34, 1321.1) * mm, "end": v(108.34, 1271.1) * mm});
            skLineSegment(sketch, "E2.9.5.1", {"start": v(58.34, 1271.1) * mm, "end": v(108.34, 1271.1) * mm});
            skLineSegment(sketch, "E2.9.5.2", {"start": v(58.34, 1321.1) * mm, "end": v(58.34, 1271.1) * mm});
            skLineSegment(sketch, "E2.9.5.3", {"start": v(58.34, 1321.1) * mm, "end": v(108.34, 1321.1) * mm});
            skLineSegment(sketch, "E2.9.6.0", {"start": v(108.34, 1261.1) * mm, "end": v(108.34, 1211.1) * mm});
            skLineSegment(sketch, "E2.9.6.1", {"start": v(58.34, 1211.1) * mm, "end": v(108.34, 1211.1) * mm});
            skLineSegment(sketch, "E2.9.6.2", {"start": v(58.34, 1261.1) * mm, "end": v(58.34, 1211.1) * mm});
            skLineSegment(sketch, "E2.9.6.3", {"start": v(58.34, 1261.1) * mm, "end": v(108.34, 1261.1) * mm});
            skLineSegment(sketch, "E2.9.7.0", {"start": v(108.34, 1201.1) * mm, "end": v(108.34, 1151.1) * mm});
            skLineSegment(sketch, "E2.9.7.1", {"start": v(58.34, 1151.1) * mm, "end": v(108.34, 1151.1) * mm});
            skLineSegment(sketch, "E2.9.7.2", {"start": v(58.34, 1201.1) * mm, "end": v(58.34, 1151.1) * mm});
            skLineSegment(sketch, "E2.9.7.3", {"start": v(58.34, 1201.1) * mm, "end": v(108.34, 1201.1) * mm});
            skLineSegment(sketch, "E2.9.8.0", {"start": v(108.34, 1141.1) * mm, "end": v(108.34, 1091.1) * mm});
            skLineSegment(sketch, "E2.9.8.1", {"start": v(58.34, 1091.1) * mm, "end": v(108.34, 1091.1) * mm});
            skLineSegment(sketch, "E2.9.8.2", {"start": v(58.34, 1141.1) * mm, "end": v(58.34, 1091.1) * mm});
            skLineSegment(sketch, "E2.9.8.3", {"start": v(58.34, 1141.1) * mm, "end": v(108.34, 1141.1) * mm});
            skLineSegment(sketch, "E2.9.9.0", {"start": v(108.34, 1081.1) * mm, "end": v(108.34, 1031.1) * mm});
            skLineSegment(sketch, "E2.9.9.1", {"start": v(58.34, 1031.1) * mm, "end": v(108.34, 1031.1) * mm});
            skLineSegment(sketch, "E2.9.9.2", {"start": v(58.34, 1081.1) * mm, "end": v(58.34, 1031.1) * mm});
            skLineSegment(sketch, "E2.9.9.3", {"start": v(58.34, 1081.1) * mm, "end": v(108.34, 1081.1) * mm});
            skLineSegment(sketch, "E2.9.10.0", {"start": v(108.34, 1021.1) * mm, "end": v(108.34, 971.1) * mm});
            skLineSegment(sketch, "E2.9.10.1", {"start": v(58.34, 971.1) * mm, "end": v(108.34, 971.1) * mm});
            skLineSegment(sketch, "E2.9.10.2", {"start": v(58.34, 1021.1) * mm, "end": v(58.34, 971.1) * mm});
            skLineSegment(sketch, "E2.9.10.3", {"start": v(58.34, 1021.1) * mm, "end": v(108.34, 1021.1) * mm});
            skLineSegment(sketch, "E2.9.11.0", {"start": v(108.34, 961.1) * mm, "end": v(108.34, 911.1) * mm});
            skLineSegment(sketch, "E2.9.11.1", {"start": v(58.34, 911.1) * mm, "end": v(108.34, 911.1) * mm});
            skLineSegment(sketch, "E2.9.11.2", {"start": v(58.34, 961.1) * mm, "end": v(58.34, 911.1) * mm});
            skLineSegment(sketch, "E2.9.11.3", {"start": v(58.34, 961.1) * mm, "end": v(108.34, 961.1) * mm});
            skLineSegment(sketch, "E2.9.12.0", {"start": v(108.34, 901.1) * mm, "end": v(108.34, 851.1) * mm});
            skLineSegment(sketch, "E2.9.12.1", {"start": v(58.34, 851.1) * mm, "end": v(108.34, 851.1) * mm});
            skLineSegment(sketch, "E2.9.12.2", {"start": v(58.34, 901.1) * mm, "end": v(58.34, 851.1) * mm});
            skLineSegment(sketch, "E2.9.12.3", {"start": v(58.34, 901.1) * mm, "end": v(108.34, 901.1) * mm});
            skLineSegment(sketch, "E2.9.13.0", {"start": v(108.34, 841.1) * mm, "end": v(108.34, 791.1) * mm});
            skLineSegment(sketch, "E2.9.13.1", {"start": v(58.34, 791.1) * mm, "end": v(108.34, 791.1) * mm});
            skLineSegment(sketch, "E2.9.13.2", {"start": v(58.34, 841.1) * mm, "end": v(58.34, 791.1) * mm});
            skLineSegment(sketch, "E2.9.13.3", {"start": v(58.34, 841.1) * mm, "end": v(108.34, 841.1) * mm});
            skLineSegment(sketch, "E2.9.14.0", {"start": v(108.34, 781.1) * mm, "end": v(108.34, 731.1) * mm});
            skLineSegment(sketch, "E2.9.14.1", {"start": v(58.34, 731.1) * mm, "end": v(108.34, 731.1) * mm});
            skLineSegment(sketch, "E2.9.14.2", {"start": v(58.34, 781.1) * mm, "end": v(58.34, 731.1) * mm});
            skLineSegment(sketch, "E2.9.14.3", {"start": v(58.34, 781.1) * mm, "end": v(108.34, 781.1) * mm});
            skLineSegment(sketch, "E2.9.15.0", {"start": v(108.34, 721.1) * mm, "end": v(108.34, 671.1) * mm});
            skLineSegment(sketch, "E2.9.15.1", {"start": v(58.34, 671.1) * mm, "end": v(108.34, 671.1) * mm});
            skLineSegment(sketch, "E2.9.15.2", {"start": v(58.34, 721.1) * mm, "end": v(58.34, 671.1) * mm});
            skLineSegment(sketch, "E2.9.15.3", {"start": v(58.34, 721.1) * mm, "end": v(108.34, 721.1) * mm});
            skLineSegment(sketch, "E2.9.16.0", {"start": v(108.34, 661.1) * mm, "end": v(108.34, 611.1) * mm});
            skLineSegment(sketch, "E2.9.16.1", {"start": v(58.34, 611.1) * mm, "end": v(108.34, 611.1) * mm});
            skLineSegment(sketch, "E2.9.16.2", {"start": v(58.34, 661.1) * mm, "end": v(58.34, 611.1) * mm});
            skLineSegment(sketch, "E2.9.16.3", {"start": v(58.34, 661.1) * mm, "end": v(108.34, 661.1) * mm});
            skLineSegment(sketch, "E2.9.17.0", {"start": v(108.34, 601.1) * mm, "end": v(108.34, 551.1) * mm});
            skLineSegment(sketch, "E2.9.17.1", {"start": v(58.34, 551.1) * mm, "end": v(108.34, 551.1) * mm});
            skLineSegment(sketch, "E2.9.17.2", {"start": v(58.34, 601.1) * mm, "end": v(58.34, 551.1) * mm});
            skLineSegment(sketch, "E2.9.17.3", {"start": v(58.34, 601.1) * mm, "end": v(108.34, 601.1) * mm});
            skLineSegment(sketch, "E2.9.18.0", {"start": v(108.34, 541.1) * mm, "end": v(108.34, 491.1) * mm});
            skLineSegment(sketch, "E2.9.18.1", {"start": v(58.34, 491.1) * mm, "end": v(108.34, 491.1) * mm});
            skLineSegment(sketch, "E2.9.18.2", {"start": v(58.34, 541.1) * mm, "end": v(58.34, 491.1) * mm});
            skLineSegment(sketch, "E2.9.18.3", {"start": v(58.34, 541.1) * mm, "end": v(108.34, 541.1) * mm});
            skLineSegment(sketch, "E2.9.19.0", {"start": v(108.34, 481.1) * mm, "end": v(108.34, 431.1) * mm});
            skLineSegment(sketch, "E2.9.19.1", {"start": v(58.34, 431.1) * mm, "end": v(108.34, 431.1) * mm});
            skLineSegment(sketch, "E2.9.19.2", {"start": v(58.34, 481.1) * mm, "end": v(58.34, 431.1) * mm});
            skLineSegment(sketch, "E2.9.19.3", {"start": v(58.34, 481.1) * mm, "end": v(108.34, 481.1) * mm});
            skLineSegment(sketch, "E2.9.20.0", {"start": v(108.34, 421.1) * mm, "end": v(108.34, 371.1) * mm});
            skLineSegment(sketch, "E2.9.20.1", {"start": v(58.34, 371.1) * mm, "end": v(108.34, 371.1) * mm});
            skLineSegment(sketch, "E2.9.20.2", {"start": v(58.34, 421.1) * mm, "end": v(58.34, 371.1) * mm});
            skLineSegment(sketch, "E2.9.20.3", {"start": v(58.34, 421.1) * mm, "end": v(108.34, 421.1) * mm});
            skLineSegment(sketch, "E2.9.21.0", {"start": v(108.34, 361.1) * mm, "end": v(108.34, 311.1) * mm});
            skLineSegment(sketch, "E2.9.21.1", {"start": v(58.34, 311.1) * mm, "end": v(108.34, 311.1) * mm});
            skLineSegment(sketch, "E2.9.21.2", {"start": v(58.34, 361.1) * mm, "end": v(58.34, 311.1) * mm});
            skLineSegment(sketch, "E2.9.21.3", {"start": v(58.34, 361.1) * mm, "end": v(108.34, 361.1) * mm});
            skLineSegment(sketch, "E2.9.22.0", {"start": v(108.34, 301.1) * mm, "end": v(108.34, 251.1) * mm});
            skLineSegment(sketch, "E2.9.22.1", {"start": v(58.34, 251.1) * mm, "end": v(108.34, 251.1) * mm});
            skLineSegment(sketch, "E2.9.22.2", {"start": v(58.34, 301.1) * mm, "end": v(58.34, 251.1) * mm});
            skLineSegment(sketch, "E2.9.22.3", {"start": v(58.34, 301.1) * mm, "end": v(108.34, 301.1) * mm});
            skLineSegment(sketch, "E2.9.23.0", {"start": v(108.34, 241.1) * mm, "end": v(108.34, 191.1) * mm});
            skLineSegment(sketch, "E2.9.23.1", {"start": v(58.34, 191.1) * mm, "end": v(108.34, 191.1) * mm});
            skLineSegment(sketch, "E2.9.23.2", {"start": v(58.34, 241.1) * mm, "end": v(58.34, 191.1) * mm});
            skLineSegment(sketch, "E2.9.23.3", {"start": v(58.34, 241.1) * mm, "end": v(108.34, 241.1) * mm});
            skLineSegment(sketch, "E2.9.24.0", {"start": v(108.34, 181.1) * mm, "end": v(108.34, 131.1) * mm});
            skLineSegment(sketch, "E2.9.24.1", {"start": v(58.34, 131.1) * mm, "end": v(108.34, 131.1) * mm});
            skLineSegment(sketch, "E2.9.24.2", {"start": v(58.34, 181.1) * mm, "end": v(58.34, 131.1) * mm});
            skLineSegment(sketch, "E2.9.24.3", {"start": v(58.34, 181.1) * mm, "end": v(108.34, 181.1) * mm});
            skLineSegment(sketch, "E2.9.25.0", {"start": v(108.34, 121.1) * mm, "end": v(108.34, 71.1) * mm});
            skLineSegment(sketch, "E2.9.25.1", {"start": v(58.34, 71.1) * mm, "end": v(108.34, 71.1) * mm});
            skLineSegment(sketch, "E2.9.25.2", {"start": v(58.34, 121.1) * mm, "end": v(58.34, 71.1) * mm});
            skLineSegment(sketch, "E2.9.25.3", {"start": v(58.34, 121.1) * mm, "end": v(108.34, 121.1) * mm});
            skLineSegment(sketch, "E2.9.26.0", {"start": v(108.34, 61.1) * mm, "end": v(108.34, 11.1) * mm});
            skLineSegment(sketch, "E2.9.26.1", {"start": v(58.34, 11.1) * mm, "end": v(108.34, 11.1) * mm});
            skLineSegment(sketch, "E2.9.26.2", {"start": v(58.34, 61.1) * mm, "end": v(58.34, 11.1) * mm});
            skLineSegment(sketch, "E2.9.26.3", {"start": v(58.34, 61.1) * mm, "end": v(108.34, 61.1) * mm});
            skLineSegment(sketch, "E2.9.27.0", {"start": v(108.34, 1.1) * mm, "end": v(108.34, -48.9) * mm});
            skLineSegment(sketch, "E2.9.27.1", {"start": v(58.34, -48.9) * mm, "end": v(108.34, -48.9) * mm});
            skLineSegment(sketch, "E2.9.27.2", {"start": v(58.34, 1.1) * mm, "end": v(58.34, -48.9) * mm});
            skLineSegment(sketch, "E2.9.27.3", {"start": v(58.34, 1.1) * mm, "end": v(108.34, 1.1) * mm});
            skLineSegment(sketch, "E2.9.28.0", {"start": v(108.34, -58.9) * mm, "end": v(108.34, -108.9) * mm});
            skLineSegment(sketch, "E2.9.28.1", {"start": v(58.34, -108.9) * mm, "end": v(108.34, -108.9) * mm});
            skLineSegment(sketch, "E2.9.28.2", {"start": v(58.34, -58.9) * mm, "end": v(58.34, -108.9) * mm});
            skLineSegment(sketch, "E2.9.28.3", {"start": v(58.34, -58.9) * mm, "end": v(108.34, -58.9) * mm});
            skLineSegment(sketch, "E2.9.29.0", {"start": v(108.34, -118.9) * mm, "end": v(108.34, -168.9) * mm});
            skLineSegment(sketch, "E2.9.29.1", {"start": v(58.34, -168.9) * mm, "end": v(108.34, -168.9) * mm});
            skLineSegment(sketch, "E2.9.29.2", {"start": v(58.34, -118.9) * mm, "end": v(58.34, -168.9) * mm});
            skLineSegment(sketch, "E2.9.29.3", {"start": v(58.34, -118.9) * mm, "end": v(108.34, -118.9) * mm});
            skLineSegment(sketch, "E2.9.30.0", {"start": v(108.34, -178.9) * mm, "end": v(108.34, -228.9) * mm});
            skLineSegment(sketch, "E2.9.30.1", {"start": v(58.34, -228.9) * mm, "end": v(108.34, -228.9) * mm});
            skLineSegment(sketch, "E2.9.30.2", {"start": v(58.34, -178.9) * mm, "end": v(58.34, -228.9) * mm});
            skLineSegment(sketch, "E2.9.30.3", {"start": v(58.34, -178.9) * mm, "end": v(108.34, -178.9) * mm});
            skLineSegment(sketch, "E2.9.31.0", {"start": v(108.34, -238.9) * mm, "end": v(108.34, -288.9) * mm});
            skLineSegment(sketch, "E2.9.31.1", {"start": v(58.34, -288.9) * mm, "end": v(108.34, -288.9) * mm});
            skLineSegment(sketch, "E2.9.31.2", {"start": v(58.34, -238.9) * mm, "end": v(58.34, -288.9) * mm});
            skLineSegment(sketch, "E2.9.31.3", {"start": v(58.34, -238.9) * mm, "end": v(108.34, -238.9) * mm});
            skLineSegment(sketch, "E2.9.32.0", {"start": v(108.34, -298.9) * mm, "end": v(108.34, -348.9) * mm});
            skLineSegment(sketch, "E2.9.32.1", {"start": v(58.34, -348.9) * mm, "end": v(108.34, -348.9) * mm});
            skLineSegment(sketch, "E2.9.32.2", {"start": v(58.34, -298.9) * mm, "end": v(58.34, -348.9) * mm});
            skLineSegment(sketch, "E2.9.32.3", {"start": v(58.34, -298.9) * mm, "end": v(108.34, -298.9) * mm});
            skLineSegment(sketch, "E2.10.0.0", {"start": v(168.34, 1621.1) * mm, "end": v(168.34, 1571.1) * mm});
            skLineSegment(sketch, "E2.10.0.1", {"start": v(118.34, 1571.1) * mm, "end": v(168.34, 1571.1) * mm});
            skLineSegment(sketch, "E2.10.0.2", {"start": v(118.34, 1621.1) * mm, "end": v(118.34, 1571.1) * mm});
            skLineSegment(sketch, "E2.10.0.3", {"start": v(118.34, 1621.1) * mm, "end": v(168.34, 1621.1) * mm});
            skLineSegment(sketch, "E2.10.1.0", {"start": v(168.34, 1561.1) * mm, "end": v(168.34, 1511.1) * mm});
            skLineSegment(sketch, "E2.10.1.1", {"start": v(118.34, 1511.1) * mm, "end": v(168.34, 1511.1) * mm});
            skLineSegment(sketch, "E2.10.1.2", {"start": v(118.34, 1561.1) * mm, "end": v(118.34, 1511.1) * mm});
            skLineSegment(sketch, "E2.10.1.3", {"start": v(118.34, 1561.1) * mm, "end": v(168.34, 1561.1) * mm});
            skLineSegment(sketch, "E2.10.2.0", {"start": v(168.34, 1501.1) * mm, "end": v(168.34, 1451.1) * mm});
            skLineSegment(sketch, "E2.10.2.1", {"start": v(118.34, 1451.1) * mm, "end": v(168.34, 1451.1) * mm});
            skLineSegment(sketch, "E2.10.2.2", {"start": v(118.34, 1501.1) * mm, "end": v(118.34, 1451.1) * mm});
            skLineSegment(sketch, "E2.10.2.3", {"start": v(118.34, 1501.1) * mm, "end": v(168.34, 1501.1) * mm});
            skLineSegment(sketch, "E2.10.3.0", {"start": v(168.34, 1441.1) * mm, "end": v(168.34, 1391.1) * mm});
            skLineSegment(sketch, "E2.10.3.1", {"start": v(118.34, 1391.1) * mm, "end": v(168.34, 1391.1) * mm});
            skLineSegment(sketch, "E2.10.3.2", {"start": v(118.34, 1441.1) * mm, "end": v(118.34, 1391.1) * mm});
            skLineSegment(sketch, "E2.10.3.3", {"start": v(118.34, 1441.1) * mm, "end": v(168.34, 1441.1) * mm});
            skLineSegment(sketch, "E2.10.4.0", {"start": v(168.34, 1381.1) * mm, "end": v(168.34, 1331.1) * mm});
            skLineSegment(sketch, "E2.10.4.1", {"start": v(118.34, 1331.1) * mm, "end": v(168.34, 1331.1) * mm});
            skLineSegment(sketch, "E2.10.4.2", {"start": v(118.34, 1381.1) * mm, "end": v(118.34, 1331.1) * mm});
            skLineSegment(sketch, "E2.10.4.3", {"start": v(118.34, 1381.1) * mm, "end": v(168.34, 1381.1) * mm});
            skLineSegment(sketch, "E2.10.5.0", {"start": v(168.34, 1321.1) * mm, "end": v(168.34, 1271.1) * mm});
            skLineSegment(sketch, "E2.10.5.1", {"start": v(118.34, 1271.1) * mm, "end": v(168.34, 1271.1) * mm});
            skLineSegment(sketch, "E2.10.5.2", {"start": v(118.34, 1321.1) * mm, "end": v(118.34, 1271.1) * mm});
            skLineSegment(sketch, "E2.10.5.3", {"start": v(118.34, 1321.1) * mm, "end": v(168.34, 1321.1) * mm});
            skLineSegment(sketch, "E2.10.6.0", {"start": v(168.34, 1261.1) * mm, "end": v(168.34, 1211.1) * mm});
            skLineSegment(sketch, "E2.10.6.1", {"start": v(118.34, 1211.1) * mm, "end": v(168.34, 1211.1) * mm});
            skLineSegment(sketch, "E2.10.6.2", {"start": v(118.34, 1261.1) * mm, "end": v(118.34, 1211.1) * mm});
            skLineSegment(sketch, "E2.10.6.3", {"start": v(118.34, 1261.1) * mm, "end": v(168.34, 1261.1) * mm});
            skLineSegment(sketch, "E2.10.7.0", {"start": v(168.34, 1201.1) * mm, "end": v(168.34, 1151.1) * mm});
            skLineSegment(sketch, "E2.10.7.1", {"start": v(118.34, 1151.1) * mm, "end": v(168.34, 1151.1) * mm});
            skLineSegment(sketch, "E2.10.7.2", {"start": v(118.34, 1201.1) * mm, "end": v(118.34, 1151.1) * mm});
            skLineSegment(sketch, "E2.10.7.3", {"start": v(118.34, 1201.1) * mm, "end": v(168.34, 1201.1) * mm});
            skLineSegment(sketch, "E2.10.8.0", {"start": v(168.34, 1141.1) * mm, "end": v(168.34, 1091.1) * mm});
            skLineSegment(sketch, "E2.10.8.1", {"start": v(118.34, 1091.1) * mm, "end": v(168.34, 1091.1) * mm});
            skLineSegment(sketch, "E2.10.8.2", {"start": v(118.34, 1141.1) * mm, "end": v(118.34, 1091.1) * mm});
            skLineSegment(sketch, "E2.10.8.3", {"start": v(118.34, 1141.1) * mm, "end": v(168.34, 1141.1) * mm});
            skLineSegment(sketch, "E2.10.9.0", {"start": v(168.34, 1081.1) * mm, "end": v(168.34, 1031.1) * mm});
            skLineSegment(sketch, "E2.10.9.1", {"start": v(118.34, 1031.1) * mm, "end": v(168.34, 1031.1) * mm});
            skLineSegment(sketch, "E2.10.9.2", {"start": v(118.34, 1081.1) * mm, "end": v(118.34, 1031.1) * mm});
            skLineSegment(sketch, "E2.10.9.3", {"start": v(118.34, 1081.1) * mm, "end": v(168.34, 1081.1) * mm});
            skLineSegment(sketch, "E2.10.10.0", {"start": v(168.34, 1021.1) * mm, "end": v(168.34, 971.1) * mm});
            skLineSegment(sketch, "E2.10.10.1", {"start": v(118.34, 971.1) * mm, "end": v(168.34, 971.1) * mm});
            skLineSegment(sketch, "E2.10.10.2", {"start": v(118.34, 1021.1) * mm, "end": v(118.34, 971.1) * mm});
            skLineSegment(sketch, "E2.10.10.3", {"start": v(118.34, 1021.1) * mm, "end": v(168.34, 1021.1) * mm});
            skLineSegment(sketch, "E2.10.11.0", {"start": v(168.34, 961.1) * mm, "end": v(168.34, 911.1) * mm});
            skLineSegment(sketch, "E2.10.11.1", {"start": v(118.34, 911.1) * mm, "end": v(168.34, 911.1) * mm});
            skLineSegment(sketch, "E2.10.11.2", {"start": v(118.34, 961.1) * mm, "end": v(118.34, 911.1) * mm});
            skLineSegment(sketch, "E2.10.11.3", {"start": v(118.34, 961.1) * mm, "end": v(168.34, 961.1) * mm});
            skLineSegment(sketch, "E2.10.12.0", {"start": v(168.34, 901.1) * mm, "end": v(168.34, 851.1) * mm});
            skLineSegment(sketch, "E2.10.12.1", {"start": v(118.34, 851.1) * mm, "end": v(168.34, 851.1) * mm});
            skLineSegment(sketch, "E2.10.12.2", {"start": v(118.34, 901.1) * mm, "end": v(118.34, 851.1) * mm});
            skLineSegment(sketch, "E2.10.12.3", {"start": v(118.34, 901.1) * mm, "end": v(168.34, 901.1) * mm});
            skLineSegment(sketch, "E2.10.13.0", {"start": v(168.34, 841.1) * mm, "end": v(168.34, 791.1) * mm});
            skLineSegment(sketch, "E2.10.13.1", {"start": v(118.34, 791.1) * mm, "end": v(168.34, 791.1) * mm});
            skLineSegment(sketch, "E2.10.13.2", {"start": v(118.34, 841.1) * mm, "end": v(118.34, 791.1) * mm});
            skLineSegment(sketch, "E2.10.13.3", {"start": v(118.34, 841.1) * mm, "end": v(168.34, 841.1) * mm});
            skLineSegment(sketch, "E2.10.14.0", {"start": v(168.34, 781.1) * mm, "end": v(168.34, 731.1) * mm});
            skLineSegment(sketch, "E2.10.14.1", {"start": v(118.34, 731.1) * mm, "end": v(168.34, 731.1) * mm});
            skLineSegment(sketch, "E2.10.14.2", {"start": v(118.34, 781.1) * mm, "end": v(118.34, 731.1) * mm});
            skLineSegment(sketch, "E2.10.14.3", {"start": v(118.34, 781.1) * mm, "end": v(168.34, 781.1) * mm});
            skLineSegment(sketch, "E2.10.15.0", {"start": v(168.34, 721.1) * mm, "end": v(168.34, 671.1) * mm});
            skLineSegment(sketch, "E2.10.15.1", {"start": v(118.34, 671.1) * mm, "end": v(168.34, 671.1) * mm});
            skLineSegment(sketch, "E2.10.15.2", {"start": v(118.34, 721.1) * mm, "end": v(118.34, 671.1) * mm});
            skLineSegment(sketch, "E2.10.15.3", {"start": v(118.34, 721.1) * mm, "end": v(168.34, 721.1) * mm});
            skLineSegment(sketch, "E2.10.16.0", {"start": v(168.34, 661.1) * mm, "end": v(168.34, 611.1) * mm});
            skLineSegment(sketch, "E2.10.16.1", {"start": v(118.34, 611.1) * mm, "end": v(168.34, 611.1) * mm});
            skLineSegment(sketch, "E2.10.16.2", {"start": v(118.34, 661.1) * mm, "end": v(118.34, 611.1) * mm});
            skLineSegment(sketch, "E2.10.16.3", {"start": v(118.34, 661.1) * mm, "end": v(168.34, 661.1) * mm});
            skLineSegment(sketch, "E2.10.17.0", {"start": v(168.34, 601.1) * mm, "end": v(168.34, 551.1) * mm});
            skLineSegment(sketch, "E2.10.17.1", {"start": v(118.34, 551.1) * mm, "end": v(168.34, 551.1) * mm});
            skLineSegment(sketch, "E2.10.17.2", {"start": v(118.34, 601.1) * mm, "end": v(118.34, 551.1) * mm});
            skLineSegment(sketch, "E2.10.17.3", {"start": v(118.34, 601.1) * mm, "end": v(168.34, 601.1) * mm});
            skLineSegment(sketch, "E2.10.18.0", {"start": v(168.34, 541.1) * mm, "end": v(168.34, 491.1) * mm});
            skLineSegment(sketch, "E2.10.18.1", {"start": v(118.34, 491.1) * mm, "end": v(168.34, 491.1) * mm});
            skLineSegment(sketch, "E2.10.18.2", {"start": v(118.34, 541.1) * mm, "end": v(118.34, 491.1) * mm});
            skLineSegment(sketch, "E2.10.18.3", {"start": v(118.34, 541.1) * mm, "end": v(168.34, 541.1) * mm});
            skLineSegment(sketch, "E2.10.19.0", {"start": v(168.34, 481.1) * mm, "end": v(168.34, 431.1) * mm});
            skLineSegment(sketch, "E2.10.19.1", {"start": v(118.34, 431.1) * mm, "end": v(168.34, 431.1) * mm});
            skLineSegment(sketch, "E2.10.19.2", {"start": v(118.34, 481.1) * mm, "end": v(118.34, 431.1) * mm});
            skLineSegment(sketch, "E2.10.19.3", {"start": v(118.34, 481.1) * mm, "end": v(168.34, 481.1) * mm});
            skLineSegment(sketch, "E2.10.20.0", {"start": v(168.34, 421.1) * mm, "end": v(168.34, 371.1) * mm});
            skLineSegment(sketch, "E2.10.20.1", {"start": v(118.34, 371.1) * mm, "end": v(168.34, 371.1) * mm});
            skLineSegment(sketch, "E2.10.20.2", {"start": v(118.34, 421.1) * mm, "end": v(118.34, 371.1) * mm});
            skLineSegment(sketch, "E2.10.20.3", {"start": v(118.34, 421.1) * mm, "end": v(168.34, 421.1) * mm});
            skLineSegment(sketch, "E2.10.21.0", {"start": v(168.34, 361.1) * mm, "end": v(168.34, 311.1) * mm});
            skLineSegment(sketch, "E2.10.21.1", {"start": v(118.34, 311.1) * mm, "end": v(168.34, 311.1) * mm});
            skLineSegment(sketch, "E2.10.21.2", {"start": v(118.34, 361.1) * mm, "end": v(118.34, 311.1) * mm});
            skLineSegment(sketch, "E2.10.21.3", {"start": v(118.34, 361.1) * mm, "end": v(168.34, 361.1) * mm});
            skLineSegment(sketch, "E2.10.22.0", {"start": v(168.34, 301.1) * mm, "end": v(168.34, 251.1) * mm});
            skLineSegment(sketch, "E2.10.22.1", {"start": v(118.34, 251.1) * mm, "end": v(168.34, 251.1) * mm});
            skLineSegment(sketch, "E2.10.22.2", {"start": v(118.34, 301.1) * mm, "end": v(118.34, 251.1) * mm});
            skLineSegment(sketch, "E2.10.22.3", {"start": v(118.34, 301.1) * mm, "end": v(168.34, 301.1) * mm});
            skLineSegment(sketch, "E2.10.23.0", {"start": v(168.34, 241.1) * mm, "end": v(168.34, 191.1) * mm});
            skLineSegment(sketch, "E2.10.23.1", {"start": v(118.34, 191.1) * mm, "end": v(168.34, 191.1) * mm});
            skLineSegment(sketch, "E2.10.23.2", {"start": v(118.34, 241.1) * mm, "end": v(118.34, 191.1) * mm});
            skLineSegment(sketch, "E2.10.23.3", {"start": v(118.34, 241.1) * mm, "end": v(168.34, 241.1) * mm});
            skLineSegment(sketch, "E2.10.24.0", {"start": v(168.34, 181.1) * mm, "end": v(168.34, 131.1) * mm});
            skLineSegment(sketch, "E2.10.24.1", {"start": v(118.34, 131.1) * mm, "end": v(168.34, 131.1) * mm});
            skLineSegment(sketch, "E2.10.24.2", {"start": v(118.34, 181.1) * mm, "end": v(118.34, 131.1) * mm});
            skLineSegment(sketch, "E2.10.24.3", {"start": v(118.34, 181.1) * mm, "end": v(168.34, 181.1) * mm});
            skLineSegment(sketch, "E2.10.25.0", {"start": v(168.34, 121.1) * mm, "end": v(168.34, 71.1) * mm});
            skLineSegment(sketch, "E2.10.25.1", {"start": v(118.34, 71.1) * mm, "end": v(168.34, 71.1) * mm});
            skLineSegment(sketch, "E2.10.25.2", {"start": v(118.34, 121.1) * mm, "end": v(118.34, 71.1) * mm});
            skLineSegment(sketch, "E2.10.25.3", {"start": v(118.34, 121.1) * mm, "end": v(168.34, 121.1) * mm});
            skLineSegment(sketch, "E2.10.26.0", {"start": v(168.34, 61.1) * mm, "end": v(168.34, 11.1) * mm});
            skLineSegment(sketch, "E2.10.26.1", {"start": v(118.34, 11.1) * mm, "end": v(168.34, 11.1) * mm});
            skLineSegment(sketch, "E2.10.26.2", {"start": v(118.34, 61.1) * mm, "end": v(118.34, 11.1) * mm});
            skLineSegment(sketch, "E2.10.26.3", {"start": v(118.34, 61.1) * mm, "end": v(168.34, 61.1) * mm});
            skLineSegment(sketch, "E2.10.27.0", {"start": v(168.34, 1.1) * mm, "end": v(168.34, -48.9) * mm});
            skLineSegment(sketch, "E2.10.27.1", {"start": v(118.34, -48.9) * mm, "end": v(168.34, -48.9) * mm});
            skLineSegment(sketch, "E2.10.27.2", {"start": v(118.34, 1.1) * mm, "end": v(118.34, -48.9) * mm});
            skLineSegment(sketch, "E2.10.27.3", {"start": v(118.34, 1.1) * mm, "end": v(168.34, 1.1) * mm});
            skLineSegment(sketch, "E2.10.28.0", {"start": v(168.34, -58.9) * mm, "end": v(168.34, -108.9) * mm});
            skLineSegment(sketch, "E2.10.28.1", {"start": v(118.34, -108.9) * mm, "end": v(168.34, -108.9) * mm});
            skLineSegment(sketch, "E2.10.28.2", {"start": v(118.34, -58.9) * mm, "end": v(118.34, -108.9) * mm});
            skLineSegment(sketch, "E2.10.28.3", {"start": v(118.34, -58.9) * mm, "end": v(168.34, -58.9) * mm});
            skLineSegment(sketch, "E2.10.29.0", {"start": v(168.34, -118.9) * mm, "end": v(168.34, -168.9) * mm});
            skLineSegment(sketch, "E2.10.29.1", {"start": v(118.34, -168.9) * mm, "end": v(168.34, -168.9) * mm});
            skLineSegment(sketch, "E2.10.29.2", {"start": v(118.34, -118.9) * mm, "end": v(118.34, -168.9) * mm});
            skLineSegment(sketch, "E2.10.29.3", {"start": v(118.34, -118.9) * mm, "end": v(168.34, -118.9) * mm});
            skLineSegment(sketch, "E2.10.30.0", {"start": v(168.34, -178.9) * mm, "end": v(168.34, -228.9) * mm});
            skLineSegment(sketch, "E2.10.30.1", {"start": v(118.34, -228.9) * mm, "end": v(168.34, -228.9) * mm});
            skLineSegment(sketch, "E2.10.30.2", {"start": v(118.34, -178.9) * mm, "end": v(118.34, -228.9) * mm});
            skLineSegment(sketch, "E2.10.30.3", {"start": v(118.34, -178.9) * mm, "end": v(168.34, -178.9) * mm});
            skLineSegment(sketch, "E2.10.31.0", {"start": v(168.34, -238.9) * mm, "end": v(168.34, -288.9) * mm});
            skLineSegment(sketch, "E2.10.31.1", {"start": v(118.34, -288.9) * mm, "end": v(168.34, -288.9) * mm});
            skLineSegment(sketch, "E2.10.31.2", {"start": v(118.34, -238.9) * mm, "end": v(118.34, -288.9) * mm});
            skLineSegment(sketch, "E2.10.31.3", {"start": v(118.34, -238.9) * mm, "end": v(168.34, -238.9) * mm});
            skLineSegment(sketch, "E2.10.32.0", {"start": v(168.34, -298.9) * mm, "end": v(168.34, -348.9) * mm});
            skLineSegment(sketch, "E2.10.32.1", {"start": v(118.34, -348.9) * mm, "end": v(168.34, -348.9) * mm});
            skLineSegment(sketch, "E2.10.32.2", {"start": v(118.34, -298.9) * mm, "end": v(118.34, -348.9) * mm});
            skLineSegment(sketch, "E2.10.32.3", {"start": v(118.34, -298.9) * mm, "end": v(168.34, -298.9) * mm});
            skLineSegment(sketch, "E2.11.0.0", {"start": v(228.34, 1621.1) * mm, "end": v(228.34, 1571.1) * mm});
            skLineSegment(sketch, "E2.11.0.1", {"start": v(178.34, 1571.1) * mm, "end": v(228.34, 1571.1) * mm});
            skLineSegment(sketch, "E2.11.0.2", {"start": v(178.34, 1621.1) * mm, "end": v(178.34, 1571.1) * mm});
            skLineSegment(sketch, "E2.11.0.3", {"start": v(178.34, 1621.1) * mm, "end": v(228.34, 1621.1) * mm});
            skLineSegment(sketch, "E2.11.1.0", {"start": v(228.34, 1561.1) * mm, "end": v(228.34, 1511.1) * mm});
            skLineSegment(sketch, "E2.11.1.1", {"start": v(178.34, 1511.1) * mm, "end": v(228.34, 1511.1) * mm});
            skLineSegment(sketch, "E2.11.1.2", {"start": v(178.34, 1561.1) * mm, "end": v(178.34, 1511.1) * mm});
            skLineSegment(sketch, "E2.11.1.3", {"start": v(178.34, 1561.1) * mm, "end": v(228.34, 1561.1) * mm});
            skLineSegment(sketch, "E2.11.2.0", {"start": v(228.34, 1501.1) * mm, "end": v(228.34, 1451.1) * mm});
            skLineSegment(sketch, "E2.11.2.1", {"start": v(178.34, 1451.1) * mm, "end": v(228.34, 1451.1) * mm});
            skLineSegment(sketch, "E2.11.2.2", {"start": v(178.34, 1501.1) * mm, "end": v(178.34, 1451.1) * mm});
            skLineSegment(sketch, "E2.11.2.3", {"start": v(178.34, 1501.1) * mm, "end": v(228.34, 1501.1) * mm});
            skLineSegment(sketch, "E2.11.3.0", {"start": v(228.34, 1441.1) * mm, "end": v(228.34, 1391.1) * mm});
            skLineSegment(sketch, "E2.11.3.1", {"start": v(178.34, 1391.1) * mm, "end": v(228.34, 1391.1) * mm});
            skLineSegment(sketch, "E2.11.3.2", {"start": v(178.34, 1441.1) * mm, "end": v(178.34, 1391.1) * mm});
            skLineSegment(sketch, "E2.11.3.3", {"start": v(178.34, 1441.1) * mm, "end": v(228.34, 1441.1) * mm});
            skLineSegment(sketch, "E2.11.4.0", {"start": v(228.34, 1381.1) * mm, "end": v(228.34, 1331.1) * mm});
            skLineSegment(sketch, "E2.11.4.1", {"start": v(178.34, 1331.1) * mm, "end": v(228.34, 1331.1) * mm});
            skLineSegment(sketch, "E2.11.4.2", {"start": v(178.34, 1381.1) * mm, "end": v(178.34, 1331.1) * mm});
            skLineSegment(sketch, "E2.11.4.3", {"start": v(178.34, 1381.1) * mm, "end": v(228.34, 1381.1) * mm});
            skLineSegment(sketch, "E2.11.5.0", {"start": v(228.34, 1321.1) * mm, "end": v(228.34, 1271.1) * mm});
            skLineSegment(sketch, "E2.11.5.1", {"start": v(178.34, 1271.1) * mm, "end": v(228.34, 1271.1) * mm});
            skLineSegment(sketch, "E2.11.5.2", {"start": v(178.34, 1321.1) * mm, "end": v(178.34, 1271.1) * mm});
            skLineSegment(sketch, "E2.11.5.3", {"start": v(178.34, 1321.1) * mm, "end": v(228.34, 1321.1) * mm});
            skLineSegment(sketch, "E2.11.6.0", {"start": v(228.34, 1261.1) * mm, "end": v(228.34, 1211.1) * mm});
            skLineSegment(sketch, "E2.11.6.1", {"start": v(178.34, 1211.1) * mm, "end": v(228.34, 1211.1) * mm});
            skLineSegment(sketch, "E2.11.6.2", {"start": v(178.34, 1261.1) * mm, "end": v(178.34, 1211.1) * mm});
            skLineSegment(sketch, "E2.11.6.3", {"start": v(178.34, 1261.1) * mm, "end": v(228.34, 1261.1) * mm});
            skLineSegment(sketch, "E2.11.7.0", {"start": v(228.34, 1201.1) * mm, "end": v(228.34, 1151.1) * mm});
            skLineSegment(sketch, "E2.11.7.1", {"start": v(178.34, 1151.1) * mm, "end": v(228.34, 1151.1) * mm});
            skLineSegment(sketch, "E2.11.7.2", {"start": v(178.34, 1201.1) * mm, "end": v(178.34, 1151.1) * mm});
            skLineSegment(sketch, "E2.11.7.3", {"start": v(178.34, 1201.1) * mm, "end": v(228.34, 1201.1) * mm});
            skLineSegment(sketch, "E2.11.8.0", {"start": v(228.34, 1141.1) * mm, "end": v(228.34, 1091.1) * mm});
            skLineSegment(sketch, "E2.11.8.1", {"start": v(178.34, 1091.1) * mm, "end": v(228.34, 1091.1) * mm});
            skLineSegment(sketch, "E2.11.8.2", {"start": v(178.34, 1141.1) * mm, "end": v(178.34, 1091.1) * mm});
            skLineSegment(sketch, "E2.11.8.3", {"start": v(178.34, 1141.1) * mm, "end": v(228.34, 1141.1) * mm});
            skLineSegment(sketch, "E2.11.9.0", {"start": v(228.34, 1081.1) * mm, "end": v(228.34, 1031.1) * mm});
            skLineSegment(sketch, "E2.11.9.1", {"start": v(178.34, 1031.1) * mm, "end": v(228.34, 1031.1) * mm});
            skLineSegment(sketch, "E2.11.9.2", {"start": v(178.34, 1081.1) * mm, "end": v(178.34, 1031.1) * mm});
            skLineSegment(sketch, "E2.11.9.3", {"start": v(178.34, 1081.1) * mm, "end": v(228.34, 1081.1) * mm});
            skLineSegment(sketch, "E2.11.10.0", {"start": v(228.34, 1021.1) * mm, "end": v(228.34, 971.1) * mm});
            skLineSegment(sketch, "E2.11.10.1", {"start": v(178.34, 971.1) * mm, "end": v(228.34, 971.1) * mm});
            skLineSegment(sketch, "E2.11.10.2", {"start": v(178.34, 1021.1) * mm, "end": v(178.34, 971.1) * mm});
            skLineSegment(sketch, "E2.11.10.3", {"start": v(178.34, 1021.1) * mm, "end": v(228.34, 1021.1) * mm});
            skLineSegment(sketch, "E2.11.11.0", {"start": v(228.34, 961.1) * mm, "end": v(228.34, 911.1) * mm});
            skLineSegment(sketch, "E2.11.11.1", {"start": v(178.34, 911.1) * mm, "end": v(228.34, 911.1) * mm});
            skLineSegment(sketch, "E2.11.11.2", {"start": v(178.34, 961.1) * mm, "end": v(178.34, 911.1) * mm});
            skLineSegment(sketch, "E2.11.11.3", {"start": v(178.34, 961.1) * mm, "end": v(228.34, 961.1) * mm});
            skLineSegment(sketch, "E2.11.12.0", {"start": v(228.34, 901.1) * mm, "end": v(228.34, 851.1) * mm});
            skLineSegment(sketch, "E2.11.12.1", {"start": v(178.34, 851.1) * mm, "end": v(228.34, 851.1) * mm});
            skLineSegment(sketch, "E2.11.12.2", {"start": v(178.34, 901.1) * mm, "end": v(178.34, 851.1) * mm});
            skLineSegment(sketch, "E2.11.12.3", {"start": v(178.34, 901.1) * mm, "end": v(228.34, 901.1) * mm});
            skLineSegment(sketch, "E2.11.13.0", {"start": v(228.34, 841.1) * mm, "end": v(228.34, 791.1) * mm});
            skLineSegment(sketch, "E2.11.13.1", {"start": v(178.34, 791.1) * mm, "end": v(228.34, 791.1) * mm});
            skLineSegment(sketch, "E2.11.13.2", {"start": v(178.34, 841.1) * mm, "end": v(178.34, 791.1) * mm});
            skLineSegment(sketch, "E2.11.13.3", {"start": v(178.34, 841.1) * mm, "end": v(228.34, 841.1) * mm});
            skLineSegment(sketch, "E2.11.14.0", {"start": v(228.34, 781.1) * mm, "end": v(228.34, 731.1) * mm});
            skLineSegment(sketch, "E2.11.14.1", {"start": v(178.34, 731.1) * mm, "end": v(228.34, 731.1) * mm});
            skLineSegment(sketch, "E2.11.14.2", {"start": v(178.34, 781.1) * mm, "end": v(178.34, 731.1) * mm});
            skLineSegment(sketch, "E2.11.14.3", {"start": v(178.34, 781.1) * mm, "end": v(228.34, 781.1) * mm});
            skLineSegment(sketch, "E2.11.15.0", {"start": v(228.34, 721.1) * mm, "end": v(228.34, 671.1) * mm});
            skLineSegment(sketch, "E2.11.15.1", {"start": v(178.34, 671.1) * mm, "end": v(228.34, 671.1) * mm});
            skLineSegment(sketch, "E2.11.15.2", {"start": v(178.34, 721.1) * mm, "end": v(178.34, 671.1) * mm});
            skLineSegment(sketch, "E2.11.15.3", {"start": v(178.34, 721.1) * mm, "end": v(228.34, 721.1) * mm});
            skLineSegment(sketch, "E2.11.16.0", {"start": v(228.34, 661.1) * mm, "end": v(228.34, 611.1) * mm});
            skLineSegment(sketch, "E2.11.16.1", {"start": v(178.34, 611.1) * mm, "end": v(228.34, 611.1) * mm});
            skLineSegment(sketch, "E2.11.16.2", {"start": v(178.34, 661.1) * mm, "end": v(178.34, 611.1) * mm});
            skLineSegment(sketch, "E2.11.16.3", {"start": v(178.34, 661.1) * mm, "end": v(228.34, 661.1) * mm});
            skLineSegment(sketch, "E2.11.17.0", {"start": v(228.34, 601.1) * mm, "end": v(228.34, 551.1) * mm});
            skLineSegment(sketch, "E2.11.17.1", {"start": v(178.34, 551.1) * mm, "end": v(228.34, 551.1) * mm});
            skLineSegment(sketch, "E2.11.17.2", {"start": v(178.34, 601.1) * mm, "end": v(178.34, 551.1) * mm});
            skLineSegment(sketch, "E2.11.17.3", {"start": v(178.34, 601.1) * mm, "end": v(228.34, 601.1) * mm});
            skLineSegment(sketch, "E2.11.18.0", {"start": v(228.34, 541.1) * mm, "end": v(228.34, 491.1) * mm});
            skLineSegment(sketch, "E2.11.18.1", {"start": v(178.34, 491.1) * mm, "end": v(228.34, 491.1) * mm});
            skLineSegment(sketch, "E2.11.18.2", {"start": v(178.34, 541.1) * mm, "end": v(178.34, 491.1) * mm});
            skLineSegment(sketch, "E2.11.18.3", {"start": v(178.34, 541.1) * mm, "end": v(228.34, 541.1) * mm});
            skLineSegment(sketch, "E2.11.19.0", {"start": v(228.34, 481.1) * mm, "end": v(228.34, 431.1) * mm});
            skLineSegment(sketch, "E2.11.19.1", {"start": v(178.34, 431.1) * mm, "end": v(228.34, 431.1) * mm});
            skLineSegment(sketch, "E2.11.19.2", {"start": v(178.34, 481.1) * mm, "end": v(178.34, 431.1) * mm});
            skLineSegment(sketch, "E2.11.19.3", {"start": v(178.34, 481.1) * mm, "end": v(228.34, 481.1) * mm});
            skLineSegment(sketch, "E2.11.20.0", {"start": v(228.34, 421.1) * mm, "end": v(228.34, 371.1) * mm});
            skLineSegment(sketch, "E2.11.20.1", {"start": v(178.34, 371.1) * mm, "end": v(228.34, 371.1) * mm});
            skLineSegment(sketch, "E2.11.20.2", {"start": v(178.34, 421.1) * mm, "end": v(178.34, 371.1) * mm});
            skLineSegment(sketch, "E2.11.20.3", {"start": v(178.34, 421.1) * mm, "end": v(228.34, 421.1) * mm});
            skLineSegment(sketch, "E2.11.21.0", {"start": v(228.34, 361.1) * mm, "end": v(228.34, 311.1) * mm});
            skLineSegment(sketch, "E2.11.21.1", {"start": v(178.34, 311.1) * mm, "end": v(228.34, 311.1) * mm});
            skLineSegment(sketch, "E2.11.21.2", {"start": v(178.34, 361.1) * mm, "end": v(178.34, 311.1) * mm});
            skLineSegment(sketch, "E2.11.21.3", {"start": v(178.34, 361.1) * mm, "end": v(228.34, 361.1) * mm});
            skLineSegment(sketch, "E2.11.22.0", {"start": v(228.34, 301.1) * mm, "end": v(228.34, 251.1) * mm});
            skLineSegment(sketch, "E2.11.22.1", {"start": v(178.34, 251.1) * mm, "end": v(228.34, 251.1) * mm});
            skLineSegment(sketch, "E2.11.22.2", {"start": v(178.34, 301.1) * mm, "end": v(178.34, 251.1) * mm});
            skLineSegment(sketch, "E2.11.22.3", {"start": v(178.34, 301.1) * mm, "end": v(228.34, 301.1) * mm});
            skLineSegment(sketch, "E2.11.23.0", {"start": v(228.34, 241.1) * mm, "end": v(228.34, 191.1) * mm});
            skLineSegment(sketch, "E2.11.23.1", {"start": v(178.34, 191.1) * mm, "end": v(228.34, 191.1) * mm});
            skLineSegment(sketch, "E2.11.23.2", {"start": v(178.34, 241.1) * mm, "end": v(178.34, 191.1) * mm});
            skLineSegment(sketch, "E2.11.23.3", {"start": v(178.34, 241.1) * mm, "end": v(228.34, 241.1) * mm});
            skLineSegment(sketch, "E2.11.24.0", {"start": v(228.34, 181.1) * mm, "end": v(228.34, 131.1) * mm});
            skLineSegment(sketch, "E2.11.24.1", {"start": v(178.34, 131.1) * mm, "end": v(228.34, 131.1) * mm});
            skLineSegment(sketch, "E2.11.24.2", {"start": v(178.34, 181.1) * mm, "end": v(178.34, 131.1) * mm});
            skLineSegment(sketch, "E2.11.24.3", {"start": v(178.34, 181.1) * mm, "end": v(228.34, 181.1) * mm});
            skLineSegment(sketch, "E2.11.25.0", {"start": v(228.34, 121.1) * mm, "end": v(228.34, 71.1) * mm});
            skLineSegment(sketch, "E2.11.25.1", {"start": v(178.34, 71.1) * mm, "end": v(228.34, 71.1) * mm});
            skLineSegment(sketch, "E2.11.25.2", {"start": v(178.34, 121.1) * mm, "end": v(178.34, 71.1) * mm});
            skLineSegment(sketch, "E2.11.25.3", {"start": v(178.34, 121.1) * mm, "end": v(228.34, 121.1) * mm});
            skLineSegment(sketch, "E2.11.26.0", {"start": v(228.34, 61.1) * mm, "end": v(228.34, 11.1) * mm});
            skLineSegment(sketch, "E2.11.26.1", {"start": v(178.34, 11.1) * mm, "end": v(228.34, 11.1) * mm});
            skLineSegment(sketch, "E2.11.26.2", {"start": v(178.34, 61.1) * mm, "end": v(178.34, 11.1) * mm});
            skLineSegment(sketch, "E2.11.26.3", {"start": v(178.34, 61.1) * mm, "end": v(228.34, 61.1) * mm});
            skLineSegment(sketch, "E2.11.27.0", {"start": v(228.34, 1.1) * mm, "end": v(228.34, -48.9) * mm});
            skLineSegment(sketch, "E2.11.27.1", {"start": v(178.34, -48.9) * mm, "end": v(228.34, -48.9) * mm});
            skLineSegment(sketch, "E2.11.27.2", {"start": v(178.34, 1.1) * mm, "end": v(178.34, -48.9) * mm});
            skLineSegment(sketch, "E2.11.27.3", {"start": v(178.34, 1.1) * mm, "end": v(228.34, 1.1) * mm});
            skLineSegment(sketch, "E2.11.28.0", {"start": v(228.34, -58.9) * mm, "end": v(228.34, -108.9) * mm});
            skLineSegment(sketch, "E2.11.28.1", {"start": v(178.34, -108.9) * mm, "end": v(228.34, -108.9) * mm});
            skLineSegment(sketch, "E2.11.28.2", {"start": v(178.34, -58.9) * mm, "end": v(178.34, -108.9) * mm});
            skLineSegment(sketch, "E2.11.28.3", {"start": v(178.34, -58.9) * mm, "end": v(228.34, -58.9) * mm});
            skLineSegment(sketch, "E2.11.29.0", {"start": v(228.34, -118.9) * mm, "end": v(228.34, -168.9) * mm});
            skLineSegment(sketch, "E2.11.29.1", {"start": v(178.34, -168.9) * mm, "end": v(228.34, -168.9) * mm});
            skLineSegment(sketch, "E2.11.29.2", {"start": v(178.34, -118.9) * mm, "end": v(178.34, -168.9) * mm});
            skLineSegment(sketch, "E2.11.29.3", {"start": v(178.34, -118.9) * mm, "end": v(228.34, -118.9) * mm});
            skLineSegment(sketch, "E2.11.30.0", {"start": v(228.34, -178.9) * mm, "end": v(228.34, -228.9) * mm});
            skLineSegment(sketch, "E2.11.30.1", {"start": v(178.34, -228.9) * mm, "end": v(228.34, -228.9) * mm});
            skLineSegment(sketch, "E2.11.30.2", {"start": v(178.34, -178.9) * mm, "end": v(178.34, -228.9) * mm});
            skLineSegment(sketch, "E2.11.30.3", {"start": v(178.34, -178.9) * mm, "end": v(228.34, -178.9) * mm});
            skLineSegment(sketch, "E2.11.31.0", {"start": v(228.34, -238.9) * mm, "end": v(228.34, -288.9) * mm});
            skLineSegment(sketch, "E2.11.31.1", {"start": v(178.34, -288.9) * mm, "end": v(228.34, -288.9) * mm});
            skLineSegment(sketch, "E2.11.31.2", {"start": v(178.34, -238.9) * mm, "end": v(178.34, -288.9) * mm});
            skLineSegment(sketch, "E2.11.31.3", {"start": v(178.34, -238.9) * mm, "end": v(228.34, -238.9) * mm});
            skLineSegment(sketch, "E2.11.32.0", {"start": v(228.34, -298.9) * mm, "end": v(228.34, -348.9) * mm});
            skLineSegment(sketch, "E2.11.32.1", {"start": v(178.34, -348.9) * mm, "end": v(228.34, -348.9) * mm});
            skLineSegment(sketch, "E2.11.32.2", {"start": v(178.34, -298.9) * mm, "end": v(178.34, -348.9) * mm});
            skLineSegment(sketch, "E2.11.32.3", {"start": v(178.34, -298.9) * mm, "end": v(228.34, -298.9) * mm});
            skLineSegment(sketch, "E2.12.0.0", {"start": v(288.34, 1621.1) * mm, "end": v(288.34, 1571.1) * mm});
            skLineSegment(sketch, "E2.12.0.1", {"start": v(238.34, 1571.1) * mm, "end": v(288.34, 1571.1) * mm});
            skLineSegment(sketch, "E2.12.0.2", {"start": v(238.34, 1621.1) * mm, "end": v(238.34, 1571.1) * mm});
            skLineSegment(sketch, "E2.12.0.3", {"start": v(238.34, 1621.1) * mm, "end": v(288.34, 1621.1) * mm});
            skLineSegment(sketch, "E2.12.1.0", {"start": v(288.34, 1561.1) * mm, "end": v(288.34, 1511.1) * mm});
            skLineSegment(sketch, "E2.12.1.1", {"start": v(238.34, 1511.1) * mm, "end": v(288.34, 1511.1) * mm});
            skLineSegment(sketch, "E2.12.1.2", {"start": v(238.34, 1561.1) * mm, "end": v(238.34, 1511.1) * mm});
            skLineSegment(sketch, "E2.12.1.3", {"start": v(238.34, 1561.1) * mm, "end": v(288.34, 1561.1) * mm});
            skLineSegment(sketch, "E2.12.2.0", {"start": v(288.34, 1501.1) * mm, "end": v(288.34, 1451.1) * mm});
            skLineSegment(sketch, "E2.12.2.1", {"start": v(238.34, 1451.1) * mm, "end": v(288.34, 1451.1) * mm});
            skLineSegment(sketch, "E2.12.2.2", {"start": v(238.34, 1501.1) * mm, "end": v(238.34, 1451.1) * mm});
            skLineSegment(sketch, "E2.12.2.3", {"start": v(238.34, 1501.1) * mm, "end": v(288.34, 1501.1) * mm});
            skLineSegment(sketch, "E2.12.3.0", {"start": v(288.34, 1441.1) * mm, "end": v(288.34, 1391.1) * mm});
            skLineSegment(sketch, "E2.12.3.1", {"start": v(238.34, 1391.1) * mm, "end": v(288.34, 1391.1) * mm});
            skLineSegment(sketch, "E2.12.3.2", {"start": v(238.34, 1441.1) * mm, "end": v(238.34, 1391.1) * mm});
            skLineSegment(sketch, "E2.12.3.3", {"start": v(238.34, 1441.1) * mm, "end": v(288.34, 1441.1) * mm});
            skLineSegment(sketch, "E2.12.4.0", {"start": v(288.34, 1381.1) * mm, "end": v(288.34, 1331.1) * mm});
            skLineSegment(sketch, "E2.12.4.1", {"start": v(238.34, 1331.1) * mm, "end": v(288.34, 1331.1) * mm});
            skLineSegment(sketch, "E2.12.4.2", {"start": v(238.34, 1381.1) * mm, "end": v(238.34, 1331.1) * mm});
            skLineSegment(sketch, "E2.12.4.3", {"start": v(238.34, 1381.1) * mm, "end": v(288.34, 1381.1) * mm});
            skLineSegment(sketch, "E2.12.5.0", {"start": v(288.34, 1321.1) * mm, "end": v(288.34, 1271.1) * mm});
            skLineSegment(sketch, "E2.12.5.1", {"start": v(238.34, 1271.1) * mm, "end": v(288.34, 1271.1) * mm});
            skLineSegment(sketch, "E2.12.5.2", {"start": v(238.34, 1321.1) * mm, "end": v(238.34, 1271.1) * mm});
            skLineSegment(sketch, "E2.12.5.3", {"start": v(238.34, 1321.1) * mm, "end": v(288.34, 1321.1) * mm});
            skLineSegment(sketch, "E2.12.6.0", {"start": v(288.34, 1261.1) * mm, "end": v(288.34, 1211.1) * mm});
            skLineSegment(sketch, "E2.12.6.1", {"start": v(238.34, 1211.1) * mm, "end": v(288.34, 1211.1) * mm});
            skLineSegment(sketch, "E2.12.6.2", {"start": v(238.34, 1261.1) * mm, "end": v(238.34, 1211.1) * mm});
            skLineSegment(sketch, "E2.12.6.3", {"start": v(238.34, 1261.1) * mm, "end": v(288.34, 1261.1) * mm});
            skLineSegment(sketch, "E2.12.7.0", {"start": v(288.34, 1201.1) * mm, "end": v(288.34, 1151.1) * mm});
            skLineSegment(sketch, "E2.12.7.1", {"start": v(238.34, 1151.1) * mm, "end": v(288.34, 1151.1) * mm});
            skLineSegment(sketch, "E2.12.7.2", {"start": v(238.34, 1201.1) * mm, "end": v(238.34, 1151.1) * mm});
            skLineSegment(sketch, "E2.12.7.3", {"start": v(238.34, 1201.1) * mm, "end": v(288.34, 1201.1) * mm});
            skLineSegment(sketch, "E2.12.8.0", {"start": v(288.34, 1141.1) * mm, "end": v(288.34, 1091.1) * mm});
            skLineSegment(sketch, "E2.12.8.1", {"start": v(238.34, 1091.1) * mm, "end": v(288.34, 1091.1) * mm});
            skLineSegment(sketch, "E2.12.8.2", {"start": v(238.34, 1141.1) * mm, "end": v(238.34, 1091.1) * mm});
            skLineSegment(sketch, "E2.12.8.3", {"start": v(238.34, 1141.1) * mm, "end": v(288.34, 1141.1) * mm});
            skLineSegment(sketch, "E2.12.9.0", {"start": v(288.34, 1081.1) * mm, "end": v(288.34, 1031.1) * mm});
            skLineSegment(sketch, "E2.12.9.1", {"start": v(238.34, 1031.1) * mm, "end": v(288.34, 1031.1) * mm});
            skLineSegment(sketch, "E2.12.9.2", {"start": v(238.34, 1081.1) * mm, "end": v(238.34, 1031.1) * mm});
            skLineSegment(sketch, "E2.12.9.3", {"start": v(238.34, 1081.1) * mm, "end": v(288.34, 1081.1) * mm});
            skLineSegment(sketch, "E2.12.10.0", {"start": v(288.34, 1021.1) * mm, "end": v(288.34, 971.1) * mm});
            skLineSegment(sketch, "E2.12.10.1", {"start": v(238.34, 971.1) * mm, "end": v(288.34, 971.1) * mm});
            skLineSegment(sketch, "E2.12.10.2", {"start": v(238.34, 1021.1) * mm, "end": v(238.34, 971.1) * mm});
            skLineSegment(sketch, "E2.12.10.3", {"start": v(238.34, 1021.1) * mm, "end": v(288.34, 1021.1) * mm});
            skLineSegment(sketch, "E2.12.11.0", {"start": v(288.34, 961.1) * mm, "end": v(288.34, 911.1) * mm});
            skLineSegment(sketch, "E2.12.11.1", {"start": v(238.34, 911.1) * mm, "end": v(288.34, 911.1) * mm});
            skLineSegment(sketch, "E2.12.11.2", {"start": v(238.34, 961.1) * mm, "end": v(238.34, 911.1) * mm});
            skLineSegment(sketch, "E2.12.11.3", {"start": v(238.34, 961.1) * mm, "end": v(288.34, 961.1) * mm});
            skLineSegment(sketch, "E2.12.12.0", {"start": v(288.34, 901.1) * mm, "end": v(288.34, 851.1) * mm});
            skLineSegment(sketch, "E2.12.12.1", {"start": v(238.34, 851.1) * mm, "end": v(288.34, 851.1) * mm});
            skLineSegment(sketch, "E2.12.12.2", {"start": v(238.34, 901.1) * mm, "end": v(238.34, 851.1) * mm});
            skLineSegment(sketch, "E2.12.12.3", {"start": v(238.34, 901.1) * mm, "end": v(288.34, 901.1) * mm});
            skLineSegment(sketch, "E2.12.13.0", {"start": v(288.34, 841.1) * mm, "end": v(288.34, 791.1) * mm});
            skLineSegment(sketch, "E2.12.13.1", {"start": v(238.34, 791.1) * mm, "end": v(288.34, 791.1) * mm});
            skLineSegment(sketch, "E2.12.13.2", {"start": v(238.34, 841.1) * mm, "end": v(238.34, 791.1) * mm});
            skLineSegment(sketch, "E2.12.13.3", {"start": v(238.34, 841.1) * mm, "end": v(288.34, 841.1) * mm});
            skLineSegment(sketch, "E2.12.14.0", {"start": v(288.34, 781.1) * mm, "end": v(288.34, 731.1) * mm});
            skLineSegment(sketch, "E2.12.14.1", {"start": v(238.34, 731.1) * mm, "end": v(288.34, 731.1) * mm});
            skLineSegment(sketch, "E2.12.14.2", {"start": v(238.34, 781.1) * mm, "end": v(238.34, 731.1) * mm});
            skLineSegment(sketch, "E2.12.14.3", {"start": v(238.34, 781.1) * mm, "end": v(288.34, 781.1) * mm});
            skLineSegment(sketch, "E2.12.15.0", {"start": v(288.34, 721.1) * mm, "end": v(288.34, 671.1) * mm});
            skLineSegment(sketch, "E2.12.15.1", {"start": v(238.34, 671.1) * mm, "end": v(288.34, 671.1) * mm});
            skLineSegment(sketch, "E2.12.15.2", {"start": v(238.34, 721.1) * mm, "end": v(238.34, 671.1) * mm});
            skLineSegment(sketch, "E2.12.15.3", {"start": v(238.34, 721.1) * mm, "end": v(288.34, 721.1) * mm});
            skLineSegment(sketch, "E2.12.16.0", {"start": v(288.34, 661.1) * mm, "end": v(288.34, 611.1) * mm});
            skLineSegment(sketch, "E2.12.16.1", {"start": v(238.34, 611.1) * mm, "end": v(288.34, 611.1) * mm});
            skLineSegment(sketch, "E2.12.16.2", {"start": v(238.34, 661.1) * mm, "end": v(238.34, 611.1) * mm});
            skLineSegment(sketch, "E2.12.16.3", {"start": v(238.34, 661.1) * mm, "end": v(288.34, 661.1) * mm});
            skLineSegment(sketch, "E2.12.17.0", {"start": v(288.34, 601.1) * mm, "end": v(288.34, 551.1) * mm});
            skLineSegment(sketch, "E2.12.17.1", {"start": v(238.34, 551.1) * mm, "end": v(288.34, 551.1) * mm});
            skLineSegment(sketch, "E2.12.17.2", {"start": v(238.34, 601.1) * mm, "end": v(238.34, 551.1) * mm});
            skLineSegment(sketch, "E2.12.17.3", {"start": v(238.34, 601.1) * mm, "end": v(288.34, 601.1) * mm});
            skLineSegment(sketch, "E2.12.18.0", {"start": v(288.34, 541.1) * mm, "end": v(288.34, 491.1) * mm});
            skLineSegment(sketch, "E2.12.18.1", {"start": v(238.34, 491.1) * mm, "end": v(288.34, 491.1) * mm});
            skLineSegment(sketch, "E2.12.18.2", {"start": v(238.34, 541.1) * mm, "end": v(238.34, 491.1) * mm});
            skLineSegment(sketch, "E2.12.18.3", {"start": v(238.34, 541.1) * mm, "end": v(288.34, 541.1) * mm});
            skLineSegment(sketch, "E2.12.19.0", {"start": v(288.34, 481.1) * mm, "end": v(288.34, 431.1) * mm});
            skLineSegment(sketch, "E2.12.19.1", {"start": v(238.34, 431.1) * mm, "end": v(288.34, 431.1) * mm});
            skLineSegment(sketch, "E2.12.19.2", {"start": v(238.34, 481.1) * mm, "end": v(238.34, 431.1) * mm});
            skLineSegment(sketch, "E2.12.19.3", {"start": v(238.34, 481.1) * mm, "end": v(288.34, 481.1) * mm});
            skLineSegment(sketch, "E2.12.20.0", {"start": v(288.34, 421.1) * mm, "end": v(288.34, 371.1) * mm});
            skLineSegment(sketch, "E2.12.20.1", {"start": v(238.34, 371.1) * mm, "end": v(288.34, 371.1) * mm});
            skLineSegment(sketch, "E2.12.20.2", {"start": v(238.34, 421.1) * mm, "end": v(238.34, 371.1) * mm});
            skLineSegment(sketch, "E2.12.20.3", {"start": v(238.34, 421.1) * mm, "end": v(288.34, 421.1) * mm});
            skLineSegment(sketch, "E2.12.21.0", {"start": v(288.34, 361.1) * mm, "end": v(288.34, 311.1) * mm});
            skLineSegment(sketch, "E2.12.21.1", {"start": v(238.34, 311.1) * mm, "end": v(288.34, 311.1) * mm});
            skLineSegment(sketch, "E2.12.21.2", {"start": v(238.34, 361.1) * mm, "end": v(238.34, 311.1) * mm});
            skLineSegment(sketch, "E2.12.21.3", {"start": v(238.34, 361.1) * mm, "end": v(288.34, 361.1) * mm});
            skLineSegment(sketch, "E2.12.22.0", {"start": v(288.34, 301.1) * mm, "end": v(288.34, 251.1) * mm});
            skLineSegment(sketch, "E2.12.22.1", {"start": v(238.34, 251.1) * mm, "end": v(288.34, 251.1) * mm});
            skLineSegment(sketch, "E2.12.22.2", {"start": v(238.34, 301.1) * mm, "end": v(238.34, 251.1) * mm});
            skLineSegment(sketch, "E2.12.22.3", {"start": v(238.34, 301.1) * mm, "end": v(288.34, 301.1) * mm});
            skLineSegment(sketch, "E2.12.23.0", {"start": v(288.34, 241.1) * mm, "end": v(288.34, 191.1) * mm});
            skLineSegment(sketch, "E2.12.23.1", {"start": v(238.34, 191.1) * mm, "end": v(288.34, 191.1) * mm});
            skLineSegment(sketch, "E2.12.23.2", {"start": v(238.34, 241.1) * mm, "end": v(238.34, 191.1) * mm});
            skLineSegment(sketch, "E2.12.23.3", {"start": v(238.34, 241.1) * mm, "end": v(288.34, 241.1) * mm});
            skLineSegment(sketch, "E2.12.24.0", {"start": v(288.34, 181.1) * mm, "end": v(288.34, 131.1) * mm});
            skLineSegment(sketch, "E2.12.24.1", {"start": v(238.34, 131.1) * mm, "end": v(288.34, 131.1) * mm});
            skLineSegment(sketch, "E2.12.24.2", {"start": v(238.34, 181.1) * mm, "end": v(238.34, 131.1) * mm});
            skLineSegment(sketch, "E2.12.24.3", {"start": v(238.34, 181.1) * mm, "end": v(288.34, 181.1) * mm});
            skLineSegment(sketch, "E2.12.25.0", {"start": v(288.34, 121.1) * mm, "end": v(288.34, 71.1) * mm});
            skLineSegment(sketch, "E2.12.25.1", {"start": v(238.34, 71.1) * mm, "end": v(288.34, 71.1) * mm});
            skLineSegment(sketch, "E2.12.25.2", {"start": v(238.34, 121.1) * mm, "end": v(238.34, 71.1) * mm});
            skLineSegment(sketch, "E2.12.25.3", {"start": v(238.34, 121.1) * mm, "end": v(288.34, 121.1) * mm});
            skLineSegment(sketch, "E2.12.26.0", {"start": v(288.34, 61.1) * mm, "end": v(288.34, 11.1) * mm});
            skLineSegment(sketch, "E2.12.26.1", {"start": v(238.34, 11.1) * mm, "end": v(288.34, 11.1) * mm});
            skLineSegment(sketch, "E2.12.26.2", {"start": v(238.34, 61.1) * mm, "end": v(238.34, 11.1) * mm});
            skLineSegment(sketch, "E2.12.26.3", {"start": v(238.34, 61.1) * mm, "end": v(288.34, 61.1) * mm});
            skLineSegment(sketch, "E2.12.27.0", {"start": v(288.34, 1.1) * mm, "end": v(288.34, -48.9) * mm});
            skLineSegment(sketch, "E2.12.27.1", {"start": v(238.34, -48.9) * mm, "end": v(288.34, -48.9) * mm});
            skLineSegment(sketch, "E2.12.27.2", {"start": v(238.34, 1.1) * mm, "end": v(238.34, -48.9) * mm});
            skLineSegment(sketch, "E2.12.27.3", {"start": v(238.34, 1.1) * mm, "end": v(288.34, 1.1) * mm});
            skLineSegment(sketch, "E2.12.28.0", {"start": v(288.34, -58.9) * mm, "end": v(288.34, -108.9) * mm});
            skLineSegment(sketch, "E2.12.28.1", {"start": v(238.34, -108.9) * mm, "end": v(288.34, -108.9) * mm});
            skLineSegment(sketch, "E2.12.28.2", {"start": v(238.34, -58.9) * mm, "end": v(238.34, -108.9) * mm});
            skLineSegment(sketch, "E2.12.28.3", {"start": v(238.34, -58.9) * mm, "end": v(288.34, -58.9) * mm});
            skLineSegment(sketch, "E2.12.29.0", {"start": v(288.34, -118.9) * mm, "end": v(288.34, -168.9) * mm});
            skLineSegment(sketch, "E2.12.29.1", {"start": v(238.34, -168.9) * mm, "end": v(288.34, -168.9) * mm});
            skLineSegment(sketch, "E2.12.29.2", {"start": v(238.34, -118.9) * mm, "end": v(238.34, -168.9) * mm});
            skLineSegment(sketch, "E2.12.29.3", {"start": v(238.34, -118.9) * mm, "end": v(288.34, -118.9) * mm});
            skLineSegment(sketch, "E2.12.30.0", {"start": v(288.34, -178.9) * mm, "end": v(288.34, -228.9) * mm});
            skLineSegment(sketch, "E2.12.30.1", {"start": v(238.34, -228.9) * mm, "end": v(288.34, -228.9) * mm});
            skLineSegment(sketch, "E2.12.30.2", {"start": v(238.34, -178.9) * mm, "end": v(238.34, -228.9) * mm});
            skLineSegment(sketch, "E2.12.30.3", {"start": v(238.34, -178.9) * mm, "end": v(288.34, -178.9) * mm});
            skLineSegment(sketch, "E2.12.31.0", {"start": v(288.34, -238.9) * mm, "end": v(288.34, -288.9) * mm});
            skLineSegment(sketch, "E2.12.31.1", {"start": v(238.34, -288.9) * mm, "end": v(288.34, -288.9) * mm});
            skLineSegment(sketch, "E2.12.31.2", {"start": v(238.34, -238.9) * mm, "end": v(238.34, -288.9) * mm});
            skLineSegment(sketch, "E2.12.31.3", {"start": v(238.34, -238.9) * mm, "end": v(288.34, -238.9) * mm});
            skLineSegment(sketch, "E2.12.32.0", {"start": v(288.34, -298.9) * mm, "end": v(288.34, -348.9) * mm});
            skLineSegment(sketch, "E2.12.32.1", {"start": v(238.34, -348.9) * mm, "end": v(288.34, -348.9) * mm});
            skLineSegment(sketch, "E2.12.32.2", {"start": v(238.34, -298.9) * mm, "end": v(238.34, -348.9) * mm});
            skLineSegment(sketch, "E2.12.32.3", {"start": v(238.34, -298.9) * mm, "end": v(288.34, -298.9) * mm});
            skLineSegment(sketch, "E2.13.0.0", {"start": v(348.34, 1621.1) * mm, "end": v(348.34, 1571.1) * mm});
            skLineSegment(sketch, "E2.13.0.1", {"start": v(298.34, 1571.1) * mm, "end": v(348.34, 1571.1) * mm});
            skLineSegment(sketch, "E2.13.0.2", {"start": v(298.34, 1621.1) * mm, "end": v(298.34, 1571.1) * mm});
            skLineSegment(sketch, "E2.13.0.3", {"start": v(298.34, 1621.1) * mm, "end": v(348.34, 1621.1) * mm});
            skLineSegment(sketch, "E2.13.1.0", {"start": v(348.34, 1561.1) * mm, "end": v(348.34, 1511.1) * mm});
            skLineSegment(sketch, "E2.13.1.1", {"start": v(298.34, 1511.1) * mm, "end": v(348.34, 1511.1) * mm});
            skLineSegment(sketch, "E2.13.1.2", {"start": v(298.34, 1561.1) * mm, "end": v(298.34, 1511.1) * mm});
            skLineSegment(sketch, "E2.13.1.3", {"start": v(298.34, 1561.1) * mm, "end": v(348.34, 1561.1) * mm});
            skLineSegment(sketch, "E2.13.2.0", {"start": v(348.34, 1501.1) * mm, "end": v(348.34, 1451.1) * mm});
            skLineSegment(sketch, "E2.13.2.1", {"start": v(298.34, 1451.1) * mm, "end": v(348.34, 1451.1) * mm});
            skLineSegment(sketch, "E2.13.2.2", {"start": v(298.34, 1501.1) * mm, "end": v(298.34, 1451.1) * mm});
            skLineSegment(sketch, "E2.13.2.3", {"start": v(298.34, 1501.1) * mm, "end": v(348.34, 1501.1) * mm});
            skLineSegment(sketch, "E2.13.3.0", {"start": v(348.34, 1441.1) * mm, "end": v(348.34, 1391.1) * mm});
            skLineSegment(sketch, "E2.13.3.1", {"start": v(298.34, 1391.1) * mm, "end": v(348.34, 1391.1) * mm});
            skLineSegment(sketch, "E2.13.3.2", {"start": v(298.34, 1441.1) * mm, "end": v(298.34, 1391.1) * mm});
            skLineSegment(sketch, "E2.13.3.3", {"start": v(298.34, 1441.1) * mm, "end": v(348.34, 1441.1) * mm});
            skLineSegment(sketch, "E2.13.4.0", {"start": v(348.34, 1381.1) * mm, "end": v(348.34, 1331.1) * mm});
            skLineSegment(sketch, "E2.13.4.1", {"start": v(298.34, 1331.1) * mm, "end": v(348.34, 1331.1) * mm});
            skLineSegment(sketch, "E2.13.4.2", {"start": v(298.34, 1381.1) * mm, "end": v(298.34, 1331.1) * mm});
            skLineSegment(sketch, "E2.13.4.3", {"start": v(298.34, 1381.1) * mm, "end": v(348.34, 1381.1) * mm});
            skLineSegment(sketch, "E2.13.5.0", {"start": v(348.34, 1321.1) * mm, "end": v(348.34, 1271.1) * mm});
            skLineSegment(sketch, "E2.13.5.1", {"start": v(298.34, 1271.1) * mm, "end": v(348.34, 1271.1) * mm});
            skLineSegment(sketch, "E2.13.5.2", {"start": v(298.34, 1321.1) * mm, "end": v(298.34, 1271.1) * mm});
            skLineSegment(sketch, "E2.13.5.3", {"start": v(298.34, 1321.1) * mm, "end": v(348.34, 1321.1) * mm});
            skLineSegment(sketch, "E2.13.6.0", {"start": v(348.34, 1261.1) * mm, "end": v(348.34, 1211.1) * mm});
            skLineSegment(sketch, "E2.13.6.1", {"start": v(298.34, 1211.1) * mm, "end": v(348.34, 1211.1) * mm});
            skLineSegment(sketch, "E2.13.6.2", {"start": v(298.34, 1261.1) * mm, "end": v(298.34, 1211.1) * mm});
            skLineSegment(sketch, "E2.13.6.3", {"start": v(298.34, 1261.1) * mm, "end": v(348.34, 1261.1) * mm});
            skLineSegment(sketch, "E2.13.7.0", {"start": v(348.34, 1201.1) * mm, "end": v(348.34, 1151.1) * mm});
            skLineSegment(sketch, "E2.13.7.1", {"start": v(298.34, 1151.1) * mm, "end": v(348.34, 1151.1) * mm});
            skLineSegment(sketch, "E2.13.7.2", {"start": v(298.34, 1201.1) * mm, "end": v(298.34, 1151.1) * mm});
            skLineSegment(sketch, "E2.13.7.3", {"start": v(298.34, 1201.1) * mm, "end": v(348.34, 1201.1) * mm});
            skLineSegment(sketch, "E2.13.8.0", {"start": v(348.34, 1141.1) * mm, "end": v(348.34, 1091.1) * mm});
            skLineSegment(sketch, "E2.13.8.1", {"start": v(298.34, 1091.1) * mm, "end": v(348.34, 1091.1) * mm});
            skLineSegment(sketch, "E2.13.8.2", {"start": v(298.34, 1141.1) * mm, "end": v(298.34, 1091.1) * mm});
            skLineSegment(sketch, "E2.13.8.3", {"start": v(298.34, 1141.1) * mm, "end": v(348.34, 1141.1) * mm});
            skLineSegment(sketch, "E2.13.9.0", {"start": v(348.34, 1081.1) * mm, "end": v(348.34, 1031.1) * mm});
            skLineSegment(sketch, "E2.13.9.1", {"start": v(298.34, 1031.1) * mm, "end": v(348.34, 1031.1) * mm});
            skLineSegment(sketch, "E2.13.9.2", {"start": v(298.34, 1081.1) * mm, "end": v(298.34, 1031.1) * mm});
            skLineSegment(sketch, "E2.13.9.3", {"start": v(298.34, 1081.1) * mm, "end": v(348.34, 1081.1) * mm});
            skLineSegment(sketch, "E2.13.10.0", {"start": v(348.34, 1021.1) * mm, "end": v(348.34, 971.1) * mm});
            skLineSegment(sketch, "E2.13.10.1", {"start": v(298.34, 971.1) * mm, "end": v(348.34, 971.1) * mm});
            skLineSegment(sketch, "E2.13.10.2", {"start": v(298.34, 1021.1) * mm, "end": v(298.34, 971.1) * mm});
            skLineSegment(sketch, "E2.13.10.3", {"start": v(298.34, 1021.1) * mm, "end": v(348.34, 1021.1) * mm});
            skLineSegment(sketch, "E2.13.11.0", {"start": v(348.34, 961.1) * mm, "end": v(348.34, 911.1) * mm});
            skLineSegment(sketch, "E2.13.11.1", {"start": v(298.34, 911.1) * mm, "end": v(348.34, 911.1) * mm});
            skLineSegment(sketch, "E2.13.11.2", {"start": v(298.34, 961.1) * mm, "end": v(298.34, 911.1) * mm});
            skLineSegment(sketch, "E2.13.11.3", {"start": v(298.34, 961.1) * mm, "end": v(348.34, 961.1) * mm});
            skLineSegment(sketch, "E2.13.12.0", {"start": v(348.34, 901.1) * mm, "end": v(348.34, 851.1) * mm});
            skLineSegment(sketch, "E2.13.12.1", {"start": v(298.34, 851.1) * mm, "end": v(348.34, 851.1) * mm});
            skLineSegment(sketch, "E2.13.12.2", {"start": v(298.34, 901.1) * mm, "end": v(298.34, 851.1) * mm});
            skLineSegment(sketch, "E2.13.12.3", {"start": v(298.34, 901.1) * mm, "end": v(348.34, 901.1) * mm});
            skLineSegment(sketch, "E2.13.13.0", {"start": v(348.34, 841.1) * mm, "end": v(348.34, 791.1) * mm});
            skLineSegment(sketch, "E2.13.13.1", {"start": v(298.34, 791.1) * mm, "end": v(348.34, 791.1) * mm});
            skLineSegment(sketch, "E2.13.13.2", {"start": v(298.34, 841.1) * mm, "end": v(298.34, 791.1) * mm});
            skLineSegment(sketch, "E2.13.13.3", {"start": v(298.34, 841.1) * mm, "end": v(348.34, 841.1) * mm});
            skLineSegment(sketch, "E2.13.14.0", {"start": v(348.34, 781.1) * mm, "end": v(348.34, 731.1) * mm});
            skLineSegment(sketch, "E2.13.14.1", {"start": v(298.34, 731.1) * mm, "end": v(348.34, 731.1) * mm});
            skLineSegment(sketch, "E2.13.14.2", {"start": v(298.34, 781.1) * mm, "end": v(298.34, 731.1) * mm});
            skLineSegment(sketch, "E2.13.14.3", {"start": v(298.34, 781.1) * mm, "end": v(348.34, 781.1) * mm});
            skLineSegment(sketch, "E2.13.15.0", {"start": v(348.34, 721.1) * mm, "end": v(348.34, 671.1) * mm});
            skLineSegment(sketch, "E2.13.15.1", {"start": v(298.34, 671.1) * mm, "end": v(348.34, 671.1) * mm});
            skLineSegment(sketch, "E2.13.15.2", {"start": v(298.34, 721.1) * mm, "end": v(298.34, 671.1) * mm});
            skLineSegment(sketch, "E2.13.15.3", {"start": v(298.34, 721.1) * mm, "end": v(348.34, 721.1) * mm});
            skLineSegment(sketch, "E2.13.16.0", {"start": v(348.34, 661.1) * mm, "end": v(348.34, 611.1) * mm});
            skLineSegment(sketch, "E2.13.16.1", {"start": v(298.34, 611.1) * mm, "end": v(348.34, 611.1) * mm});
            skLineSegment(sketch, "E2.13.16.2", {"start": v(298.34, 661.1) * mm, "end": v(298.34, 611.1) * mm});
            skLineSegment(sketch, "E2.13.16.3", {"start": v(298.34, 661.1) * mm, "end": v(348.34, 661.1) * mm});
            skLineSegment(sketch, "E2.13.17.0", {"start": v(348.34, 601.1) * mm, "end": v(348.34, 551.1) * mm});
            skLineSegment(sketch, "E2.13.17.1", {"start": v(298.34, 551.1) * mm, "end": v(348.34, 551.1) * mm});
            skLineSegment(sketch, "E2.13.17.2", {"start": v(298.34, 601.1) * mm, "end": v(298.34, 551.1) * mm});
            skLineSegment(sketch, "E2.13.17.3", {"start": v(298.34, 601.1) * mm, "end": v(348.34, 601.1) * mm});
            skLineSegment(sketch, "E2.13.18.0", {"start": v(348.34, 541.1) * mm, "end": v(348.34, 491.1) * mm});
            skLineSegment(sketch, "E2.13.18.1", {"start": v(298.34, 491.1) * mm, "end": v(348.34, 491.1) * mm});
            skLineSegment(sketch, "E2.13.18.2", {"start": v(298.34, 541.1) * mm, "end": v(298.34, 491.1) * mm});
            skLineSegment(sketch, "E2.13.18.3", {"start": v(298.34, 541.1) * mm, "end": v(348.34, 541.1) * mm});
            skLineSegment(sketch, "E2.13.19.0", {"start": v(348.34, 481.1) * mm, "end": v(348.34, 431.1) * mm});
            skLineSegment(sketch, "E2.13.19.1", {"start": v(298.34, 431.1) * mm, "end": v(348.34, 431.1) * mm});
            skLineSegment(sketch, "E2.13.19.2", {"start": v(298.34, 481.1) * mm, "end": v(298.34, 431.1) * mm});
            skLineSegment(sketch, "E2.13.19.3", {"start": v(298.34, 481.1) * mm, "end": v(348.34, 481.1) * mm});
            skLineSegment(sketch, "E2.13.20.0", {"start": v(348.34, 421.1) * mm, "end": v(348.34, 371.1) * mm});
            skLineSegment(sketch, "E2.13.20.1", {"start": v(298.34, 371.1) * mm, "end": v(348.34, 371.1) * mm});
            skLineSegment(sketch, "E2.13.20.2", {"start": v(298.34, 421.1) * mm, "end": v(298.34, 371.1) * mm});
            skLineSegment(sketch, "E2.13.20.3", {"start": v(298.34, 421.1) * mm, "end": v(348.34, 421.1) * mm});
            skLineSegment(sketch, "E2.13.21.0", {"start": v(348.34, 361.1) * mm, "end": v(348.34, 311.1) * mm});
            skLineSegment(sketch, "E2.13.21.1", {"start": v(298.34, 311.1) * mm, "end": v(348.34, 311.1) * mm});
            skLineSegment(sketch, "E2.13.21.2", {"start": v(298.34, 361.1) * mm, "end": v(298.34, 311.1) * mm});
            skLineSegment(sketch, "E2.13.21.3", {"start": v(298.34, 361.1) * mm, "end": v(348.34, 361.1) * mm});
            skLineSegment(sketch, "E2.13.22.0", {"start": v(348.34, 301.1) * mm, "end": v(348.34, 251.1) * mm});
            skLineSegment(sketch, "E2.13.22.1", {"start": v(298.34, 251.1) * mm, "end": v(348.34, 251.1) * mm});
            skLineSegment(sketch, "E2.13.22.2", {"start": v(298.34, 301.1) * mm, "end": v(298.34, 251.1) * mm});
            skLineSegment(sketch, "E2.13.22.3", {"start": v(298.34, 301.1) * mm, "end": v(348.34, 301.1) * mm});
            skLineSegment(sketch, "E2.13.23.0", {"start": v(348.34, 241.1) * mm, "end": v(348.34, 191.1) * mm});
            skLineSegment(sketch, "E2.13.23.1", {"start": v(298.34, 191.1) * mm, "end": v(348.34, 191.1) * mm});
            skLineSegment(sketch, "E2.13.23.2", {"start": v(298.34, 241.1) * mm, "end": v(298.34, 191.1) * mm});
            skLineSegment(sketch, "E2.13.23.3", {"start": v(298.34, 241.1) * mm, "end": v(348.34, 241.1) * mm});
            skLineSegment(sketch, "E2.13.24.0", {"start": v(348.34, 181.1) * mm, "end": v(348.34, 131.1) * mm});
            skLineSegment(sketch, "E2.13.24.1", {"start": v(298.34, 131.1) * mm, "end": v(348.34, 131.1) * mm});
            skLineSegment(sketch, "E2.13.24.2", {"start": v(298.34, 181.1) * mm, "end": v(298.34, 131.1) * mm});
            skLineSegment(sketch, "E2.13.24.3", {"start": v(298.34, 181.1) * mm, "end": v(348.34, 181.1) * mm});
            skLineSegment(sketch, "E2.13.25.0", {"start": v(348.34, 121.1) * mm, "end": v(348.34, 71.1) * mm});
            skLineSegment(sketch, "E2.13.25.1", {"start": v(298.34, 71.1) * mm, "end": v(348.34, 71.1) * mm});
            skLineSegment(sketch, "E2.13.25.2", {"start": v(298.34, 121.1) * mm, "end": v(298.34, 71.1) * mm});
            skLineSegment(sketch, "E2.13.25.3", {"start": v(298.34, 121.1) * mm, "end": v(348.34, 121.1) * mm});
            skLineSegment(sketch, "E2.13.26.0", {"start": v(348.34, 61.1) * mm, "end": v(348.34, 11.1) * mm});
            skLineSegment(sketch, "E2.13.26.1", {"start": v(298.34, 11.1) * mm, "end": v(348.34, 11.1) * mm});
            skLineSegment(sketch, "E2.13.26.2", {"start": v(298.34, 61.1) * mm, "end": v(298.34, 11.1) * mm});
            skLineSegment(sketch, "E2.13.26.3", {"start": v(298.34, 61.1) * mm, "end": v(348.34, 61.1) * mm});
            skLineSegment(sketch, "E2.13.27.0", {"start": v(348.34, 1.1) * mm, "end": v(348.34, -48.9) * mm});
            skLineSegment(sketch, "E2.13.27.1", {"start": v(298.34, -48.9) * mm, "end": v(348.34, -48.9) * mm});
            skLineSegment(sketch, "E2.13.27.2", {"start": v(298.34, 1.1) * mm, "end": v(298.34, -48.9) * mm});
            skLineSegment(sketch, "E2.13.27.3", {"start": v(298.34, 1.1) * mm, "end": v(348.34, 1.1) * mm});
            skLineSegment(sketch, "E2.13.28.0", {"start": v(348.34, -58.9) * mm, "end": v(348.34, -108.9) * mm});
            skLineSegment(sketch, "E2.13.28.1", {"start": v(298.34, -108.9) * mm, "end": v(348.34, -108.9) * mm});
            skLineSegment(sketch, "E2.13.28.2", {"start": v(298.34, -58.9) * mm, "end": v(298.34, -108.9) * mm});
            skLineSegment(sketch, "E2.13.28.3", {"start": v(298.34, -58.9) * mm, "end": v(348.34, -58.9) * mm});
            skLineSegment(sketch, "E2.13.29.0", {"start": v(348.34, -118.9) * mm, "end": v(348.34, -168.9) * mm});
            skLineSegment(sketch, "E2.13.29.1", {"start": v(298.34, -168.9) * mm, "end": v(348.34, -168.9) * mm});
            skLineSegment(sketch, "E2.13.29.2", {"start": v(298.34, -118.9) * mm, "end": v(298.34, -168.9) * mm});
            skLineSegment(sketch, "E2.13.29.3", {"start": v(298.34, -118.9) * mm, "end": v(348.34, -118.9) * mm});
            skLineSegment(sketch, "E2.13.30.0", {"start": v(348.34, -178.9) * mm, "end": v(348.34, -228.9) * mm});
            skLineSegment(sketch, "E2.13.30.1", {"start": v(298.34, -228.9) * mm, "end": v(348.34, -228.9) * mm});
            skLineSegment(sketch, "E2.13.30.2", {"start": v(298.34, -178.9) * mm, "end": v(298.34, -228.9) * mm});
            skLineSegment(sketch, "E2.13.30.3", {"start": v(298.34, -178.9) * mm, "end": v(348.34, -178.9) * mm});
            skLineSegment(sketch, "E2.13.31.0", {"start": v(348.34, -238.9) * mm, "end": v(348.34, -288.9) * mm});
            skLineSegment(sketch, "E2.13.31.1", {"start": v(298.34, -288.9) * mm, "end": v(348.34, -288.9) * mm});
            skLineSegment(sketch, "E2.13.31.2", {"start": v(298.34, -238.9) * mm, "end": v(298.34, -288.9) * mm});
            skLineSegment(sketch, "E2.13.31.3", {"start": v(298.34, -238.9) * mm, "end": v(348.34, -238.9) * mm});
            skLineSegment(sketch, "E2.13.32.0", {"start": v(348.34, -298.9) * mm, "end": v(348.34, -348.9) * mm});
            skLineSegment(sketch, "E2.13.32.1", {"start": v(298.34, -348.9) * mm, "end": v(348.34, -348.9) * mm});
            skLineSegment(sketch, "E2.13.32.2", {"start": v(298.34, -298.9) * mm, "end": v(298.34, -348.9) * mm});
            skLineSegment(sketch, "E2.13.32.3", {"start": v(298.34, -298.9) * mm, "end": v(348.34, -298.9) * mm});
            skLineSegment(sketch, "E2.14.0.0", {"start": v(408.34, 1621.1) * mm, "end": v(408.34, 1571.1) * mm});
            skLineSegment(sketch, "E2.14.0.1", {"start": v(358.34, 1571.1) * mm, "end": v(408.34, 1571.1) * mm});
            skLineSegment(sketch, "E2.14.0.2", {"start": v(358.34, 1621.1) * mm, "end": v(358.34, 1571.1) * mm});
            skLineSegment(sketch, "E2.14.0.3", {"start": v(358.34, 1621.1) * mm, "end": v(408.34, 1621.1) * mm});
            skLineSegment(sketch, "E2.14.1.0", {"start": v(408.34, 1561.1) * mm, "end": v(408.34, 1511.1) * mm});
            skLineSegment(sketch, "E2.14.1.1", {"start": v(358.34, 1511.1) * mm, "end": v(408.34, 1511.1) * mm});
            skLineSegment(sketch, "E2.14.1.2", {"start": v(358.34, 1561.1) * mm, "end": v(358.34, 1511.1) * mm});
            skLineSegment(sketch, "E2.14.1.3", {"start": v(358.34, 1561.1) * mm, "end": v(408.34, 1561.1) * mm});
            skLineSegment(sketch, "E2.14.2.0", {"start": v(408.34, 1501.1) * mm, "end": v(408.34, 1451.1) * mm});
            skLineSegment(sketch, "E2.14.2.1", {"start": v(358.34, 1451.1) * mm, "end": v(408.34, 1451.1) * mm});
            skLineSegment(sketch, "E2.14.2.2", {"start": v(358.34, 1501.1) * mm, "end": v(358.34, 1451.1) * mm});
            skLineSegment(sketch, "E2.14.2.3", {"start": v(358.34, 1501.1) * mm, "end": v(408.34, 1501.1) * mm});
            skLineSegment(sketch, "E2.14.3.0", {"start": v(408.34, 1441.1) * mm, "end": v(408.34, 1391.1) * mm});
            skLineSegment(sketch, "E2.14.3.1", {"start": v(358.34, 1391.1) * mm, "end": v(408.34, 1391.1) * mm});
            skLineSegment(sketch, "E2.14.3.2", {"start": v(358.34, 1441.1) * mm, "end": v(358.34, 1391.1) * mm});
            skLineSegment(sketch, "E2.14.3.3", {"start": v(358.34, 1441.1) * mm, "end": v(408.34, 1441.1) * mm});
            skLineSegment(sketch, "E2.14.4.0", {"start": v(408.34, 1381.1) * mm, "end": v(408.34, 1331.1) * mm});
            skLineSegment(sketch, "E2.14.4.1", {"start": v(358.34, 1331.1) * mm, "end": v(408.34, 1331.1) * mm});
            skLineSegment(sketch, "E2.14.4.2", {"start": v(358.34, 1381.1) * mm, "end": v(358.34, 1331.1) * mm});
            skLineSegment(sketch, "E2.14.4.3", {"start": v(358.34, 1381.1) * mm, "end": v(408.34, 1381.1) * mm});
            skLineSegment(sketch, "E2.14.5.0", {"start": v(408.34, 1321.1) * mm, "end": v(408.34, 1271.1) * mm});
            skLineSegment(sketch, "E2.14.5.1", {"start": v(358.34, 1271.1) * mm, "end": v(408.34, 1271.1) * mm});
            skLineSegment(sketch, "E2.14.5.2", {"start": v(358.34, 1321.1) * mm, "end": v(358.34, 1271.1) * mm});
            skLineSegment(sketch, "E2.14.5.3", {"start": v(358.34, 1321.1) * mm, "end": v(408.34, 1321.1) * mm});
            skLineSegment(sketch, "E2.14.6.0", {"start": v(408.34, 1261.1) * mm, "end": v(408.34, 1211.1) * mm});
            skLineSegment(sketch, "E2.14.6.1", {"start": v(358.34, 1211.1) * mm, "end": v(408.34, 1211.1) * mm});
            skLineSegment(sketch, "E2.14.6.2", {"start": v(358.34, 1261.1) * mm, "end": v(358.34, 1211.1) * mm});
            skLineSegment(sketch, "E2.14.6.3", {"start": v(358.34, 1261.1) * mm, "end": v(408.34, 1261.1) * mm});
            skLineSegment(sketch, "E2.14.7.0", {"start": v(408.34, 1201.1) * mm, "end": v(408.34, 1151.1) * mm});
            skLineSegment(sketch, "E2.14.7.1", {"start": v(358.34, 1151.1) * mm, "end": v(408.34, 1151.1) * mm});
            skLineSegment(sketch, "E2.14.7.2", {"start": v(358.34, 1201.1) * mm, "end": v(358.34, 1151.1) * mm});
            skLineSegment(sketch, "E2.14.7.3", {"start": v(358.34, 1201.1) * mm, "end": v(408.34, 1201.1) * mm});
            skLineSegment(sketch, "E2.14.8.0", {"start": v(408.34, 1141.1) * mm, "end": v(408.34, 1091.1) * mm});
            skLineSegment(sketch, "E2.14.8.1", {"start": v(358.34, 1091.1) * mm, "end": v(408.34, 1091.1) * mm});
            skLineSegment(sketch, "E2.14.8.2", {"start": v(358.34, 1141.1) * mm, "end": v(358.34, 1091.1) * mm});
            skLineSegment(sketch, "E2.14.8.3", {"start": v(358.34, 1141.1) * mm, "end": v(408.34, 1141.1) * mm});
            skLineSegment(sketch, "E2.14.9.0", {"start": v(408.34, 1081.1) * mm, "end": v(408.34, 1031.1) * mm});
            skLineSegment(sketch, "E2.14.9.1", {"start": v(358.34, 1031.1) * mm, "end": v(408.34, 1031.1) * mm});
            skLineSegment(sketch, "E2.14.9.2", {"start": v(358.34, 1081.1) * mm, "end": v(358.34, 1031.1) * mm});
            skLineSegment(sketch, "E2.14.9.3", {"start": v(358.34, 1081.1) * mm, "end": v(408.34, 1081.1) * mm});
            skLineSegment(sketch, "E2.14.10.0", {"start": v(408.34, 1021.1) * mm, "end": v(408.34, 971.1) * mm});
            skLineSegment(sketch, "E2.14.10.1", {"start": v(358.34, 971.1) * mm, "end": v(408.34, 971.1) * mm});
            skLineSegment(sketch, "E2.14.10.2", {"start": v(358.34, 1021.1) * mm, "end": v(358.34, 971.1) * mm});
            skLineSegment(sketch, "E2.14.10.3", {"start": v(358.34, 1021.1) * mm, "end": v(408.34, 1021.1) * mm});
            skLineSegment(sketch, "E2.14.11.0", {"start": v(408.34, 961.1) * mm, "end": v(408.34, 911.1) * mm});
            skLineSegment(sketch, "E2.14.11.1", {"start": v(358.34, 911.1) * mm, "end": v(408.34, 911.1) * mm});
            skLineSegment(sketch, "E2.14.11.2", {"start": v(358.34, 961.1) * mm, "end": v(358.34, 911.1) * mm});
            skLineSegment(sketch, "E2.14.11.3", {"start": v(358.34, 961.1) * mm, "end": v(408.34, 961.1) * mm});
            skLineSegment(sketch, "E2.14.12.0", {"start": v(408.34, 901.1) * mm, "end": v(408.34, 851.1) * mm});
            skLineSegment(sketch, "E2.14.12.1", {"start": v(358.34, 851.1) * mm, "end": v(408.34, 851.1) * mm});
            skLineSegment(sketch, "E2.14.12.2", {"start": v(358.34, 901.1) * mm, "end": v(358.34, 851.1) * mm});
            skLineSegment(sketch, "E2.14.12.3", {"start": v(358.34, 901.1) * mm, "end": v(408.34, 901.1) * mm});
            skLineSegment(sketch, "E2.14.13.0", {"start": v(408.34, 841.1) * mm, "end": v(408.34, 791.1) * mm});
            skLineSegment(sketch, "E2.14.13.1", {"start": v(358.34, 791.1) * mm, "end": v(408.34, 791.1) * mm});
            skLineSegment(sketch, "E2.14.13.2", {"start": v(358.34, 841.1) * mm, "end": v(358.34, 791.1) * mm});
            skLineSegment(sketch, "E2.14.13.3", {"start": v(358.34, 841.1) * mm, "end": v(408.34, 841.1) * mm});
            skLineSegment(sketch, "E2.14.14.0", {"start": v(408.34, 781.1) * mm, "end": v(408.34, 731.1) * mm});
            skLineSegment(sketch, "E2.14.14.1", {"start": v(358.34, 731.1) * mm, "end": v(408.34, 731.1) * mm});
            skLineSegment(sketch, "E2.14.14.2", {"start": v(358.34, 781.1) * mm, "end": v(358.34, 731.1) * mm});
            skLineSegment(sketch, "E2.14.14.3", {"start": v(358.34, 781.1) * mm, "end": v(408.34, 781.1) * mm});
            skLineSegment(sketch, "E2.14.15.0", {"start": v(408.34, 721.1) * mm, "end": v(408.34, 671.1) * mm});
            skLineSegment(sketch, "E2.14.15.1", {"start": v(358.34, 671.1) * mm, "end": v(408.34, 671.1) * mm});
            skLineSegment(sketch, "E2.14.15.2", {"start": v(358.34, 721.1) * mm, "end": v(358.34, 671.1) * mm});
            skLineSegment(sketch, "E2.14.15.3", {"start": v(358.34, 721.1) * mm, "end": v(408.34, 721.1) * mm});
            skLineSegment(sketch, "E2.14.16.0", {"start": v(408.34, 661.1) * mm, "end": v(408.34, 611.1) * mm});
            skLineSegment(sketch, "E2.14.16.1", {"start": v(358.34, 611.1) * mm, "end": v(408.34, 611.1) * mm});
            skLineSegment(sketch, "E2.14.16.2", {"start": v(358.34, 661.1) * mm, "end": v(358.34, 611.1) * mm});
            skLineSegment(sketch, "E2.14.16.3", {"start": v(358.34, 661.1) * mm, "end": v(408.34, 661.1) * mm});
            skLineSegment(sketch, "E2.14.17.0", {"start": v(408.34, 601.1) * mm, "end": v(408.34, 551.1) * mm});
            skLineSegment(sketch, "E2.14.17.1", {"start": v(358.34, 551.1) * mm, "end": v(408.34, 551.1) * mm});
            skLineSegment(sketch, "E2.14.17.2", {"start": v(358.34, 601.1) * mm, "end": v(358.34, 551.1) * mm});
            skLineSegment(sketch, "E2.14.17.3", {"start": v(358.34, 601.1) * mm, "end": v(408.34, 601.1) * mm});
            skLineSegment(sketch, "E2.14.18.0", {"start": v(408.34, 541.1) * mm, "end": v(408.34, 491.1) * mm});
            skLineSegment(sketch, "E2.14.18.1", {"start": v(358.34, 491.1) * mm, "end": v(408.34, 491.1) * mm});
            skLineSegment(sketch, "E2.14.18.2", {"start": v(358.34, 541.1) * mm, "end": v(358.34, 491.1) * mm});
            skLineSegment(sketch, "E2.14.18.3", {"start": v(358.34, 541.1) * mm, "end": v(408.34, 541.1) * mm});
            skLineSegment(sketch, "E2.14.19.0", {"start": v(408.34, 481.1) * mm, "end": v(408.34, 431.1) * mm});
            skLineSegment(sketch, "E2.14.19.1", {"start": v(358.34, 431.1) * mm, "end": v(408.34, 431.1) * mm});
            skLineSegment(sketch, "E2.14.19.2", {"start": v(358.34, 481.1) * mm, "end": v(358.34, 431.1) * mm});
            skLineSegment(sketch, "E2.14.19.3", {"start": v(358.34, 481.1) * mm, "end": v(408.34, 481.1) * mm});
            skLineSegment(sketch, "E2.14.20.0", {"start": v(408.34, 421.1) * mm, "end": v(408.34, 371.1) * mm});
            skLineSegment(sketch, "E2.14.20.1", {"start": v(358.34, 371.1) * mm, "end": v(408.34, 371.1) * mm});
            skLineSegment(sketch, "E2.14.20.2", {"start": v(358.34, 421.1) * mm, "end": v(358.34, 371.1) * mm});
            skLineSegment(sketch, "E2.14.20.3", {"start": v(358.34, 421.1) * mm, "end": v(408.34, 421.1) * mm});
            skLineSegment(sketch, "E2.14.21.0", {"start": v(408.34, 361.1) * mm, "end": v(408.34, 311.1) * mm});
            skLineSegment(sketch, "E2.14.21.1", {"start": v(358.34, 311.1) * mm, "end": v(408.34, 311.1) * mm});
            skLineSegment(sketch, "E2.14.21.2", {"start": v(358.34, 361.1) * mm, "end": v(358.34, 311.1) * mm});
            skLineSegment(sketch, "E2.14.21.3", {"start": v(358.34, 361.1) * mm, "end": v(408.34, 361.1) * mm});
            skLineSegment(sketch, "E2.14.22.0", {"start": v(408.34, 301.1) * mm, "end": v(408.34, 251.1) * mm});
            skLineSegment(sketch, "E2.14.22.1", {"start": v(358.34, 251.1) * mm, "end": v(408.34, 251.1) * mm});
            skLineSegment(sketch, "E2.14.22.2", {"start": v(358.34, 301.1) * mm, "end": v(358.34, 251.1) * mm});
            skLineSegment(sketch, "E2.14.22.3", {"start": v(358.34, 301.1) * mm, "end": v(408.34, 301.1) * mm});
            skLineSegment(sketch, "E2.14.23.0", {"start": v(408.34, 241.1) * mm, "end": v(408.34, 191.1) * mm});
            skLineSegment(sketch, "E2.14.23.1", {"start": v(358.34, 191.1) * mm, "end": v(408.34, 191.1) * mm});
            skLineSegment(sketch, "E2.14.23.2", {"start": v(358.34, 241.1) * mm, "end": v(358.34, 191.1) * mm});
            skLineSegment(sketch, "E2.14.23.3", {"start": v(358.34, 241.1) * mm, "end": v(408.34, 241.1) * mm});
            skLineSegment(sketch, "E2.14.24.0", {"start": v(408.34, 181.1) * mm, "end": v(408.34, 131.1) * mm});
            skLineSegment(sketch, "E2.14.24.1", {"start": v(358.34, 131.1) * mm, "end": v(408.34, 131.1) * mm});
            skLineSegment(sketch, "E2.14.24.2", {"start": v(358.34, 181.1) * mm, "end": v(358.34, 131.1) * mm});
            skLineSegment(sketch, "E2.14.24.3", {"start": v(358.34, 181.1) * mm, "end": v(408.34, 181.1) * mm});
            skLineSegment(sketch, "E2.14.25.0", {"start": v(408.34, 121.1) * mm, "end": v(408.34, 71.1) * mm});
            skLineSegment(sketch, "E2.14.25.1", {"start": v(358.34, 71.1) * mm, "end": v(408.34, 71.1) * mm});
            skLineSegment(sketch, "E2.14.25.2", {"start": v(358.34, 121.1) * mm, "end": v(358.34, 71.1) * mm});
            skLineSegment(sketch, "E2.14.25.3", {"start": v(358.34, 121.1) * mm, "end": v(408.34, 121.1) * mm});
            skLineSegment(sketch, "E2.14.26.0", {"start": v(408.34, 61.1) * mm, "end": v(408.34, 11.1) * mm});
            skLineSegment(sketch, "E2.14.26.1", {"start": v(358.34, 11.1) * mm, "end": v(408.34, 11.1) * mm});
            skLineSegment(sketch, "E2.14.26.2", {"start": v(358.34, 61.1) * mm, "end": v(358.34, 11.1) * mm});
            skLineSegment(sketch, "E2.14.26.3", {"start": v(358.34, 61.1) * mm, "end": v(408.34, 61.1) * mm});
            skLineSegment(sketch, "E2.14.27.0", {"start": v(408.34, 1.1) * mm, "end": v(408.34, -48.9) * mm});
            skLineSegment(sketch, "E2.14.27.1", {"start": v(358.34, -48.9) * mm, "end": v(408.34, -48.9) * mm});
            skLineSegment(sketch, "E2.14.27.2", {"start": v(358.34, 1.1) * mm, "end": v(358.34, -48.9) * mm});
            skLineSegment(sketch, "E2.14.27.3", {"start": v(358.34, 1.1) * mm, "end": v(408.34, 1.1) * mm});
            skLineSegment(sketch, "E2.14.28.0", {"start": v(408.34, -58.9) * mm, "end": v(408.34, -108.9) * mm});
            skLineSegment(sketch, "E2.14.28.1", {"start": v(358.34, -108.9) * mm, "end": v(408.34, -108.9) * mm});
            skLineSegment(sketch, "E2.14.28.2", {"start": v(358.34, -58.9) * mm, "end": v(358.34, -108.9) * mm});
            skLineSegment(sketch, "E2.14.28.3", {"start": v(358.34, -58.9) * mm, "end": v(408.34, -58.9) * mm});
            skLineSegment(sketch, "E2.14.29.0", {"start": v(408.34, -118.9) * mm, "end": v(408.34, -168.9) * mm});
            skLineSegment(sketch, "E2.14.29.1", {"start": v(358.34, -168.9) * mm, "end": v(408.34, -168.9) * mm});
            skLineSegment(sketch, "E2.14.29.2", {"start": v(358.34, -118.9) * mm, "end": v(358.34, -168.9) * mm});
            skLineSegment(sketch, "E2.14.29.3", {"start": v(358.34, -118.9) * mm, "end": v(408.34, -118.9) * mm});
            skLineSegment(sketch, "E2.14.30.0", {"start": v(408.34, -178.9) * mm, "end": v(408.34, -228.9) * mm});
            skLineSegment(sketch, "E2.14.30.1", {"start": v(358.34, -228.9) * mm, "end": v(408.34, -228.9) * mm});
            skLineSegment(sketch, "E2.14.30.2", {"start": v(358.34, -178.9) * mm, "end": v(358.34, -228.9) * mm});
            skLineSegment(sketch, "E2.14.30.3", {"start": v(358.34, -178.9) * mm, "end": v(408.34, -178.9) * mm});
            skLineSegment(sketch, "E2.14.31.0", {"start": v(408.34, -238.9) * mm, "end": v(408.34, -288.9) * mm});
            skLineSegment(sketch, "E2.14.31.1", {"start": v(358.34, -288.9) * mm, "end": v(408.34, -288.9) * mm});
            skLineSegment(sketch, "E2.14.31.2", {"start": v(358.34, -238.9) * mm, "end": v(358.34, -288.9) * mm});
            skLineSegment(sketch, "E2.14.31.3", {"start": v(358.34, -238.9) * mm, "end": v(408.34, -238.9) * mm});
            skLineSegment(sketch, "E2.14.32.0", {"start": v(408.34, -298.9) * mm, "end": v(408.34, -348.9) * mm});
            skLineSegment(sketch, "E2.14.32.1", {"start": v(358.34, -348.9) * mm, "end": v(408.34, -348.9) * mm});
            skLineSegment(sketch, "E2.14.32.2", {"start": v(358.34, -298.9) * mm, "end": v(358.34, -348.9) * mm});
            skLineSegment(sketch, "E2.14.32.3", {"start": v(358.34, -298.9) * mm, "end": v(408.34, -298.9) * mm});
            skLineSegment(sketch, "E2.15.0.0", {"start": v(468.34, 1621.1) * mm, "end": v(468.34, 1571.1) * mm});
            skLineSegment(sketch, "E2.15.0.1", {"start": v(418.34, 1571.1) * mm, "end": v(468.34, 1571.1) * mm});
            skLineSegment(sketch, "E2.15.0.2", {"start": v(418.34, 1621.1) * mm, "end": v(418.34, 1571.1) * mm});
            skLineSegment(sketch, "E2.15.0.3", {"start": v(418.34, 1621.1) * mm, "end": v(468.34, 1621.1) * mm});
            skLineSegment(sketch, "E2.15.1.0", {"start": v(468.34, 1561.1) * mm, "end": v(468.34, 1511.1) * mm});
            skLineSegment(sketch, "E2.15.1.1", {"start": v(418.34, 1511.1) * mm, "end": v(468.34, 1511.1) * mm});
            skLineSegment(sketch, "E2.15.1.2", {"start": v(418.34, 1561.1) * mm, "end": v(418.34, 1511.1) * mm});
            skLineSegment(sketch, "E2.15.1.3", {"start": v(418.34, 1561.1) * mm, "end": v(468.34, 1561.1) * mm});
            skLineSegment(sketch, "E2.15.2.0", {"start": v(468.34, 1501.1) * mm, "end": v(468.34, 1451.1) * mm});
            skLineSegment(sketch, "E2.15.2.1", {"start": v(418.34, 1451.1) * mm, "end": v(468.34, 1451.1) * mm});
            skLineSegment(sketch, "E2.15.2.2", {"start": v(418.34, 1501.1) * mm, "end": v(418.34, 1451.1) * mm});
            skLineSegment(sketch, "E2.15.2.3", {"start": v(418.34, 1501.1) * mm, "end": v(468.34, 1501.1) * mm});
            skLineSegment(sketch, "E2.15.3.0", {"start": v(468.34, 1441.1) * mm, "end": v(468.34, 1391.1) * mm});
            skLineSegment(sketch, "E2.15.3.1", {"start": v(418.34, 1391.1) * mm, "end": v(468.34, 1391.1) * mm});
            skLineSegment(sketch, "E2.15.3.2", {"start": v(418.34, 1441.1) * mm, "end": v(418.34, 1391.1) * mm});
            skLineSegment(sketch, "E2.15.3.3", {"start": v(418.34, 1441.1) * mm, "end": v(468.34, 1441.1) * mm});
            skLineSegment(sketch, "E2.15.4.0", {"start": v(468.34, 1381.1) * mm, "end": v(468.34, 1331.1) * mm});
            skLineSegment(sketch, "E2.15.4.1", {"start": v(418.34, 1331.1) * mm, "end": v(468.34, 1331.1) * mm});
            skLineSegment(sketch, "E2.15.4.2", {"start": v(418.34, 1381.1) * mm, "end": v(418.34, 1331.1) * mm});
            skLineSegment(sketch, "E2.15.4.3", {"start": v(418.34, 1381.1) * mm, "end": v(468.34, 1381.1) * mm});
            skLineSegment(sketch, "E2.15.5.0", {"start": v(468.34, 1321.1) * mm, "end": v(468.34, 1271.1) * mm});
            skLineSegment(sketch, "E2.15.5.1", {"start": v(418.34, 1271.1) * mm, "end": v(468.34, 1271.1) * mm});
            skLineSegment(sketch, "E2.15.5.2", {"start": v(418.34, 1321.1) * mm, "end": v(418.34, 1271.1) * mm});
            skLineSegment(sketch, "E2.15.5.3", {"start": v(418.34, 1321.1) * mm, "end": v(468.34, 1321.1) * mm});
            skLineSegment(sketch, "E2.15.6.0", {"start": v(468.34, 1261.1) * mm, "end": v(468.34, 1211.1) * mm});
            skLineSegment(sketch, "E2.15.6.1", {"start": v(418.34, 1211.1) * mm, "end": v(468.34, 1211.1) * mm});
            skLineSegment(sketch, "E2.15.6.2", {"start": v(418.34, 1261.1) * mm, "end": v(418.34, 1211.1) * mm});
            skLineSegment(sketch, "E2.15.6.3", {"start": v(418.34, 1261.1) * mm, "end": v(468.34, 1261.1) * mm});
            skLineSegment(sketch, "E2.15.7.0", {"start": v(468.34, 1201.1) * mm, "end": v(468.34, 1151.1) * mm});
            skLineSegment(sketch, "E2.15.7.1", {"start": v(418.34, 1151.1) * mm, "end": v(468.34, 1151.1) * mm});
            skLineSegment(sketch, "E2.15.7.2", {"start": v(418.34, 1201.1) * mm, "end": v(418.34, 1151.1) * mm});
            skLineSegment(sketch, "E2.15.7.3", {"start": v(418.34, 1201.1) * mm, "end": v(468.34, 1201.1) * mm});
            skLineSegment(sketch, "E2.15.8.0", {"start": v(468.34, 1141.1) * mm, "end": v(468.34, 1091.1) * mm});
            skLineSegment(sketch, "E2.15.8.1", {"start": v(418.34, 1091.1) * mm, "end": v(468.34, 1091.1) * mm});
            skLineSegment(sketch, "E2.15.8.2", {"start": v(418.34, 1141.1) * mm, "end": v(418.34, 1091.1) * mm});
            skLineSegment(sketch, "E2.15.8.3", {"start": v(418.34, 1141.1) * mm, "end": v(468.34, 1141.1) * mm});
            skLineSegment(sketch, "E2.15.9.0", {"start": v(468.34, 1081.1) * mm, "end": v(468.34, 1031.1) * mm});
            skLineSegment(sketch, "E2.15.9.1", {"start": v(418.34, 1031.1) * mm, "end": v(468.34, 1031.1) * mm});
            skLineSegment(sketch, "E2.15.9.2", {"start": v(418.34, 1081.1) * mm, "end": v(418.34, 1031.1) * mm});
            skLineSegment(sketch, "E2.15.9.3", {"start": v(418.34, 1081.1) * mm, "end": v(468.34, 1081.1) * mm});
            skLineSegment(sketch, "E2.15.10.0", {"start": v(468.34, 1021.1) * mm, "end": v(468.34, 971.1) * mm});
            skLineSegment(sketch, "E2.15.10.1", {"start": v(418.34, 971.1) * mm, "end": v(468.34, 971.1) * mm});
            skLineSegment(sketch, "E2.15.10.2", {"start": v(418.34, 1021.1) * mm, "end": v(418.34, 971.1) * mm});
            skLineSegment(sketch, "E2.15.10.3", {"start": v(418.34, 1021.1) * mm, "end": v(468.34, 1021.1) * mm});
            skLineSegment(sketch, "E2.15.11.0", {"start": v(468.34, 961.1) * mm, "end": v(468.34, 911.1) * mm});
            skLineSegment(sketch, "E2.15.11.1", {"start": v(418.34, 911.1) * mm, "end": v(468.34, 911.1) * mm});
            skLineSegment(sketch, "E2.15.11.2", {"start": v(418.34, 961.1) * mm, "end": v(418.34, 911.1) * mm});
            skLineSegment(sketch, "E2.15.11.3", {"start": v(418.34, 961.1) * mm, "end": v(468.34, 961.1) * mm});
            skLineSegment(sketch, "E2.15.12.0", {"start": v(468.34, 901.1) * mm, "end": v(468.34, 851.1) * mm});
            skLineSegment(sketch, "E2.15.12.1", {"start": v(418.34, 851.1) * mm, "end": v(468.34, 851.1) * mm});
            skLineSegment(sketch, "E2.15.12.2", {"start": v(418.34, 901.1) * mm, "end": v(418.34, 851.1) * mm});
            skLineSegment(sketch, "E2.15.12.3", {"start": v(418.34, 901.1) * mm, "end": v(468.34, 901.1) * mm});
            skLineSegment(sketch, "E2.15.13.0", {"start": v(468.34, 841.1) * mm, "end": v(468.34, 791.1) * mm});
            skLineSegment(sketch, "E2.15.13.1", {"start": v(418.34, 791.1) * mm, "end": v(468.34, 791.1) * mm});
            skLineSegment(sketch, "E2.15.13.2", {"start": v(418.34, 841.1) * mm, "end": v(418.34, 791.1) * mm});
            skLineSegment(sketch, "E2.15.13.3", {"start": v(418.34, 841.1) * mm, "end": v(468.34, 841.1) * mm});
            skLineSegment(sketch, "E2.15.14.0", {"start": v(468.34, 781.1) * mm, "end": v(468.34, 731.1) * mm});
            skLineSegment(sketch, "E2.15.14.1", {"start": v(418.34, 731.1) * mm, "end": v(468.34, 731.1) * mm});
            skLineSegment(sketch, "E2.15.14.2", {"start": v(418.34, 781.1) * mm, "end": v(418.34, 731.1) * mm});
            skLineSegment(sketch, "E2.15.14.3", {"start": v(418.34, 781.1) * mm, "end": v(468.34, 781.1) * mm});
            skLineSegment(sketch, "E2.15.15.0", {"start": v(468.34, 721.1) * mm, "end": v(468.34, 671.1) * mm});
            skLineSegment(sketch, "E2.15.15.1", {"start": v(418.34, 671.1) * mm, "end": v(468.34, 671.1) * mm});
            skLineSegment(sketch, "E2.15.15.2", {"start": v(418.34, 721.1) * mm, "end": v(418.34, 671.1) * mm});
            skLineSegment(sketch, "E2.15.15.3", {"start": v(418.34, 721.1) * mm, "end": v(468.34, 721.1) * mm});
            skLineSegment(sketch, "E2.15.16.0", {"start": v(468.34, 661.1) * mm, "end": v(468.34, 611.1) * mm});
            skLineSegment(sketch, "E2.15.16.1", {"start": v(418.34, 611.1) * mm, "end": v(468.34, 611.1) * mm});
            skLineSegment(sketch, "E2.15.16.2", {"start": v(418.34, 661.1) * mm, "end": v(418.34, 611.1) * mm});
            skLineSegment(sketch, "E2.15.16.3", {"start": v(418.34, 661.1) * mm, "end": v(468.34, 661.1) * mm});
            skLineSegment(sketch, "E2.15.17.0", {"start": v(468.34, 601.1) * mm, "end": v(468.34, 551.1) * mm});
            skLineSegment(sketch, "E2.15.17.1", {"start": v(418.34, 551.1) * mm, "end": v(468.34, 551.1) * mm});
            skLineSegment(sketch, "E2.15.17.2", {"start": v(418.34, 601.1) * mm, "end": v(418.34, 551.1) * mm});
            skLineSegment(sketch, "E2.15.17.3", {"start": v(418.34, 601.1) * mm, "end": v(468.34, 601.1) * mm});
            skLineSegment(sketch, "E2.15.18.0", {"start": v(468.34, 541.1) * mm, "end": v(468.34, 491.1) * mm});
            skLineSegment(sketch, "E2.15.18.1", {"start": v(418.34, 491.1) * mm, "end": v(468.34, 491.1) * mm});
            skLineSegment(sketch, "E2.15.18.2", {"start": v(418.34, 541.1) * mm, "end": v(418.34, 491.1) * mm});
            skLineSegment(sketch, "E2.15.18.3", {"start": v(418.34, 541.1) * mm, "end": v(468.34, 541.1) * mm});
            skLineSegment(sketch, "E2.15.19.0", {"start": v(468.34, 481.1) * mm, "end": v(468.34, 431.1) * mm});
            skLineSegment(sketch, "E2.15.19.1", {"start": v(418.34, 431.1) * mm, "end": v(468.34, 431.1) * mm});
            skLineSegment(sketch, "E2.15.19.2", {"start": v(418.34, 481.1) * mm, "end": v(418.34, 431.1) * mm});
            skLineSegment(sketch, "E2.15.19.3", {"start": v(418.34, 481.1) * mm, "end": v(468.34, 481.1) * mm});
            skLineSegment(sketch, "E2.15.20.0", {"start": v(468.34, 421.1) * mm, "end": v(468.34, 371.1) * mm});
            skLineSegment(sketch, "E2.15.20.1", {"start": v(418.34, 371.1) * mm, "end": v(468.34, 371.1) * mm});
            skLineSegment(sketch, "E2.15.20.2", {"start": v(418.34, 421.1) * mm, "end": v(418.34, 371.1) * mm});
            skLineSegment(sketch, "E2.15.20.3", {"start": v(418.34, 421.1) * mm, "end": v(468.34, 421.1) * mm});
            skLineSegment(sketch, "E2.15.21.0", {"start": v(468.34, 361.1) * mm, "end": v(468.34, 311.1) * mm});
            skLineSegment(sketch, "E2.15.21.1", {"start": v(418.34, 311.1) * mm, "end": v(468.34, 311.1) * mm});
            skLineSegment(sketch, "E2.15.21.2", {"start": v(418.34, 361.1) * mm, "end": v(418.34, 311.1) * mm});
            skLineSegment(sketch, "E2.15.21.3", {"start": v(418.34, 361.1) * mm, "end": v(468.34, 361.1) * mm});
            skLineSegment(sketch, "E2.15.22.0", {"start": v(468.34, 301.1) * mm, "end": v(468.34, 251.1) * mm});
            skLineSegment(sketch, "E2.15.22.1", {"start": v(418.34, 251.1) * mm, "end": v(468.34, 251.1) * mm});
            skLineSegment(sketch, "E2.15.22.2", {"start": v(418.34, 301.1) * mm, "end": v(418.34, 251.1) * mm});
            skLineSegment(sketch, "E2.15.22.3", {"start": v(418.34, 301.1) * mm, "end": v(468.34, 301.1) * mm});
            skLineSegment(sketch, "E2.15.23.0", {"start": v(468.34, 241.1) * mm, "end": v(468.34, 191.1) * mm});
            skLineSegment(sketch, "E2.15.23.1", {"start": v(418.34, 191.1) * mm, "end": v(468.34, 191.1) * mm});
            skLineSegment(sketch, "E2.15.23.2", {"start": v(418.34, 241.1) * mm, "end": v(418.34, 191.1) * mm});
            skLineSegment(sketch, "E2.15.23.3", {"start": v(418.34, 241.1) * mm, "end": v(468.34, 241.1) * mm});
            skLineSegment(sketch, "E2.15.24.0", {"start": v(468.34, 181.1) * mm, "end": v(468.34, 131.1) * mm});
            skLineSegment(sketch, "E2.15.24.1", {"start": v(418.34, 131.1) * mm, "end": v(468.34, 131.1) * mm});
            skLineSegment(sketch, "E2.15.24.2", {"start": v(418.34, 181.1) * mm, "end": v(418.34, 131.1) * mm});
            skLineSegment(sketch, "E2.15.24.3", {"start": v(418.34, 181.1) * mm, "end": v(468.34, 181.1) * mm});
            skLineSegment(sketch, "E2.15.25.0", {"start": v(468.34, 121.1) * mm, "end": v(468.34, 71.1) * mm});
            skLineSegment(sketch, "E2.15.25.1", {"start": v(418.34, 71.1) * mm, "end": v(468.34, 71.1) * mm});
            skLineSegment(sketch, "E2.15.25.2", {"start": v(418.34, 121.1) * mm, "end": v(418.34, 71.1) * mm});
            skLineSegment(sketch, "E2.15.25.3", {"start": v(418.34, 121.1) * mm, "end": v(468.34, 121.1) * mm});
            skLineSegment(sketch, "E2.15.26.0", {"start": v(468.34, 61.1) * mm, "end": v(468.34, 11.1) * mm});
            skLineSegment(sketch, "E2.15.26.1", {"start": v(418.34, 11.1) * mm, "end": v(468.34, 11.1) * mm});
            skLineSegment(sketch, "E2.15.26.2", {"start": v(418.34, 61.1) * mm, "end": v(418.34, 11.1) * mm});
            skLineSegment(sketch, "E2.15.26.3", {"start": v(418.34, 61.1) * mm, "end": v(468.34, 61.1) * mm});
            skLineSegment(sketch, "E2.15.27.0", {"start": v(468.34, 1.1) * mm, "end": v(468.34, -48.9) * mm});
            skLineSegment(sketch, "E2.15.27.1", {"start": v(418.34, -48.9) * mm, "end": v(468.34, -48.9) * mm});
            skLineSegment(sketch, "E2.15.27.2", {"start": v(418.34, 1.1) * mm, "end": v(418.34, -48.9) * mm});
            skLineSegment(sketch, "E2.15.27.3", {"start": v(418.34, 1.1) * mm, "end": v(468.34, 1.1) * mm});
            skLineSegment(sketch, "E2.15.28.0", {"start": v(468.34, -58.9) * mm, "end": v(468.34, -108.9) * mm});
            skLineSegment(sketch, "E2.15.28.1", {"start": v(418.34, -108.9) * mm, "end": v(468.34, -108.9) * mm});
            skLineSegment(sketch, "E2.15.28.2", {"start": v(418.34, -58.9) * mm, "end": v(418.34, -108.9) * mm});
            skLineSegment(sketch, "E2.15.28.3", {"start": v(418.34, -58.9) * mm, "end": v(468.34, -58.9) * mm});
            skLineSegment(sketch, "E2.15.29.0", {"start": v(468.34, -118.9) * mm, "end": v(468.34, -168.9) * mm});
            skLineSegment(sketch, "E2.15.29.1", {"start": v(418.34, -168.9) * mm, "end": v(468.34, -168.9) * mm});
            skLineSegment(sketch, "E2.15.29.2", {"start": v(418.34, -118.9) * mm, "end": v(418.34, -168.9) * mm});
            skLineSegment(sketch, "E2.15.29.3", {"start": v(418.34, -118.9) * mm, "end": v(468.34, -118.9) * mm});
            skLineSegment(sketch, "E2.15.30.0", {"start": v(468.34, -178.9) * mm, "end": v(468.34, -228.9) * mm});
            skLineSegment(sketch, "E2.15.30.1", {"start": v(418.34, -228.9) * mm, "end": v(468.34, -228.9) * mm});
            skLineSegment(sketch, "E2.15.30.2", {"start": v(418.34, -178.9) * mm, "end": v(418.34, -228.9) * mm});
            skLineSegment(sketch, "E2.15.30.3", {"start": v(418.34, -178.9) * mm, "end": v(468.34, -178.9) * mm});
            skLineSegment(sketch, "E2.15.31.0", {"start": v(468.34, -238.9) * mm, "end": v(468.34, -288.9) * mm});
            skLineSegment(sketch, "E2.15.31.1", {"start": v(418.34, -288.9) * mm, "end": v(468.34, -288.9) * mm});
            skLineSegment(sketch, "E2.15.31.2", {"start": v(418.34, -238.9) * mm, "end": v(418.34, -288.9) * mm});
            skLineSegment(sketch, "E2.15.31.3", {"start": v(418.34, -238.9) * mm, "end": v(468.34, -238.9) * mm});
            skLineSegment(sketch, "E2.15.32.0", {"start": v(468.34, -298.9) * mm, "end": v(468.34, -348.9) * mm});
            skLineSegment(sketch, "E2.15.32.1", {"start": v(418.34, -348.9) * mm, "end": v(468.34, -348.9) * mm});
            skLineSegment(sketch, "E2.15.32.2", {"start": v(418.34, -298.9) * mm, "end": v(418.34, -348.9) * mm});
            skLineSegment(sketch, "E2.15.32.3", {"start": v(418.34, -298.9) * mm, "end": v(468.34, -298.9) * mm});
            skLineSegment(sketch, "E2.direction1", {"start": v(-431.66, 1571.1) * mm, "end": v(-371.66, 1571.1) * mm, "construction": true});
            skLineSegment(sketch, "E2.direction2", {"start": v(-431.66, 1571.1) * mm, "end": v(-431.66, 1511.1) * mm, "construction": true});
            skSolve(sketch);
        }
        {
            var Q0;
            Q0 = qSketchRegion(id + "F2", true);
            extrude(context, id + "F3", {"entities" : qUnion([Q0]), "operationType" : NewBodyOperationType.REMOVE, "oppositeDirection" : true, "depth" : 25 * mm});
        }
    });
